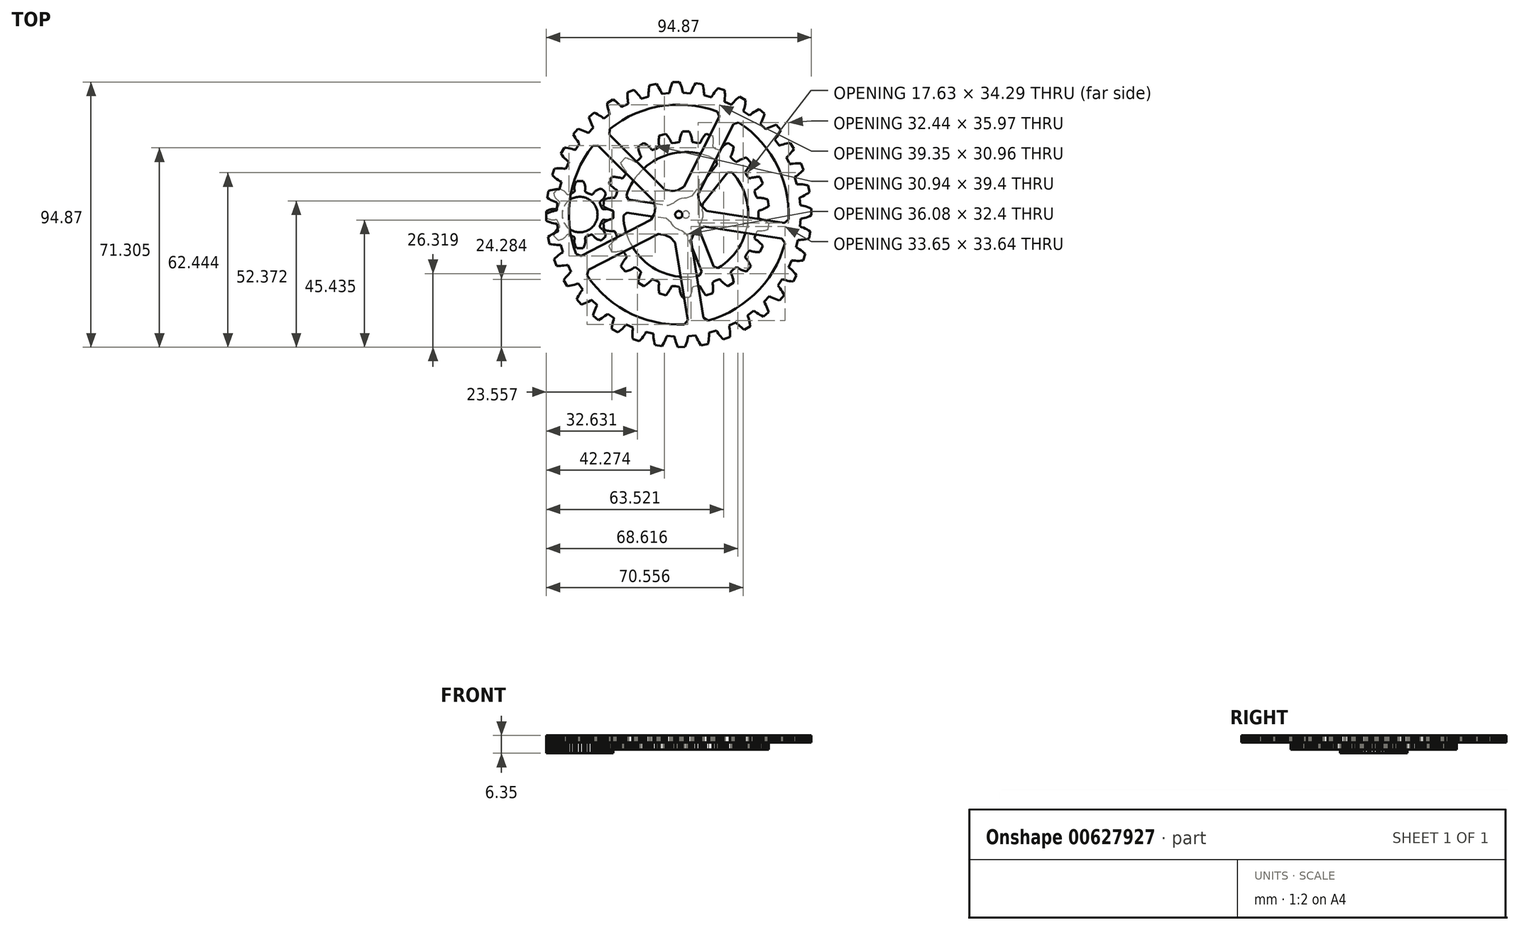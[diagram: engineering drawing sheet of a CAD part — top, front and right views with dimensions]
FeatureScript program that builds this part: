
annotation { "Feature Type Name" : "Feature", "Feature Type Description" : "" }
export const myFeature = defineFeature(function(context is Context, id is Id, definition is map)
    precondition{}
    {
        {
            var Q0;
            Q0=qCreatedBy(makeId("Top.planeOp"),FACE);
            var sketch = newSketch(context, id + "F0", { "sketchPlane" : qUnion([Q0])});
            skLineSegment(sketch, "E0", {"start": v(18.22, -1.29) * mm, "end": v(18.38, -1.34) * mm});
            skLineSegment(sketch, "E1", {"start": v(18.38, -1.34) * mm, "end": v(18.53, -1.39) * mm});
            skLineSegment(sketch, "E2", {"start": v(18.53, -1.39) * mm, "end": v(18.84, -1.5) * mm});
            skLineSegment(sketch, "E3", {"start": v(18.84, -1.5) * mm, "end": v(19.45, -1.75) * mm});
            skLineSegment(sketch, "E4", {"start": v(19.45, -1.75) * mm, "end": v(20.06, -2.03) * mm});
            skLineSegment(sketch, "E5", {"start": v(20.06, -2.03) * mm, "end": v(20.66, -2.35) * mm});
            skLineSegment(sketch, "E6", {"start": v(20.66, -2.35) * mm, "end": v(21.26, -2.69) * mm});
            skLineSegment(sketch, "E7", {"start": v(21.26, -2.69) * mm, "end": v(21.86, -3.06) * mm});
            skLineSegment(sketch, "E8", {"start": v(21.86, -3.06) * mm, "end": v(21.48, -5.52) * mm});
            skLineSegment(sketch, "E9", {"start": v(21.48, -5.52) * mm, "end": v(20.8, -5.7) * mm});
            skLineSegment(sketch, "E10", {"start": v(20.8, -5.7) * mm, "end": v(20.12, -5.84) * mm});
            skLineSegment(sketch, "E11", {"start": v(20.12, -5.84) * mm, "end": v(19.45, -5.96) * mm});
            skLineSegment(sketch, "E12", {"start": v(19.45, -5.96) * mm, "end": v(18.79, -6.04) * mm});
            skLineSegment(sketch, "E13", {"start": v(18.79, -6.04) * mm, "end": v(18.13, -6.1) * mm});
            skLineSegment(sketch, "E14", {"start": v(18.13, -6.1) * mm, "end": v(17.8, -6.1) * mm});
            skLineSegment(sketch, "E15", {"start": v(17.8, -6.1) * mm, "end": v(17.64, -6.11) * mm});
            skLineSegment(sketch, "E16", {"start": v(17.64, -6.11) * mm, "end": v(17.47, -6.11) * mm});
            skLineSegment(sketch, "E17", {"start": v(17.47, -6.11) * mm, "end": v(16.82, -8.76) * mm});
            skLineSegment(sketch, "E18", {"start": v(16.82, -8.76) * mm, "end": v(16.97, -8.84) * mm});
            skLineSegment(sketch, "E19", {"start": v(16.97, -8.84) * mm, "end": v(17.1, -8.91) * mm});
            skLineSegment(sketch, "E20", {"start": v(17.1, -8.91) * mm, "end": v(17.4, -9.08) * mm});
            skLineSegment(sketch, "E21", {"start": v(17.4, -9.08) * mm, "end": v(17.95, -9.43) * mm});
            skLineSegment(sketch, "E22", {"start": v(17.95, -9.43) * mm, "end": v(18.5, -9.82) * mm});
            skLineSegment(sketch, "E23", {"start": v(18.5, -9.82) * mm, "end": v(19.04, -10.23) * mm});
            skLineSegment(sketch, "E24", {"start": v(19.04, -10.23) * mm, "end": v(19.58, -10.67) * mm});
            skLineSegment(sketch, "E25", {"start": v(19.58, -10.67) * mm, "end": v(20.1, -11.14) * mm});
            skLineSegment(sketch, "E26", {"start": v(20.1, -11.14) * mm, "end": v(19.3, -13.5) * mm});
            skLineSegment(sketch, "E27", {"start": v(19.3, -13.5) * mm, "end": v(18.6, -13.55) * mm});
            skLineSegment(sketch, "E28", {"start": v(18.6, -13.55) * mm, "end": v(17.9, -13.58) * mm});
            skLineSegment(sketch, "E29", {"start": v(17.9, -13.58) * mm, "end": v(17.22, -13.58) * mm});
            skLineSegment(sketch, "E30", {"start": v(17.22, -13.58) * mm, "end": v(16.55, -13.54) * mm});
            skLineSegment(sketch, "E31", {"start": v(16.55, -13.54) * mm, "end": v(15.9, -13.48) * mm});
            skLineSegment(sketch, "E32", {"start": v(15.9, -13.48) * mm, "end": v(15.57, -13.44) * mm});
            skLineSegment(sketch, "E33", {"start": v(15.57, -13.44) * mm, "end": v(15.4, -13.41) * mm});
            skLineSegment(sketch, "E34", {"start": v(15.4, -13.41) * mm, "end": v(15.25, -13.38) * mm});
            skLineSegment(sketch, "E35", {"start": v(15.25, -13.38) * mm, "end": v(14.15, -15.88) * mm});
            skLineSegment(sketch, "E36", {"start": v(14.15, -15.88) * mm, "end": v(14.28, -15.98) * mm});
            skLineSegment(sketch, "E37", {"start": v(14.28, -15.98) * mm, "end": v(14.4, -16.08) * mm});
            skLineSegment(sketch, "E38", {"start": v(14.4, -16.08) * mm, "end": v(14.66, -16.3) * mm});
            skLineSegment(sketch, "E39", {"start": v(14.66, -16.3) * mm, "end": v(15.15, -16.73) * mm});
            skLineSegment(sketch, "E40", {"start": v(15.15, -16.73) * mm, "end": v(15.62, -17.2) * mm});
            skLineSegment(sketch, "E41", {"start": v(15.62, -17.2) * mm, "end": v(16.08, -17.71) * mm});
            skLineSegment(sketch, "E42", {"start": v(16.08, -17.71) * mm, "end": v(16.53, -18.24) * mm});
            skLineSegment(sketch, "E43", {"start": v(16.53, -18.24) * mm, "end": v(16.96, -18.79) * mm});
            skLineSegment(sketch, "E44", {"start": v(16.96, -18.79) * mm, "end": v(15.76, -20.97) * mm});
            skLineSegment(sketch, "E45", {"start": v(15.76, -20.97) * mm, "end": v(15.06, -20.9) * mm});
            skLineSegment(sketch, "E46", {"start": v(15.06, -20.9) * mm, "end": v(14.38, -20.8) * mm});
            skLineSegment(sketch, "E47", {"start": v(14.38, -20.8) * mm, "end": v(13.7, -20.7) * mm});
            skLineSegment(sketch, "E48", {"start": v(13.7, -20.7) * mm, "end": v(13.05, -20.54) * mm});
            skLineSegment(sketch, "E49", {"start": v(13.05, -20.54) * mm, "end": v(12.41, -20.37) * mm});
            skLineSegment(sketch, "E50", {"start": v(12.41, -20.37) * mm, "end": v(12.1, -20.27) * mm});
            skLineSegment(sketch, "E51", {"start": v(12.1, -20.27) * mm, "end": v(11.95, -20.21) * mm});
            skLineSegment(sketch, "E52", {"start": v(11.95, -20.21) * mm, "end": v(11.8, -20.16) * mm});
            skLineSegment(sketch, "E53", {"start": v(11.8, -20.16) * mm, "end": v(10.28, -22.43) * mm});
            skLineSegment(sketch, "E54", {"start": v(10.28, -22.43) * mm, "end": v(10.39, -22.55) * mm});
            skLineSegment(sketch, "E55", {"start": v(10.39, -22.55) * mm, "end": v(10.5, -22.67) * mm});
            skLineSegment(sketch, "E56", {"start": v(10.5, -22.67) * mm, "end": v(10.7, -22.92) * mm});
            skLineSegment(sketch, "E57", {"start": v(10.7, -22.92) * mm, "end": v(11.11, -23.44) * mm});
            skLineSegment(sketch, "E58", {"start": v(11.11, -23.44) * mm, "end": v(11.5, -24) * mm});
            skLineSegment(sketch, "E59", {"start": v(11.5, -24) * mm, "end": v(11.86, -24.57) * mm});
            skLineSegment(sketch, "E60", {"start": v(11.86, -24.57) * mm, "end": v(12.21, -25.16) * mm});
            skLineSegment(sketch, "E61", {"start": v(12.21, -25.16) * mm, "end": v(12.54, -25.78) * mm});
            skLineSegment(sketch, "E62", {"start": v(12.54, -25.78) * mm, "end": v(10.98, -27.72) * mm});
            skLineSegment(sketch, "E63", {"start": v(10.98, -27.72) * mm, "end": v(10.3, -27.53) * mm});
            skLineSegment(sketch, "E64", {"start": v(10.3, -27.53) * mm, "end": v(9.65, -27.32) * mm});
            skLineSegment(sketch, "E65", {"start": v(9.65, -27.32) * mm, "end": v(9, -27.09) * mm});
            skLineSegment(sketch, "E66", {"start": v(9, -27.09) * mm, "end": v(8.39, -26.83) * mm});
            skLineSegment(sketch, "E67", {"start": v(8.39, -26.83) * mm, "end": v(7.8, -26.54) * mm});
            skLineSegment(sketch, "E68", {"start": v(7.8, -26.54) * mm, "end": v(7.5, -26.4) * mm});
            skLineSegment(sketch, "E69", {"start": v(7.5, -26.4) * mm, "end": v(7.36, -26.31) * mm});
            skLineSegment(sketch, "E70", {"start": v(7.36, -26.31) * mm, "end": v(7.22, -26.23) * mm});
            skLineSegment(sketch, "E71", {"start": v(7.22, -26.23) * mm, "end": v(5.33, -28.2) * mm});
            skLineSegment(sketch, "E72", {"start": v(5.33, -28.2) * mm, "end": v(5.42, -28.34) * mm});
            skLineSegment(sketch, "E73", {"start": v(5.42, -28.34) * mm, "end": v(5.5, -28.48) * mm});
            skLineSegment(sketch, "E74", {"start": v(5.5, -28.48) * mm, "end": v(5.67, -28.76) * mm});
            skLineSegment(sketch, "E75", {"start": v(5.67, -28.76) * mm, "end": v(5.98, -29.34) * mm});
            skLineSegment(sketch, "E76", {"start": v(5.98, -29.34) * mm, "end": v(6.26, -29.95) * mm});
            skLineSegment(sketch, "E77", {"start": v(6.26, -29.95) * mm, "end": v(6.52, -30.58) * mm});
            skLineSegment(sketch, "E78", {"start": v(6.52, -30.58) * mm, "end": v(6.76, -31.23) * mm});
            skLineSegment(sketch, "E79", {"start": v(6.76, -31.23) * mm, "end": v(6.98, -31.9) * mm});
            skLineSegment(sketch, "E80", {"start": v(6.98, -31.9) * mm, "end": v(5.1, -33.54) * mm});
            skLineSegment(sketch, "E81", {"start": v(5.1, -33.54) * mm, "end": v(4.47, -33.23) * mm});
            skLineSegment(sketch, "E82", {"start": v(4.47, -33.23) * mm, "end": v(3.86, -32.91) * mm});
            skLineSegment(sketch, "E83", {"start": v(3.86, -32.91) * mm, "end": v(3.27, -32.57) * mm});
            skLineSegment(sketch, "E84", {"start": v(3.27, -32.57) * mm, "end": v(2.7, -32.2) * mm});
            skLineSegment(sketch, "E85", {"start": v(2.7, -32.2) * mm, "end": v(2.17, -31.82) * mm});
            skLineSegment(sketch, "E86", {"start": v(2.17, -31.82) * mm, "end": v(1.9, -31.62) * mm});
            skLineSegment(sketch, "E87", {"start": v(1.9, -31.62) * mm, "end": v(1.78, -31.52) * mm});
            skLineSegment(sketch, "E88", {"start": v(1.78, -31.52) * mm, "end": v(1.66, -31.42) * mm});
            skLineSegment(sketch, "E89", {"start": v(1.66, -31.42) * mm, "end": v(-0.55, -33.03) * mm});
            skLineSegment(sketch, "E90", {"start": v(-0.55, -33.03) * mm, "end": v(-0.48, -33.18) * mm});
            skLineSegment(sketch, "E91", {"start": v(-0.48, -33.18) * mm, "end": v(-0.42, -33.33) * mm});
            skLineSegment(sketch, "E92", {"start": v(-0.42, -33.33) * mm, "end": v(-0.3, -33.64) * mm});
            skLineSegment(sketch, "E93", {"start": v(-0.3, -33.64) * mm, "end": v(-0.1, -34.27) * mm});
            skLineSegment(sketch, "E94", {"start": v(-0.1, -34.27) * mm, "end": v(0.07, -34.92) * mm});
            skLineSegment(sketch, "E95", {"start": v(0.07, -34.92) * mm, "end": v(0.21, -35.58) * mm});
            skLineSegment(sketch, "E96", {"start": v(0.21, -35.58) * mm, "end": v(0.34, -36.26) * mm});
            skLineSegment(sketch, "E97", {"start": v(0.34, -36.26) * mm, "end": v(0.44, -36.95) * mm});
            skLineSegment(sketch, "E98", {"start": v(0.44, -36.95) * mm, "end": v(-1.7, -38.24) * mm});
            skLineSegment(sketch, "E99", {"start": v(-1.7, -38.24) * mm, "end": v(-2.26, -37.83) * mm});
            skLineSegment(sketch, "E100", {"start": v(-2.26, -37.83) * mm, "end": v(-2.81, -37.41) * mm});
            skLineSegment(sketch, "E101", {"start": v(-2.81, -37.41) * mm, "end": v(-3.33, -36.97) * mm});
            skLineSegment(sketch, "E102", {"start": v(-3.33, -36.97) * mm, "end": v(-3.83, -36.52) * mm});
            skLineSegment(sketch, "E103", {"start": v(-3.83, -36.52) * mm, "end": v(-4.3, -36.05) * mm});
            skLineSegment(sketch, "E104", {"start": v(-4.3, -36.05) * mm, "end": v(-4.5, -35.8) * mm});
            skLineSegment(sketch, "E105", {"start": v(-4.5, -35.8) * mm, "end": v(-4.62, -35.68) * mm});
            skLineSegment(sketch, "E106", {"start": v(-4.62, -35.68) * mm, "end": v(-4.72, -35.56) * mm});
            skLineSegment(sketch, "E107", {"start": v(-4.72, -35.56) * mm, "end": v(-7.17, -36.76) * mm});
            skLineSegment(sketch, "E108", {"start": v(-7.17, -36.76) * mm, "end": v(-7.13, -36.92) * mm});
            skLineSegment(sketch, "E109", {"start": v(-7.13, -36.92) * mm, "end": v(-7.1, -37.08) * mm});
            skLineSegment(sketch, "E110", {"start": v(-7.1, -37.08) * mm, "end": v(-7.04, -37.4) * mm});
            skLineSegment(sketch, "E111", {"start": v(-7.04, -37.4) * mm, "end": v(-6.95, -38.06) * mm});
            skLineSegment(sketch, "E112", {"start": v(-6.95, -38.06) * mm, "end": v(-6.9, -38.73) * mm});
            skLineSegment(sketch, "E113", {"start": v(-6.9, -38.73) * mm, "end": v(-6.87, -39.4) * mm});
            skLineSegment(sketch, "E114", {"start": v(-6.87, -39.4) * mm, "end": v(-6.86, -40.1) * mm});
            skLineSegment(sketch, "E115", {"start": v(-6.86, -40.1) * mm, "end": v(-6.89, -40.8) * mm});
            skLineSegment(sketch, "E116", {"start": v(-6.89, -40.8) * mm, "end": v(-9.2, -41.7) * mm});
            skLineSegment(sketch, "E117", {"start": v(-9.2, -41.7) * mm, "end": v(-9.7, -41.2) * mm});
            skLineSegment(sketch, "E118", {"start": v(-9.7, -41.2) * mm, "end": v(-10.16, -40.69) * mm});
            skLineSegment(sketch, "E119", {"start": v(-10.16, -40.69) * mm, "end": v(-10.6, -40.16) * mm});
            skLineSegment(sketch, "E120", {"start": v(-10.6, -40.16) * mm, "end": v(-11, -39.63) * mm});
            skLineSegment(sketch, "E121", {"start": v(-11, -39.63) * mm, "end": v(-11.38, -39.08) * mm});
            skLineSegment(sketch, "E122", {"start": v(-11.38, -39.08) * mm, "end": v(-11.56, -38.8) * mm});
            skLineSegment(sketch, "E123", {"start": v(-11.56, -38.8) * mm, "end": v(-11.64, -38.67) * mm});
            skLineSegment(sketch, "E124", {"start": v(-11.64, -38.67) * mm, "end": v(-11.72, -38.53) * mm});
            skLineSegment(sketch, "E125", {"start": v(-11.72, -38.53) * mm, "end": v(-14.34, -39.29) * mm});
            skLineSegment(sketch, "E126", {"start": v(-14.34, -39.29) * mm, "end": v(-14.33, -39.45) * mm});
            skLineSegment(sketch, "E127", {"start": v(-14.33, -39.45) * mm, "end": v(-14.33, -39.61) * mm});
            skLineSegment(sketch, "E128", {"start": v(-14.33, -39.61) * mm, "end": v(-14.33, -39.94) * mm});
            skLineSegment(sketch, "E129", {"start": v(-14.33, -39.94) * mm, "end": v(-14.35, -40.6) * mm});
            skLineSegment(sketch, "E130", {"start": v(-14.35, -40.6) * mm, "end": v(-14.41, -41.27) * mm});
            skLineSegment(sketch, "E131", {"start": v(-14.41, -41.27) * mm, "end": v(-14.5, -41.95) * mm});
            skLineSegment(sketch, "E132", {"start": v(-14.5, -41.95) * mm, "end": v(-14.62, -42.63) * mm});
            skLineSegment(sketch, "E133", {"start": v(-14.62, -42.63) * mm, "end": v(-14.76, -43.31) * mm});
            skLineSegment(sketch, "E134", {"start": v(-14.76, -43.31) * mm, "end": v(-17.2, -43.8) * mm});
            skLineSegment(sketch, "E135", {"start": v(-17.2, -43.8) * mm, "end": v(-17.6, -43.22) * mm});
            skLineSegment(sketch, "E136", {"start": v(-17.6, -43.22) * mm, "end": v(-17.97, -42.63) * mm});
            skLineSegment(sketch, "E137", {"start": v(-17.97, -42.63) * mm, "end": v(-18.3, -42.04) * mm});
            skLineSegment(sketch, "E138", {"start": v(-18.3, -42.04) * mm, "end": v(-18.62, -41.45) * mm});
            skLineSegment(sketch, "E139", {"start": v(-18.62, -41.45) * mm, "end": v(-18.9, -40.84) * mm});
            skLineSegment(sketch, "E140", {"start": v(-18.9, -40.84) * mm, "end": v(-19.02, -40.54) * mm});
            skLineSegment(sketch, "E141", {"start": v(-19.02, -40.54) * mm, "end": v(-19.07, -40.39) * mm});
            skLineSegment(sketch, "E142", {"start": v(-19.07, -40.39) * mm, "end": v(-19.13, -40.24) * mm});
            skLineSegment(sketch, "E143", {"start": v(-19.13, -40.24) * mm, "end": v(-21.84, -40.53) * mm});
            skLineSegment(sketch, "E144", {"start": v(-21.84, -40.53) * mm, "end": v(-21.86, -40.7) * mm});
            skLineSegment(sketch, "E145", {"start": v(-21.86, -40.7) * mm, "end": v(-21.89, -40.85) * mm});
            skLineSegment(sketch, "E146", {"start": v(-21.89, -40.85) * mm, "end": v(-21.94, -41.18) * mm});
            skLineSegment(sketch, "E147", {"start": v(-21.94, -41.18) * mm, "end": v(-22.08, -41.82) * mm});
            skLineSegment(sketch, "E148", {"start": v(-22.08, -41.82) * mm, "end": v(-22.26, -42.47) * mm});
            skLineSegment(sketch, "E149", {"start": v(-22.26, -42.47) * mm, "end": v(-22.46, -43.12) * mm});
            skLineSegment(sketch, "E150", {"start": v(-22.46, -43.12) * mm, "end": v(-22.7, -43.77) * mm});
            skLineSegment(sketch, "E151", {"start": v(-22.7, -43.77) * mm, "end": v(-22.96, -44.42) * mm});
            skLineSegment(sketch, "E152", {"start": v(-22.96, -44.42) * mm, "end": v(-25.45, -44.47) * mm});
            skLineSegment(sketch, "E153", {"start": v(-25.45, -44.47) * mm, "end": v(-25.74, -43.83) * mm});
            skLineSegment(sketch, "E154", {"start": v(-25.74, -43.83) * mm, "end": v(-26, -43.2) * mm});
            skLineSegment(sketch, "E155", {"start": v(-26, -43.2) * mm, "end": v(-26.23, -42.55) * mm});
            skLineSegment(sketch, "E156", {"start": v(-26.23, -42.55) * mm, "end": v(-26.43, -41.91) * mm});
            skLineSegment(sketch, "E157", {"start": v(-26.43, -41.91) * mm, "end": v(-26.6, -41.27) * mm});
            skLineSegment(sketch, "E158", {"start": v(-26.6, -41.27) * mm, "end": v(-26.67, -40.95) * mm});
            skLineSegment(sketch, "E159", {"start": v(-26.67, -40.95) * mm, "end": v(-26.7, -40.8) * mm});
            skLineSegment(sketch, "E160", {"start": v(-26.7, -40.8) * mm, "end": v(-26.72, -40.63) * mm});
            skLineSegment(sketch, "E161", {"start": v(-26.72, -40.63) * mm, "end": v(-29.45, -40.45) * mm});
            skLineSegment(sketch, "E162", {"start": v(-29.45, -40.45) * mm, "end": v(-29.5, -40.6) * mm});
            skLineSegment(sketch, "E163", {"start": v(-29.5, -40.6) * mm, "end": v(-29.55, -40.76) * mm});
            skLineSegment(sketch, "E164", {"start": v(-29.55, -40.76) * mm, "end": v(-29.66, -41.07) * mm});
            skLineSegment(sketch, "E165", {"start": v(-29.66, -41.07) * mm, "end": v(-29.9, -41.68) * mm});
            skLineSegment(sketch, "E166", {"start": v(-29.9, -41.68) * mm, "end": v(-30.2, -42.3) * mm});
            skLineSegment(sketch, "E167", {"start": v(-30.2, -42.3) * mm, "end": v(-30.5, -42.9) * mm});
            skLineSegment(sketch, "E168", {"start": v(-30.5, -42.9) * mm, "end": v(-30.85, -43.5) * mm});
            skLineSegment(sketch, "E169", {"start": v(-30.85, -43.5) * mm, "end": v(-31.22, -44.09) * mm});
            skLineSegment(sketch, "E170", {"start": v(-31.22, -44.09) * mm, "end": v(-33.68, -43.7) * mm});
            skLineSegment(sketch, "E171", {"start": v(-33.68, -43.7) * mm, "end": v(-33.85, -43.03) * mm});
            skLineSegment(sketch, "E172", {"start": v(-33.85, -43.03) * mm, "end": v(-34, -42.35) * mm});
            skLineSegment(sketch, "E173", {"start": v(-34, -42.35) * mm, "end": v(-34.12, -41.68) * mm});
            skLineSegment(sketch, "E174", {"start": v(-34.12, -41.68) * mm, "end": v(-34.2, -41.02) * mm});
            skLineSegment(sketch, "E175", {"start": v(-34.2, -41.02) * mm, "end": v(-34.26, -40.36) * mm});
            skLineSegment(sketch, "E176", {"start": v(-34.26, -40.36) * mm, "end": v(-34.27, -40.03) * mm});
            skLineSegment(sketch, "E177", {"start": v(-34.27, -40.03) * mm, "end": v(-34.27, -39.87) * mm});
            skLineSegment(sketch, "E178", {"start": v(-34.27, -39.87) * mm, "end": v(-34.27, -39.7) * mm});
            skLineSegment(sketch, "E179", {"start": v(-34.27, -39.7) * mm, "end": v(-36.92, -39.05) * mm});
            skLineSegment(sketch, "E180", {"start": v(-36.92, -39.05) * mm, "end": v(-37, -39.2) * mm});
            skLineSegment(sketch, "E181", {"start": v(-37, -39.2) * mm, "end": v(-37.07, -39.34) * mm});
            skLineSegment(sketch, "E182", {"start": v(-37.07, -39.34) * mm, "end": v(-37.24, -39.63) * mm});
            skLineSegment(sketch, "E183", {"start": v(-37.24, -39.63) * mm, "end": v(-37.59, -40.19) * mm});
            skLineSegment(sketch, "E184", {"start": v(-37.59, -40.19) * mm, "end": v(-37.97, -40.74) * mm});
            skLineSegment(sketch, "E185", {"start": v(-37.97, -40.74) * mm, "end": v(-38.39, -41.28) * mm});
            skLineSegment(sketch, "E186", {"start": v(-38.39, -41.28) * mm, "end": v(-38.83, -41.8) * mm});
            skLineSegment(sketch, "E187", {"start": v(-38.83, -41.8) * mm, "end": v(-39.3, -42.33) * mm});
            skLineSegment(sketch, "E188", {"start": v(-39.3, -42.33) * mm, "end": v(-41.66, -41.53) * mm});
            skLineSegment(sketch, "E189", {"start": v(-41.66, -41.53) * mm, "end": v(-41.7, -40.83) * mm});
            skLineSegment(sketch, "E190", {"start": v(-41.7, -40.83) * mm, "end": v(-41.74, -40.14) * mm});
            skLineSegment(sketch, "E191", {"start": v(-41.74, -40.14) * mm, "end": v(-41.73, -39.46) * mm});
            skLineSegment(sketch, "E192", {"start": v(-41.73, -39.46) * mm, "end": v(-41.7, -38.79) * mm});
            skLineSegment(sketch, "E193", {"start": v(-41.7, -38.79) * mm, "end": v(-41.64, -38.13) * mm});
            skLineSegment(sketch, "E194", {"start": v(-41.64, -38.13) * mm, "end": v(-41.6, -37.8) * mm});
            skLineSegment(sketch, "E195", {"start": v(-41.6, -37.8) * mm, "end": v(-41.57, -37.64) * mm});
            skLineSegment(sketch, "E196", {"start": v(-41.57, -37.64) * mm, "end": v(-41.54, -37.48) * mm});
            skLineSegment(sketch, "E197", {"start": v(-41.54, -37.48) * mm, "end": v(-44.04, -36.38) * mm});
            skLineSegment(sketch, "E198", {"start": v(-44.04, -36.38) * mm, "end": v(-44.14, -36.5) * mm});
            skLineSegment(sketch, "E199", {"start": v(-44.14, -36.5) * mm, "end": v(-44.24, -36.64) * mm});
            skLineSegment(sketch, "E200", {"start": v(-44.24, -36.64) * mm, "end": v(-44.45, -36.89) * mm});
            skLineSegment(sketch, "E201", {"start": v(-44.45, -36.89) * mm, "end": v(-44.9, -37.38) * mm});
            skLineSegment(sketch, "E202", {"start": v(-44.9, -37.38) * mm, "end": v(-45.37, -37.85) * mm});
            skLineSegment(sketch, "E203", {"start": v(-45.37, -37.85) * mm, "end": v(-45.87, -38.31) * mm});
            skLineSegment(sketch, "E204", {"start": v(-45.87, -38.31) * mm, "end": v(-46.4, -38.76) * mm});
            skLineSegment(sketch, "E205", {"start": v(-46.4, -38.76) * mm, "end": v(-46.95, -39.2) * mm});
            skLineSegment(sketch, "E206", {"start": v(-46.95, -39.2) * mm, "end": v(-49.13, -38) * mm});
            skLineSegment(sketch, "E207", {"start": v(-49.13, -38) * mm, "end": v(-49.06, -37.3) * mm});
            skLineSegment(sketch, "E208", {"start": v(-49.06, -37.3) * mm, "end": v(-48.97, -36.61) * mm});
            skLineSegment(sketch, "E209", {"start": v(-48.97, -36.61) * mm, "end": v(-48.85, -35.94) * mm});
            skLineSegment(sketch, "E210", {"start": v(-48.85, -35.94) * mm, "end": v(-48.7, -35.28) * mm});
            skLineSegment(sketch, "E211", {"start": v(-48.7, -35.28) * mm, "end": v(-48.53, -34.65) * mm});
            skLineSegment(sketch, "E212", {"start": v(-48.53, -34.65) * mm, "end": v(-48.43, -34.33) * mm});
            skLineSegment(sketch, "E213", {"start": v(-48.43, -34.33) * mm, "end": v(-48.37, -34.18) * mm});
            skLineSegment(sketch, "E214", {"start": v(-48.37, -34.18) * mm, "end": v(-48.32, -34.03) * mm});
            skLineSegment(sketch, "E215", {"start": v(-48.32, -34.03) * mm, "end": v(-50.59, -32.51) * mm});
            skLineSegment(sketch, "E216", {"start": v(-50.59, -32.51) * mm, "end": v(-50.7, -32.62) * mm});
            skLineSegment(sketch, "E217", {"start": v(-50.7, -32.62) * mm, "end": v(-50.83, -32.73) * mm});
            skLineSegment(sketch, "E218", {"start": v(-50.83, -32.73) * mm, "end": v(-51.08, -32.94) * mm});
            skLineSegment(sketch, "E219", {"start": v(-51.08, -32.94) * mm, "end": v(-51.6, -33.35) * mm});
            skLineSegment(sketch, "E220", {"start": v(-51.6, -33.35) * mm, "end": v(-52.15, -33.73) * mm});
            skLineSegment(sketch, "E221", {"start": v(-52.15, -33.73) * mm, "end": v(-52.72, -34.1) * mm});
            skLineSegment(sketch, "E222", {"start": v(-52.72, -34.1) * mm, "end": v(-53.32, -34.44) * mm});
            skLineSegment(sketch, "E223", {"start": v(-53.32, -34.44) * mm, "end": v(-53.94, -34.77) * mm});
            skLineSegment(sketch, "E224", {"start": v(-53.94, -34.77) * mm, "end": v(-55.88, -33.21) * mm});
            skLineSegment(sketch, "E225", {"start": v(-55.88, -33.21) * mm, "end": v(-55.7, -32.54) * mm});
            skLineSegment(sketch, "E226", {"start": v(-55.7, -32.54) * mm, "end": v(-55.48, -31.88) * mm});
            skLineSegment(sketch, "E227", {"start": v(-55.48, -31.88) * mm, "end": v(-55.25, -31.24) * mm});
            skLineSegment(sketch, "E228", {"start": v(-55.25, -31.24) * mm, "end": v(-54.99, -30.62) * mm});
            skLineSegment(sketch, "E229", {"start": v(-54.99, -30.62) * mm, "end": v(-54.7, -30.02) * mm});
            skLineSegment(sketch, "E230", {"start": v(-54.7, -30.02) * mm, "end": v(-54.55, -29.73) * mm});
            skLineSegment(sketch, "E231", {"start": v(-54.55, -29.73) * mm, "end": v(-54.47, -29.6) * mm});
            skLineSegment(sketch, "E232", {"start": v(-54.47, -29.6) * mm, "end": v(-54.39, -29.45) * mm});
            skLineSegment(sketch, "E233", {"start": v(-54.39, -29.45) * mm, "end": v(-56.36, -27.56) * mm});
            skLineSegment(sketch, "E234", {"start": v(-56.36, -27.56) * mm, "end": v(-56.5, -27.65) * mm});
            skLineSegment(sketch, "E235", {"start": v(-56.5, -27.65) * mm, "end": v(-56.64, -27.73) * mm});
            skLineSegment(sketch, "E236", {"start": v(-56.64, -27.73) * mm, "end": v(-56.92, -27.9) * mm});
            skLineSegment(sketch, "E237", {"start": v(-56.92, -27.9) * mm, "end": v(-57.5, -28.2) * mm});
            skLineSegment(sketch, "E238", {"start": v(-57.5, -28.2) * mm, "end": v(-58.11, -28.5) * mm});
            skLineSegment(sketch, "E239", {"start": v(-58.11, -28.5) * mm, "end": v(-58.74, -28.75) * mm});
            skLineSegment(sketch, "E240", {"start": v(-58.74, -28.75) * mm, "end": v(-59.39, -29) * mm});
            skLineSegment(sketch, "E241", {"start": v(-59.39, -29) * mm, "end": v(-60.05, -29.2) * mm});
            skLineSegment(sketch, "E242", {"start": v(-60.05, -29.2) * mm, "end": v(-61.7, -27.33) * mm});
            skLineSegment(sketch, "E243", {"start": v(-61.7, -27.33) * mm, "end": v(-61.4, -26.7) * mm});
            skLineSegment(sketch, "E244", {"start": v(-61.4, -26.7) * mm, "end": v(-61.07, -26.1) * mm});
            skLineSegment(sketch, "E245", {"start": v(-61.07, -26.1) * mm, "end": v(-60.73, -25.5) * mm});
            skLineSegment(sketch, "E246", {"start": v(-60.73, -25.5) * mm, "end": v(-60.37, -24.94) * mm});
            skLineSegment(sketch, "E247", {"start": v(-60.37, -24.94) * mm, "end": v(-59.98, -24.4) * mm});
            skLineSegment(sketch, "E248", {"start": v(-59.98, -24.4) * mm, "end": v(-59.78, -24.14) * mm});
            skLineSegment(sketch, "E249", {"start": v(-59.78, -24.14) * mm, "end": v(-59.68, -24.01) * mm});
            skLineSegment(sketch, "E250", {"start": v(-59.68, -24.01) * mm, "end": v(-59.57, -23.89) * mm});
            skLineSegment(sketch, "E251", {"start": v(-59.57, -23.89) * mm, "end": v(-61.19, -21.69) * mm});
            skLineSegment(sketch, "E252", {"start": v(-61.19, -21.69) * mm, "end": v(-61.34, -21.75) * mm});
            skLineSegment(sketch, "E253", {"start": v(-61.34, -21.75) * mm, "end": v(-61.49, -21.8) * mm});
            skLineSegment(sketch, "E254", {"start": v(-61.49, -21.8) * mm, "end": v(-61.8, -21.92) * mm});
            skLineSegment(sketch, "E255", {"start": v(-61.8, -21.92) * mm, "end": v(-62.43, -22.12) * mm});
            skLineSegment(sketch, "E256", {"start": v(-62.43, -22.12) * mm, "end": v(-63.07, -22.3) * mm});
            skLineSegment(sketch, "E257", {"start": v(-63.07, -22.3) * mm, "end": v(-63.74, -22.45) * mm});
            skLineSegment(sketch, "E258", {"start": v(-63.74, -22.45) * mm, "end": v(-64.42, -22.57) * mm});
            skLineSegment(sketch, "E259", {"start": v(-64.42, -22.57) * mm, "end": v(-65.11, -22.67) * mm});
            skLineSegment(sketch, "E260", {"start": v(-65.11, -22.67) * mm, "end": v(-66.4, -20.54) * mm});
            skLineSegment(sketch, "E261", {"start": v(-66.4, -20.54) * mm, "end": v(-66, -19.97) * mm});
            skLineSegment(sketch, "E262", {"start": v(-66, -19.97) * mm, "end": v(-65.57, -19.42) * mm});
            skLineSegment(sketch, "E263", {"start": v(-65.57, -19.42) * mm, "end": v(-65.13, -18.9) * mm});
            skLineSegment(sketch, "E264", {"start": v(-65.13, -18.9) * mm, "end": v(-64.68, -18.4) * mm});
            skLineSegment(sketch, "E265", {"start": v(-64.68, -18.4) * mm, "end": v(-64.2, -17.94) * mm});
            skLineSegment(sketch, "E266", {"start": v(-64.2, -17.94) * mm, "end": v(-63.96, -17.72) * mm});
            skLineSegment(sketch, "E267", {"start": v(-63.96, -17.72) * mm, "end": v(-63.84, -17.62) * mm});
            skLineSegment(sketch, "E268", {"start": v(-63.84, -17.62) * mm, "end": v(-63.72, -17.51) * mm});
            skLineSegment(sketch, "E269", {"start": v(-63.72, -17.51) * mm, "end": v(-64.92, -15.06) * mm});
            skLineSegment(sketch, "E270", {"start": v(-64.92, -15.06) * mm, "end": v(-65.08, -15.1) * mm});
            skLineSegment(sketch, "E271", {"start": v(-65.08, -15.1) * mm, "end": v(-65.24, -15.13) * mm});
            skLineSegment(sketch, "E272", {"start": v(-65.24, -15.13) * mm, "end": v(-65.56, -15.19) * mm});
            skLineSegment(sketch, "E273", {"start": v(-65.56, -15.19) * mm, "end": v(-66.22, -15.28) * mm});
            skLineSegment(sketch, "E274", {"start": v(-66.22, -15.28) * mm, "end": v(-66.89, -15.34) * mm});
            skLineSegment(sketch, "E275", {"start": v(-66.89, -15.34) * mm, "end": v(-67.57, -15.37) * mm});
            skLineSegment(sketch, "E276", {"start": v(-67.57, -15.37) * mm, "end": v(-68.26, -15.37) * mm});
            skLineSegment(sketch, "E277", {"start": v(-68.26, -15.37) * mm, "end": v(-68.96, -15.35) * mm});
            skLineSegment(sketch, "E278", {"start": v(-68.96, -15.35) * mm, "end": v(-69.86, -13.02) * mm});
            skLineSegment(sketch, "E279", {"start": v(-69.86, -13.02) * mm, "end": v(-69.36, -12.53) * mm});
            skLineSegment(sketch, "E280", {"start": v(-69.36, -12.53) * mm, "end": v(-68.84, -12.07) * mm});
            skLineSegment(sketch, "E281", {"start": v(-68.84, -12.07) * mm, "end": v(-68.32, -11.63) * mm});
            skLineSegment(sketch, "E282", {"start": v(-68.32, -11.63) * mm, "end": v(-67.79, -11.23) * mm});
            skLineSegment(sketch, "E283", {"start": v(-67.79, -11.23) * mm, "end": v(-67.24, -10.85) * mm});
            skLineSegment(sketch, "E284", {"start": v(-67.24, -10.85) * mm, "end": v(-66.97, -10.68) * mm});
            skLineSegment(sketch, "E285", {"start": v(-66.97, -10.68) * mm, "end": v(-66.83, -10.6) * mm});
            skLineSegment(sketch, "E286", {"start": v(-66.83, -10.6) * mm, "end": v(-66.69, -10.51) * mm});
            skLineSegment(sketch, "E287", {"start": v(-66.69, -10.51) * mm, "end": v(-67.45, -7.9) * mm});
            skLineSegment(sketch, "E288", {"start": v(-67.45, -7.9) * mm, "end": v(-67.6, -7.9) * mm});
            skLineSegment(sketch, "E289", {"start": v(-67.6, -7.9) * mm, "end": v(-67.77, -7.9) * mm});
            skLineSegment(sketch, "E290", {"start": v(-67.77, -7.9) * mm, "end": v(-68.1, -7.9) * mm});
            skLineSegment(sketch, "E291", {"start": v(-68.1, -7.9) * mm, "end": v(-68.76, -7.88) * mm});
            skLineSegment(sketch, "E292", {"start": v(-68.76, -7.88) * mm, "end": v(-69.43, -7.82) * mm});
            skLineSegment(sketch, "E293", {"start": v(-69.43, -7.82) * mm, "end": v(-70.1, -7.73) * mm});
            skLineSegment(sketch, "E294", {"start": v(-70.1, -7.73) * mm, "end": v(-70.79, -7.61) * mm});
            skLineSegment(sketch, "E295", {"start": v(-70.79, -7.61) * mm, "end": v(-71.47, -7.47) * mm});
            skLineSegment(sketch, "E296", {"start": v(-71.47, -7.47) * mm, "end": v(-71.95, -5.02) * mm});
            skLineSegment(sketch, "E297", {"start": v(-71.95, -5.02) * mm, "end": v(-71.38, -4.63) * mm});
            skLineSegment(sketch, "E298", {"start": v(-71.38, -4.63) * mm, "end": v(-70.8, -4.26) * mm});
            skLineSegment(sketch, "E299", {"start": v(-70.8, -4.26) * mm, "end": v(-70.2, -3.92) * mm});
            skLineSegment(sketch, "E300", {"start": v(-70.2, -3.92) * mm, "end": v(-69.6, -3.61) * mm});
            skLineSegment(sketch, "E301", {"start": v(-69.6, -3.61) * mm, "end": v(-69, -3.34) * mm});
            skLineSegment(sketch, "E302", {"start": v(-69, -3.34) * mm, "end": v(-68.7, -3.22) * mm});
            skLineSegment(sketch, "E303", {"start": v(-68.7, -3.22) * mm, "end": v(-68.55, -3.16) * mm});
            skLineSegment(sketch, "E304", {"start": v(-68.55, -3.16) * mm, "end": v(-68.4, -3.1) * mm});
            skLineSegment(sketch, "E305", {"start": v(-68.4, -3.1) * mm, "end": v(-68.7, -0.39) * mm});
            skLineSegment(sketch, "E306", {"start": v(-68.7, -0.39) * mm, "end": v(-68.85, -0.37) * mm});
            skLineSegment(sketch, "E307", {"start": v(-68.85, -0.37) * mm, "end": v(-69.01, -0.34) * mm});
            skLineSegment(sketch, "E308", {"start": v(-69.01, -0.34) * mm, "end": v(-69.34, -0.29) * mm});
            skLineSegment(sketch, "E309", {"start": v(-69.34, -0.29) * mm, "end": v(-69.98, -0.15) * mm});
            skLineSegment(sketch, "E310", {"start": v(-69.98, -0.15) * mm, "end": v(-70.63, 0.03) * mm});
            skLineSegment(sketch, "E311", {"start": v(-70.63, 0.03) * mm, "end": v(-71.28, 0.23) * mm});
            skLineSegment(sketch, "E312", {"start": v(-71.28, 0.23) * mm, "end": v(-71.93, 0.46) * mm});
            skLineSegment(sketch, "E313", {"start": v(-71.93, 0.46) * mm, "end": v(-72.58, 0.72) * mm});
            skLineSegment(sketch, "E314", {"start": v(-72.58, 0.72) * mm, "end": v(-72.63, 3.22) * mm});
            skLineSegment(sketch, "E315", {"start": v(-72.63, 3.22) * mm, "end": v(-72, 3.5) * mm});
            skLineSegment(sketch, "E316", {"start": v(-72, 3.5) * mm, "end": v(-71.35, 3.76) * mm});
            skLineSegment(sketch, "E317", {"start": v(-71.35, 3.76) * mm, "end": v(-70.71, 4) * mm});
            skLineSegment(sketch, "E318", {"start": v(-70.71, 4) * mm, "end": v(-70.07, 4.2) * mm});
            skLineSegment(sketch, "E319", {"start": v(-70.07, 4.2) * mm, "end": v(-69.43, 4.36) * mm});
            skLineSegment(sketch, "E320", {"start": v(-69.43, 4.36) * mm, "end": v(-69.11, 4.43) * mm});
            skLineSegment(sketch, "E321", {"start": v(-69.11, 4.43) * mm, "end": v(-68.95, 4.46) * mm});
            skLineSegment(sketch, "E322", {"start": v(-68.95, 4.46) * mm, "end": v(-68.8, 4.5) * mm});
            skLineSegment(sketch, "E323", {"start": v(-68.8, 4.5) * mm, "end": v(-68.61, 7.22) * mm});
            skLineSegment(sketch, "E324", {"start": v(-68.61, 7.22) * mm, "end": v(-68.77, 7.26) * mm});
            skLineSegment(sketch, "E325", {"start": v(-68.77, 7.26) * mm, "end": v(-68.92, 7.32) * mm});
            skLineSegment(sketch, "E326", {"start": v(-68.92, 7.32) * mm, "end": v(-69.23, 7.43) * mm});
            skLineSegment(sketch, "E327", {"start": v(-69.23, 7.43) * mm, "end": v(-69.84, 7.68) * mm});
            skLineSegment(sketch, "E328", {"start": v(-69.84, 7.68) * mm, "end": v(-70.45, 7.96) * mm});
            skLineSegment(sketch, "E329", {"start": v(-70.45, 7.96) * mm, "end": v(-71.05, 8.27) * mm});
            skLineSegment(sketch, "E330", {"start": v(-71.05, 8.27) * mm, "end": v(-71.65, 8.62) * mm});
            skLineSegment(sketch, "E331", {"start": v(-71.65, 8.62) * mm, "end": v(-72.25, 8.99) * mm});
            skLineSegment(sketch, "E332", {"start": v(-72.25, 8.99) * mm, "end": v(-71.87, 11.45) * mm});
            skLineSegment(sketch, "E333", {"start": v(-71.87, 11.45) * mm, "end": v(-71.19, 11.62) * mm});
            skLineSegment(sketch, "E334", {"start": v(-71.19, 11.62) * mm, "end": v(-70.51, 11.77) * mm});
            skLineSegment(sketch, "E335", {"start": v(-70.51, 11.77) * mm, "end": v(-69.84, 11.89) * mm});
            skLineSegment(sketch, "E336", {"start": v(-69.84, 11.89) * mm, "end": v(-69.18, 11.97) * mm});
            skLineSegment(sketch, "E337", {"start": v(-69.18, 11.97) * mm, "end": v(-68.52, 12.02) * mm});
            skLineSegment(sketch, "E338", {"start": v(-68.52, 12.02) * mm, "end": v(-68.2, 12.04) * mm});
            skLineSegment(sketch, "E339", {"start": v(-68.2, 12.04) * mm, "end": v(-68.03, 12.04) * mm});
            skLineSegment(sketch, "E340", {"start": v(-68.03, 12.04) * mm, "end": v(-67.87, 12.04) * mm});
            skLineSegment(sketch, "E341", {"start": v(-67.87, 12.04) * mm, "end": v(-67.21, 14.7) * mm});
            skLineSegment(sketch, "E342", {"start": v(-67.21, 14.7) * mm, "end": v(-67.36, 14.76) * mm});
            skLineSegment(sketch, "E343", {"start": v(-67.36, 14.76) * mm, "end": v(-67.5, 14.84) * mm});
            skLineSegment(sketch, "E344", {"start": v(-67.5, 14.84) * mm, "end": v(-67.79, 15) * mm});
            skLineSegment(sketch, "E345", {"start": v(-67.79, 15) * mm, "end": v(-68.35, 15.36) * mm});
            skLineSegment(sketch, "E346", {"start": v(-68.35, 15.36) * mm, "end": v(-68.9, 15.74) * mm});
            skLineSegment(sketch, "E347", {"start": v(-68.9, 15.74) * mm, "end": v(-69.44, 16.16) * mm});
            skLineSegment(sketch, "E348", {"start": v(-69.44, 16.16) * mm, "end": v(-69.97, 16.6) * mm});
            skLineSegment(sketch, "E349", {"start": v(-69.97, 16.6) * mm, "end": v(-70.49, 17.07) * mm});
            skLineSegment(sketch, "E350", {"start": v(-70.49, 17.07) * mm, "end": v(-69.68, 19.43) * mm});
            skLineSegment(sketch, "E351", {"start": v(-69.68, 19.43) * mm, "end": v(-68.99, 19.48) * mm});
            skLineSegment(sketch, "E352", {"start": v(-68.99, 19.48) * mm, "end": v(-68.3, 19.5) * mm});
            skLineSegment(sketch, "E353", {"start": v(-68.3, 19.5) * mm, "end": v(-67.62, 19.5) * mm});
            skLineSegment(sketch, "E354", {"start": v(-67.62, 19.5) * mm, "end": v(-66.94, 19.47) * mm});
            skLineSegment(sketch, "E355", {"start": v(-66.94, 19.47) * mm, "end": v(-66.29, 19.4) * mm});
            skLineSegment(sketch, "E356", {"start": v(-66.29, 19.4) * mm, "end": v(-65.96, 19.37) * mm});
            skLineSegment(sketch, "E357", {"start": v(-65.96, 19.37) * mm, "end": v(-65.8, 19.34) * mm});
            skLineSegment(sketch, "E358", {"start": v(-65.8, 19.34) * mm, "end": v(-65.64, 19.31) * mm});
            skLineSegment(sketch, "E359", {"start": v(-65.64, 19.31) * mm, "end": v(-64.54, 21.8) * mm});
            skLineSegment(sketch, "E360", {"start": v(-64.54, 21.8) * mm, "end": v(-64.67, 21.9) * mm});
            skLineSegment(sketch, "E361", {"start": v(-64.67, 21.9) * mm, "end": v(-64.8, 22) * mm});
            skLineSegment(sketch, "E362", {"start": v(-64.8, 22) * mm, "end": v(-65.05, 22.22) * mm});
            skLineSegment(sketch, "E363", {"start": v(-65.05, 22.22) * mm, "end": v(-65.54, 22.66) * mm});
            skLineSegment(sketch, "E364", {"start": v(-65.54, 22.66) * mm, "end": v(-66.01, 23.14) * mm});
            skLineSegment(sketch, "E365", {"start": v(-66.01, 23.14) * mm, "end": v(-66.47, 23.64) * mm});
            skLineSegment(sketch, "E366", {"start": v(-66.47, 23.64) * mm, "end": v(-66.92, 24.17) * mm});
            skLineSegment(sketch, "E367", {"start": v(-66.92, 24.17) * mm, "end": v(-67.35, 24.72) * mm});
            skLineSegment(sketch, "E368", {"start": v(-67.35, 24.72) * mm, "end": v(-66.15, 26.9) * mm});
            skLineSegment(sketch, "E369", {"start": v(-66.15, 26.9) * mm, "end": v(-65.45, 26.83) * mm});
            skLineSegment(sketch, "E370", {"start": v(-65.45, 26.83) * mm, "end": v(-64.77, 26.74) * mm});
            skLineSegment(sketch, "E371", {"start": v(-64.77, 26.74) * mm, "end": v(-64.1, 26.62) * mm});
            skLineSegment(sketch, "E372", {"start": v(-64.1, 26.62) * mm, "end": v(-63.44, 26.47) * mm});
            skLineSegment(sketch, "E373", {"start": v(-63.44, 26.47) * mm, "end": v(-62.8, 26.3) * mm});
            skLineSegment(sketch, "E374", {"start": v(-62.8, 26.3) * mm, "end": v(-62.5, 26.2) * mm});
            skLineSegment(sketch, "E375", {"start": v(-62.5, 26.2) * mm, "end": v(-62.34, 26.14) * mm});
            skLineSegment(sketch, "E376", {"start": v(-62.34, 26.14) * mm, "end": v(-62.19, 26.09) * mm});
            skLineSegment(sketch, "E377", {"start": v(-62.19, 26.09) * mm, "end": v(-60.67, 28.35) * mm});
            skLineSegment(sketch, "E378", {"start": v(-60.67, 28.35) * mm, "end": v(-60.78, 28.47) * mm});
            skLineSegment(sketch, "E379", {"start": v(-60.78, 28.47) * mm, "end": v(-60.89, 28.6) * mm});
            skLineSegment(sketch, "E380", {"start": v(-60.89, 28.6) * mm, "end": v(-61.1, 28.84) * mm});
            skLineSegment(sketch, "E381", {"start": v(-61.1, 28.84) * mm, "end": v(-61.5, 29.37) * mm});
            skLineSegment(sketch, "E382", {"start": v(-61.5, 29.37) * mm, "end": v(-61.89, 29.92) * mm});
            skLineSegment(sketch, "E383", {"start": v(-61.89, 29.92) * mm, "end": v(-62.26, 30.5) * mm});
            skLineSegment(sketch, "E384", {"start": v(-62.26, 30.5) * mm, "end": v(-62.6, 31.09) * mm});
            skLineSegment(sketch, "E385", {"start": v(-62.6, 31.09) * mm, "end": v(-62.93, 31.7) * mm});
            skLineSegment(sketch, "E386", {"start": v(-62.93, 31.7) * mm, "end": v(-61.37, 33.65) * mm});
            skLineSegment(sketch, "E387", {"start": v(-61.37, 33.65) * mm, "end": v(-60.7, 33.46) * mm});
            skLineSegment(sketch, "E388", {"start": v(-60.7, 33.46) * mm, "end": v(-60.04, 33.25) * mm});
            skLineSegment(sketch, "E389", {"start": v(-60.04, 33.25) * mm, "end": v(-59.4, 33.01) * mm});
            skLineSegment(sketch, "E390", {"start": v(-59.4, 33.01) * mm, "end": v(-58.78, 32.76) * mm});
            skLineSegment(sketch, "E391", {"start": v(-58.78, 32.76) * mm, "end": v(-58.18, 32.47) * mm});
            skLineSegment(sketch, "E392", {"start": v(-58.18, 32.47) * mm, "end": v(-57.9, 32.32) * mm});
            skLineSegment(sketch, "E393", {"start": v(-57.9, 32.32) * mm, "end": v(-57.75, 32.24) * mm});
            skLineSegment(sketch, "E394", {"start": v(-57.75, 32.24) * mm, "end": v(-57.61, 32.16) * mm});
            skLineSegment(sketch, "E395", {"start": v(-57.61, 32.16) * mm, "end": v(-55.72, 34.13) * mm});
            skLineSegment(sketch, "E396", {"start": v(-55.72, 34.13) * mm, "end": v(-55.8, 34.26) * mm});
            skLineSegment(sketch, "E397", {"start": v(-55.8, 34.26) * mm, "end": v(-55.9, 34.4) * mm});
            skLineSegment(sketch, "E398", {"start": v(-55.9, 34.4) * mm, "end": v(-56.06, 34.69) * mm});
            skLineSegment(sketch, "E399", {"start": v(-56.06, 34.69) * mm, "end": v(-56.37, 35.27) * mm});
            skLineSegment(sketch, "E400", {"start": v(-56.37, 35.27) * mm, "end": v(-56.65, 35.88) * mm});
            skLineSegment(sketch, "E401", {"start": v(-56.65, 35.88) * mm, "end": v(-56.91, 36.5) * mm});
            skLineSegment(sketch, "E402", {"start": v(-56.91, 36.5) * mm, "end": v(-57.15, 37.16) * mm});
            skLineSegment(sketch, "E403", {"start": v(-57.15, 37.16) * mm, "end": v(-57.37, 37.82) * mm});
            skLineSegment(sketch, "E404", {"start": v(-57.37, 37.82) * mm, "end": v(-55.5, 39.46) * mm});
            skLineSegment(sketch, "E405", {"start": v(-55.5, 39.46) * mm, "end": v(-54.86, 39.16) * mm});
            skLineSegment(sketch, "E406", {"start": v(-54.86, 39.16) * mm, "end": v(-54.25, 38.84) * mm});
            skLineSegment(sketch, "E407", {"start": v(-54.25, 38.84) * mm, "end": v(-53.66, 38.5) * mm});
            skLineSegment(sketch, "E408", {"start": v(-53.66, 38.5) * mm, "end": v(-53.1, 38.14) * mm});
            skLineSegment(sketch, "E409", {"start": v(-53.1, 38.14) * mm, "end": v(-52.56, 37.75) * mm});
            skLineSegment(sketch, "E410", {"start": v(-52.56, 37.75) * mm, "end": v(-52.3, 37.55) * mm});
            skLineSegment(sketch, "E411", {"start": v(-52.3, 37.55) * mm, "end": v(-52.17, 37.45) * mm});
            skLineSegment(sketch, "E412", {"start": v(-52.17, 37.45) * mm, "end": v(-52.05, 37.34) * mm});
            skLineSegment(sketch, "E413", {"start": v(-52.05, 37.34) * mm, "end": v(-49.85, 38.96) * mm});
            skLineSegment(sketch, "E414", {"start": v(-49.85, 38.96) * mm, "end": v(-49.9, 39.1) * mm});
            skLineSegment(sketch, "E415", {"start": v(-49.9, 39.1) * mm, "end": v(-49.97, 39.26) * mm});
            skLineSegment(sketch, "E416", {"start": v(-49.97, 39.26) * mm, "end": v(-50.08, 39.56) * mm});
            skLineSegment(sketch, "E417", {"start": v(-50.08, 39.56) * mm, "end": v(-50.28, 40.2) * mm});
            skLineSegment(sketch, "E418", {"start": v(-50.28, 40.2) * mm, "end": v(-50.46, 40.84) * mm});
            skLineSegment(sketch, "E419", {"start": v(-50.46, 40.84) * mm, "end": v(-50.6, 41.5) * mm});
            skLineSegment(sketch, "E420", {"start": v(-50.6, 41.5) * mm, "end": v(-50.73, 42.19) * mm});
            skLineSegment(sketch, "E421", {"start": v(-50.73, 42.19) * mm, "end": v(-50.83, 42.88) * mm});
            skLineSegment(sketch, "E422", {"start": v(-50.83, 42.88) * mm, "end": v(-48.7, 44.17) * mm});
            skLineSegment(sketch, "E423", {"start": v(-48.7, 44.17) * mm, "end": v(-48.13, 43.76) * mm});
            skLineSegment(sketch, "E424", {"start": v(-48.13, 43.76) * mm, "end": v(-47.58, 43.34) * mm});
            skLineSegment(sketch, "E425", {"start": v(-47.58, 43.34) * mm, "end": v(-47.06, 42.9) * mm});
            skLineSegment(sketch, "E426", {"start": v(-47.06, 42.9) * mm, "end": v(-46.57, 42.45) * mm});
            skLineSegment(sketch, "E427", {"start": v(-46.57, 42.45) * mm, "end": v(-46.1, 41.97) * mm});
            skLineSegment(sketch, "E428", {"start": v(-46.1, 41.97) * mm, "end": v(-45.88, 41.73) * mm});
            skLineSegment(sketch, "E429", {"start": v(-45.88, 41.73) * mm, "end": v(-45.78, 41.6) * mm});
            skLineSegment(sketch, "E430", {"start": v(-45.78, 41.6) * mm, "end": v(-45.67, 41.48) * mm});
            skLineSegment(sketch, "E431", {"start": v(-45.67, 41.48) * mm, "end": v(-43.22, 42.69) * mm});
            skLineSegment(sketch, "E432", {"start": v(-43.22, 42.69) * mm, "end": v(-43.26, 42.85) * mm});
            skLineSegment(sketch, "E433", {"start": v(-43.26, 42.85) * mm, "end": v(-43.29, 43) * mm});
            skLineSegment(sketch, "E434", {"start": v(-43.29, 43) * mm, "end": v(-43.35, 43.33) * mm});
            skLineSegment(sketch, "E435", {"start": v(-43.35, 43.33) * mm, "end": v(-43.44, 43.99) * mm});
            skLineSegment(sketch, "E436", {"start": v(-43.44, 43.99) * mm, "end": v(-43.5, 44.65) * mm});
            skLineSegment(sketch, "E437", {"start": v(-43.5, 44.65) * mm, "end": v(-43.53, 45.33) * mm});
            skLineSegment(sketch, "E438", {"start": v(-43.53, 45.33) * mm, "end": v(-43.53, 46.02) * mm});
            skLineSegment(sketch, "E439", {"start": v(-43.53, 46.02) * mm, "end": v(-43.5, 46.72) * mm});
            skLineSegment(sketch, "E440", {"start": v(-43.5, 46.72) * mm, "end": v(-41.18, 47.63) * mm});
            skLineSegment(sketch, "E441", {"start": v(-41.18, 47.63) * mm, "end": v(-40.7, 47.12) * mm});
            skLineSegment(sketch, "E442", {"start": v(-40.7, 47.12) * mm, "end": v(-40.23, 46.61) * mm});
            skLineSegment(sketch, "E443", {"start": v(-40.23, 46.61) * mm, "end": v(-39.8, 46.1) * mm});
            skLineSegment(sketch, "E444", {"start": v(-39.8, 46.1) * mm, "end": v(-39.39, 45.56) * mm});
            skLineSegment(sketch, "E445", {"start": v(-39.39, 45.56) * mm, "end": v(-39, 45.01) * mm});
            skLineSegment(sketch, "E446", {"start": v(-39, 45.01) * mm, "end": v(-38.84, 44.73) * mm});
            skLineSegment(sketch, "E447", {"start": v(-38.84, 44.73) * mm, "end": v(-38.75, 44.6) * mm});
            skLineSegment(sketch, "E448", {"start": v(-38.75, 44.6) * mm, "end": v(-38.67, 44.45) * mm});
            skLineSegment(sketch, "E449", {"start": v(-38.67, 44.45) * mm, "end": v(-36.05, 45.22) * mm});
            skLineSegment(sketch, "E450", {"start": v(-36.05, 45.22) * mm, "end": v(-36.06, 45.38) * mm});
            skLineSegment(sketch, "E451", {"start": v(-36.06, 45.38) * mm, "end": v(-36.06, 45.54) * mm});
            skLineSegment(sketch, "E452", {"start": v(-36.06, 45.54) * mm, "end": v(-36.06, 45.87) * mm});
            skLineSegment(sketch, "E453", {"start": v(-36.06, 45.87) * mm, "end": v(-36.04, 46.53) * mm});
            skLineSegment(sketch, "E454", {"start": v(-36.04, 46.53) * mm, "end": v(-35.98, 47.2) * mm});
            skLineSegment(sketch, "E455", {"start": v(-35.98, 47.2) * mm, "end": v(-35.89, 47.87) * mm});
            skLineSegment(sketch, "E456", {"start": v(-35.89, 47.87) * mm, "end": v(-35.77, 48.55) * mm});
            skLineSegment(sketch, "E457", {"start": v(-35.77, 48.55) * mm, "end": v(-35.63, 49.24) * mm});
            skLineSegment(sketch, "E458", {"start": v(-35.63, 49.24) * mm, "end": v(-33.18, 49.72) * mm});
            skLineSegment(sketch, "E459", {"start": v(-33.18, 49.72) * mm, "end": v(-32.79, 49.14) * mm});
            skLineSegment(sketch, "E460", {"start": v(-32.79, 49.14) * mm, "end": v(-32.42, 48.56) * mm});
            skLineSegment(sketch, "E461", {"start": v(-32.42, 48.56) * mm, "end": v(-32.08, 47.97) * mm});
            skLineSegment(sketch, "E462", {"start": v(-32.08, 47.97) * mm, "end": v(-31.77, 47.37) * mm});
            skLineSegment(sketch, "E463", {"start": v(-31.77, 47.37) * mm, "end": v(-31.5, 46.77) * mm});
            skLineSegment(sketch, "E464", {"start": v(-31.5, 46.77) * mm, "end": v(-31.37, 46.47) * mm});
            skLineSegment(sketch, "E465", {"start": v(-31.37, 46.47) * mm, "end": v(-31.32, 46.32) * mm});
            skLineSegment(sketch, "E466", {"start": v(-31.32, 46.32) * mm, "end": v(-31.26, 46.16) * mm});
            skLineSegment(sketch, "E467", {"start": v(-31.26, 46.16) * mm, "end": v(-28.55, 46.46) * mm});
            skLineSegment(sketch, "E468", {"start": v(-28.55, 46.46) * mm, "end": v(-28.53, 46.62) * mm});
            skLineSegment(sketch, "E469", {"start": v(-28.53, 46.62) * mm, "end": v(-28.5, 46.78) * mm});
            skLineSegment(sketch, "E470", {"start": v(-28.5, 46.78) * mm, "end": v(-28.45, 47.1) * mm});
            skLineSegment(sketch, "E471", {"start": v(-28.45, 47.1) * mm, "end": v(-28.3, 47.75) * mm});
            skLineSegment(sketch, "E472", {"start": v(-28.3, 47.75) * mm, "end": v(-28.13, 48.4) * mm});
            skLineSegment(sketch, "E473", {"start": v(-28.13, 48.4) * mm, "end": v(-27.93, 49.05) * mm});
            skLineSegment(sketch, "E474", {"start": v(-27.93, 49.05) * mm, "end": v(-27.7, 49.7) * mm});
            skLineSegment(sketch, "E475", {"start": v(-27.7, 49.7) * mm, "end": v(-27.43, 50.35) * mm});
            skLineSegment(sketch, "E476", {"start": v(-27.43, 50.35) * mm, "end": v(-24.94, 50.4) * mm});
            skLineSegment(sketch, "E477", {"start": v(-24.94, 50.4) * mm, "end": v(-24.66, 49.76) * mm});
            skLineSegment(sketch, "E478", {"start": v(-24.66, 49.76) * mm, "end": v(-24.4, 49.12) * mm});
            skLineSegment(sketch, "E479", {"start": v(-24.4, 49.12) * mm, "end": v(-24.16, 48.48) * mm});
            skLineSegment(sketch, "E480", {"start": v(-24.16, 48.48) * mm, "end": v(-23.96, 47.84) * mm});
            skLineSegment(sketch, "E481", {"start": v(-23.96, 47.84) * mm, "end": v(-23.8, 47.2) * mm});
            skLineSegment(sketch, "E482", {"start": v(-23.8, 47.2) * mm, "end": v(-23.73, 46.88) * mm});
            skLineSegment(sketch, "E483", {"start": v(-23.73, 46.88) * mm, "end": v(-23.7, 46.72) * mm});
            skLineSegment(sketch, "E484", {"start": v(-23.7, 46.72) * mm, "end": v(-23.67, 46.56) * mm});
            skLineSegment(sketch, "E485", {"start": v(-23.67, 46.56) * mm, "end": v(-20.94, 46.38) * mm});
            skLineSegment(sketch, "E486", {"start": v(-20.94, 46.38) * mm, "end": v(-20.9, 46.53) * mm});
            skLineSegment(sketch, "E487", {"start": v(-20.9, 46.53) * mm, "end": v(-20.84, 46.69) * mm});
            skLineSegment(sketch, "E488", {"start": v(-20.84, 46.69) * mm, "end": v(-20.73, 47) * mm});
            skLineSegment(sketch, "E489", {"start": v(-20.73, 47) * mm, "end": v(-20.48, 47.61) * mm});
            skLineSegment(sketch, "E490", {"start": v(-20.48, 47.61) * mm, "end": v(-20.2, 48.22) * mm});
            skLineSegment(sketch, "E491", {"start": v(-20.2, 48.22) * mm, "end": v(-19.88, 48.82) * mm});
            skLineSegment(sketch, "E492", {"start": v(-19.88, 48.82) * mm, "end": v(-19.54, 49.42) * mm});
            skLineSegment(sketch, "E493", {"start": v(-19.54, 49.42) * mm, "end": v(-19.17, 50.02) * mm});
            skLineSegment(sketch, "E494", {"start": v(-19.17, 50.02) * mm, "end": v(-16.7, 49.64) * mm});
            skLineSegment(sketch, "E495", {"start": v(-16.7, 49.64) * mm, "end": v(-16.54, 48.96) * mm});
            skLineSegment(sketch, "E496", {"start": v(-16.54, 48.96) * mm, "end": v(-16.4, 48.28) * mm});
            skLineSegment(sketch, "E497", {"start": v(-16.4, 48.28) * mm, "end": v(-16.27, 47.61) * mm});
            skLineSegment(sketch, "E498", {"start": v(-16.27, 47.61) * mm, "end": v(-16.19, 46.95) * mm});
            skLineSegment(sketch, "E499", {"start": v(-16.19, 46.95) * mm, "end": v(-16.13, 46.29) * mm});
            skLineSegment(sketch, "E500", {"start": v(-16.13, 46.29) * mm, "end": v(-16.12, 45.96) * mm});
            skLineSegment(sketch, "E501", {"start": v(-16.12, 45.96) * mm, "end": v(-16.12, 45.8) * mm});
            skLineSegment(sketch, "E502", {"start": v(-16.12, 45.8) * mm, "end": v(-16.12, 45.63) * mm});
            skLineSegment(sketch, "E503", {"start": v(-16.12, 45.63) * mm, "end": v(-13.47, 44.98) * mm});
            skLineSegment(sketch, "E504", {"start": v(-13.47, 44.98) * mm, "end": v(-13.4, 45.13) * mm});
            skLineSegment(sketch, "E505", {"start": v(-13.4, 45.13) * mm, "end": v(-13.32, 45.27) * mm});
            skLineSegment(sketch, "E506", {"start": v(-13.32, 45.27) * mm, "end": v(-13.15, 45.55) * mm});
            skLineSegment(sketch, "E507", {"start": v(-13.15, 45.55) * mm, "end": v(-12.8, 46.11) * mm});
            skLineSegment(sketch, "E508", {"start": v(-12.8, 46.11) * mm, "end": v(-12.42, 46.66) * mm});
            skLineSegment(sketch, "E509", {"start": v(-12.42, 46.66) * mm, "end": v(-12, 47.2) * mm});
            skLineSegment(sketch, "E510", {"start": v(-12, 47.2) * mm, "end": v(-11.56, 47.73) * mm});
            skLineSegment(sketch, "E511", {"start": v(-11.56, 47.73) * mm, "end": v(-11.1, 48.26) * mm});
            skLineSegment(sketch, "E512", {"start": v(-11.1, 48.26) * mm, "end": v(-8.73, 47.45) * mm});
            skLineSegment(sketch, "E513", {"start": v(-8.73, 47.45) * mm, "end": v(-8.68, 46.75) * mm});
            skLineSegment(sketch, "E514", {"start": v(-8.68, 46.75) * mm, "end": v(-8.66, 46.06) * mm});
            skLineSegment(sketch, "E515", {"start": v(-8.66, 46.06) * mm, "end": v(-8.66, 45.38) * mm});
            skLineSegment(sketch, "E516", {"start": v(-8.66, 45.38) * mm, "end": v(-8.69, 44.71) * mm});
            skLineSegment(sketch, "E517", {"start": v(-8.69, 44.71) * mm, "end": v(-8.75, 44.05) * mm});
            skLineSegment(sketch, "E518", {"start": v(-8.75, 44.05) * mm, "end": v(-8.8, 43.73) * mm});
            skLineSegment(sketch, "E519", {"start": v(-8.8, 43.73) * mm, "end": v(-8.82, 43.57) * mm});
            skLineSegment(sketch, "E520", {"start": v(-8.82, 43.57) * mm, "end": v(-8.85, 43.4) * mm});
            skLineSegment(sketch, "E521", {"start": v(-8.85, 43.4) * mm, "end": v(-6.35, 42.3) * mm});
            skLineSegment(sketch, "E522", {"start": v(-6.35, 42.3) * mm, "end": v(-6.25, 42.44) * mm});
            skLineSegment(sketch, "E523", {"start": v(-6.25, 42.44) * mm, "end": v(-6.15, 42.56) * mm});
            skLineSegment(sketch, "E524", {"start": v(-6.15, 42.56) * mm, "end": v(-5.94, 42.82) * mm});
            skLineSegment(sketch, "E525", {"start": v(-5.94, 42.82) * mm, "end": v(-5.5, 43.3) * mm});
            skLineSegment(sketch, "E526", {"start": v(-5.5, 43.3) * mm, "end": v(-5.02, 43.78) * mm});
            skLineSegment(sketch, "E527", {"start": v(-5.02, 43.78) * mm, "end": v(-4.52, 44.24) * mm});
            skLineSegment(sketch, "E528", {"start": v(-4.52, 44.24) * mm, "end": v(-4, 44.69) * mm});
            skLineSegment(sketch, "E529", {"start": v(-4, 44.69) * mm, "end": v(-3.44, 45.12) * mm});
            skLineSegment(sketch, "E530", {"start": v(-3.44, 45.12) * mm, "end": v(-1.26, 43.92) * mm});
            skLineSegment(sketch, "E531", {"start": v(-1.26, 43.92) * mm, "end": v(-1.33, 43.22) * mm});
            skLineSegment(sketch, "E532", {"start": v(-1.33, 43.22) * mm, "end": v(-1.42, 42.54) * mm});
            skLineSegment(sketch, "E533", {"start": v(-1.42, 42.54) * mm, "end": v(-1.54, 41.87) * mm});
            skLineSegment(sketch, "E534", {"start": v(-1.54, 41.87) * mm, "end": v(-1.69, 41.21) * mm});
            skLineSegment(sketch, "E535", {"start": v(-1.69, 41.21) * mm, "end": v(-1.86, 40.57) * mm});
            skLineSegment(sketch, "E536", {"start": v(-1.86, 40.57) * mm, "end": v(-1.96, 40.26) * mm});
            skLineSegment(sketch, "E537", {"start": v(-1.96, 40.26) * mm, "end": v(-2.02, 40.1) * mm});
            skLineSegment(sketch, "E538", {"start": v(-2.02, 40.1) * mm, "end": v(-2.07, 39.96) * mm});
            skLineSegment(sketch, "E539", {"start": v(-2.07, 39.96) * mm, "end": v(0.2, 38.44) * mm});
            skLineSegment(sketch, "E540", {"start": v(0.2, 38.44) * mm, "end": v(0.31, 38.55) * mm});
            skLineSegment(sketch, "E541", {"start": v(0.31, 38.55) * mm, "end": v(0.44, 38.66) * mm});
            skLineSegment(sketch, "E542", {"start": v(0.44, 38.66) * mm, "end": v(0.69, 38.87) * mm});
            skLineSegment(sketch, "E543", {"start": v(0.69, 38.87) * mm, "end": v(1.2, 39.27) * mm});
            skLineSegment(sketch, "E544", {"start": v(1.2, 39.27) * mm, "end": v(1.76, 39.66) * mm});
            skLineSegment(sketch, "E545", {"start": v(1.76, 39.66) * mm, "end": v(2.33, 40.02) * mm});
            skLineSegment(sketch, "E546", {"start": v(2.33, 40.02) * mm, "end": v(2.93, 40.37) * mm});
            skLineSegment(sketch, "E547", {"start": v(2.93, 40.37) * mm, "end": v(3.55, 40.7) * mm});
            skLineSegment(sketch, "E548", {"start": v(3.55, 40.7) * mm, "end": v(5.49, 39.14) * mm});
            skLineSegment(sketch, "E549", {"start": v(5.49, 39.14) * mm, "end": v(5.3, 38.47) * mm});
            skLineSegment(sketch, "E550", {"start": v(5.3, 38.47) * mm, "end": v(5.09, 37.8) * mm});
            skLineSegment(sketch, "E551", {"start": v(5.09, 37.8) * mm, "end": v(4.85, 37.17) * mm});
            skLineSegment(sketch, "E552", {"start": v(4.85, 37.17) * mm, "end": v(4.6, 36.55) * mm});
            skLineSegment(sketch, "E553", {"start": v(4.6, 36.55) * mm, "end": v(4.31, 35.95) * mm});
            skLineSegment(sketch, "E554", {"start": v(4.31, 35.95) * mm, "end": v(4.16, 35.66) * mm});
            skLineSegment(sketch, "E555", {"start": v(4.16, 35.66) * mm, "end": v(4.08, 35.52) * mm});
            skLineSegment(sketch, "E556", {"start": v(4.08, 35.52) * mm, "end": v(4, 35.38) * mm});
            skLineSegment(sketch, "E557", {"start": v(4, 35.38) * mm, "end": v(5.97, 33.49) * mm});
            skLineSegment(sketch, "E558", {"start": v(5.97, 33.49) * mm, "end": v(6.1, 33.58) * mm});
            skLineSegment(sketch, "E559", {"start": v(6.1, 33.58) * mm, "end": v(6.24, 33.66) * mm});
            skLineSegment(sketch, "E560", {"start": v(6.24, 33.66) * mm, "end": v(6.53, 33.83) * mm});
            skLineSegment(sketch, "E561", {"start": v(6.53, 33.83) * mm, "end": v(7.11, 34.14) * mm});
            skLineSegment(sketch, "E562", {"start": v(7.11, 34.14) * mm, "end": v(7.72, 34.42) * mm});
            skLineSegment(sketch, "E563", {"start": v(7.72, 34.42) * mm, "end": v(8.35, 34.68) * mm});
            skLineSegment(sketch, "E564", {"start": v(8.35, 34.68) * mm, "end": v(9, 34.92) * mm});
            skLineSegment(sketch, "E565", {"start": v(9, 34.92) * mm, "end": v(9.66, 35.14) * mm});
            skLineSegment(sketch, "E566", {"start": v(9.66, 35.14) * mm, "end": v(11.3, 33.26) * mm});
            skLineSegment(sketch, "E567", {"start": v(11.3, 33.26) * mm, "end": v(11, 32.63) * mm});
            skLineSegment(sketch, "E568", {"start": v(11, 32.63) * mm, "end": v(10.68, 32.02) * mm});
            skLineSegment(sketch, "E569", {"start": v(10.68, 32.02) * mm, "end": v(10.34, 31.43) * mm});
            skLineSegment(sketch, "E570", {"start": v(10.34, 31.43) * mm, "end": v(9.98, 30.87) * mm});
            skLineSegment(sketch, "E571", {"start": v(9.98, 30.87) * mm, "end": v(9.6, 30.33) * mm});
            skLineSegment(sketch, "E572", {"start": v(9.6, 30.33) * mm, "end": v(9.4, 30.07) * mm});
            skLineSegment(sketch, "E573", {"start": v(9.4, 30.07) * mm, "end": v(9.29, 29.94) * mm});
            skLineSegment(sketch, "E574", {"start": v(9.29, 29.94) * mm, "end": v(9.18, 29.82) * mm});
            skLineSegment(sketch, "E575", {"start": v(9.18, 29.82) * mm, "end": v(10.8, 27.61) * mm});
            skLineSegment(sketch, "E576", {"start": v(10.8, 27.61) * mm, "end": v(10.95, 27.68) * mm});
            skLineSegment(sketch, "E577", {"start": v(10.95, 27.68) * mm, "end": v(11.1, 27.74) * mm});
            skLineSegment(sketch, "E578", {"start": v(11.1, 27.74) * mm, "end": v(11.4, 27.85) * mm});
            skLineSegment(sketch, "E579", {"start": v(11.4, 27.85) * mm, "end": v(12.03, 28.05) * mm});
            skLineSegment(sketch, "E580", {"start": v(12.03, 28.05) * mm, "end": v(12.68, 28.23) * mm});
            skLineSegment(sketch, "E581", {"start": v(12.68, 28.23) * mm, "end": v(13.35, 28.37) * mm});
            skLineSegment(sketch, "E582", {"start": v(13.35, 28.37) * mm, "end": v(14.03, 28.5) * mm});
            skLineSegment(sketch, "E583", {"start": v(14.03, 28.5) * mm, "end": v(14.72, 28.6) * mm});
            skLineSegment(sketch, "E584", {"start": v(14.72, 28.6) * mm, "end": v(16.01, 26.46) * mm});
            skLineSegment(sketch, "E585", {"start": v(16.01, 26.46) * mm, "end": v(15.6, 25.9) * mm});
            skLineSegment(sketch, "E586", {"start": v(15.6, 25.9) * mm, "end": v(15.18, 25.35) * mm});
            skLineSegment(sketch, "E587", {"start": v(15.18, 25.35) * mm, "end": v(14.74, 24.83) * mm});
            skLineSegment(sketch, "E588", {"start": v(14.74, 24.83) * mm, "end": v(14.29, 24.33) * mm});
            skLineSegment(sketch, "E589", {"start": v(14.29, 24.33) * mm, "end": v(13.82, 23.87) * mm});
            skLineSegment(sketch, "E590", {"start": v(13.82, 23.87) * mm, "end": v(13.57, 23.65) * mm});
            skLineSegment(sketch, "E591", {"start": v(13.57, 23.65) * mm, "end": v(13.45, 23.54) * mm});
            skLineSegment(sketch, "E592", {"start": v(13.45, 23.54) * mm, "end": v(13.32, 23.44) * mm});
            skLineSegment(sketch, "E593", {"start": v(13.32, 23.44) * mm, "end": v(14.53, 20.99) * mm});
            skLineSegment(sketch, "E594", {"start": v(14.53, 20.99) * mm, "end": v(14.69, 21.03) * mm});
            skLineSegment(sketch, "E595", {"start": v(14.69, 21.03) * mm, "end": v(14.85, 21.06) * mm});
            skLineSegment(sketch, "E596", {"start": v(14.85, 21.06) * mm, "end": v(15.17, 21.12) * mm});
            skLineSegment(sketch, "E597", {"start": v(15.17, 21.12) * mm, "end": v(15.83, 21.2) * mm});
            skLineSegment(sketch, "E598", {"start": v(15.83, 21.2) * mm, "end": v(16.5, 21.26) * mm});
            skLineSegment(sketch, "E599", {"start": v(16.5, 21.26) * mm, "end": v(17.17, 21.3) * mm});
            skLineSegment(sketch, "E600", {"start": v(17.17, 21.3) * mm, "end": v(17.87, 21.3) * mm});
            skLineSegment(sketch, "E601", {"start": v(17.87, 21.3) * mm, "end": v(18.56, 21.27) * mm});
            skLineSegment(sketch, "E602", {"start": v(18.56, 21.27) * mm, "end": v(19.47, 18.95) * mm});
            skLineSegment(sketch, "E603", {"start": v(19.47, 18.95) * mm, "end": v(18.96, 18.46) * mm});
            skLineSegment(sketch, "E604", {"start": v(18.96, 18.46) * mm, "end": v(18.45, 18) * mm});
            skLineSegment(sketch, "E605", {"start": v(18.45, 18) * mm, "end": v(17.93, 17.56) * mm});
            skLineSegment(sketch, "E606", {"start": v(17.93, 17.56) * mm, "end": v(17.4, 17.15) * mm});
            skLineSegment(sketch, "E607", {"start": v(17.4, 17.15) * mm, "end": v(16.85, 16.78) * mm});
            skLineSegment(sketch, "E608", {"start": v(16.85, 16.78) * mm, "end": v(16.58, 16.6) * mm});
            skLineSegment(sketch, "E609", {"start": v(16.58, 16.6) * mm, "end": v(16.44, 16.52) * mm});
            skLineSegment(sketch, "E610", {"start": v(16.44, 16.52) * mm, "end": v(16.3, 16.44) * mm});
            skLineSegment(sketch, "E611", {"start": v(16.3, 16.44) * mm, "end": v(17.06, 13.82) * mm});
            skLineSegment(sketch, "E612", {"start": v(17.06, 13.82) * mm, "end": v(17.22, 13.82) * mm});
            skLineSegment(sketch, "E613", {"start": v(17.22, 13.82) * mm, "end": v(17.38, 13.83) * mm});
            skLineSegment(sketch, "E614", {"start": v(17.38, 13.83) * mm, "end": v(17.7, 13.83) * mm});
            skLineSegment(sketch, "E615", {"start": v(17.7, 13.83) * mm, "end": v(18.37, 13.8) * mm});
            skLineSegment(sketch, "E616", {"start": v(18.37, 13.8) * mm, "end": v(19.04, 13.75) * mm});
            skLineSegment(sketch, "E617", {"start": v(19.04, 13.75) * mm, "end": v(19.71, 13.66) * mm});
            skLineSegment(sketch, "E618", {"start": v(19.71, 13.66) * mm, "end": v(20.4, 13.54) * mm});
            skLineSegment(sketch, "E619", {"start": v(20.4, 13.54) * mm, "end": v(21.08, 13.4) * mm});
            skLineSegment(sketch, "E620", {"start": v(21.08, 13.4) * mm, "end": v(21.56, 10.95) * mm});
            skLineSegment(sketch, "E621", {"start": v(21.56, 10.95) * mm, "end": v(20.99, 10.56) * mm});
            skLineSegment(sketch, "E622", {"start": v(20.99, 10.56) * mm, "end": v(20.4, 10.2) * mm});
            skLineSegment(sketch, "E623", {"start": v(20.4, 10.2) * mm, "end": v(19.81, 9.85) * mm});
            skLineSegment(sketch, "E624", {"start": v(19.81, 9.85) * mm, "end": v(19.21, 9.54) * mm});
            skLineSegment(sketch, "E625", {"start": v(19.21, 9.54) * mm, "end": v(18.61, 9.27) * mm});
            skLineSegment(sketch, "E626", {"start": v(18.61, 9.27) * mm, "end": v(18.3, 9.14) * mm});
            skLineSegment(sketch, "E627", {"start": v(18.3, 9.14) * mm, "end": v(18.16, 9.08) * mm});
            skLineSegment(sketch, "E628", {"start": v(18.16, 9.08) * mm, "end": v(18, 9.03) * mm});
            skLineSegment(sketch, "E629", {"start": v(18, 9.03) * mm, "end": v(18.3, 6.32) * mm});
            skLineSegment(sketch, "E630", {"start": v(18.3, 6.32) * mm, "end": v(18.46, 6.3) * mm});
            skLineSegment(sketch, "E631", {"start": v(18.46, 6.3) * mm, "end": v(18.62, 6.27) * mm});
            skLineSegment(sketch, "E632", {"start": v(18.62, 6.27) * mm, "end": v(18.94, 6.22) * mm});
            skLineSegment(sketch, "E633", {"start": v(18.94, 6.22) * mm, "end": v(19.6, 6.08) * mm});
            skLineSegment(sketch, "E634", {"start": v(19.6, 6.08) * mm, "end": v(20.24, 5.9) * mm});
            skLineSegment(sketch, "E635", {"start": v(20.24, 5.9) * mm, "end": v(20.89, 5.7) * mm});
            skLineSegment(sketch, "E636", {"start": v(20.89, 5.7) * mm, "end": v(21.54, 5.46) * mm});
            skLineSegment(sketch, "E637", {"start": v(21.54, 5.46) * mm, "end": v(22.19, 5.2) * mm});
            skLineSegment(sketch, "E638", {"start": v(22.19, 5.2) * mm, "end": v(22.24, 2.71) * mm});
            skLineSegment(sketch, "E639", {"start": v(22.24, 2.71) * mm, "end": v(21.6, 2.42) * mm});
            skLineSegment(sketch, "E640", {"start": v(21.6, 2.42) * mm, "end": v(20.96, 2.16) * mm});
            skLineSegment(sketch, "E641", {"start": v(20.96, 2.16) * mm, "end": v(20.32, 1.93) * mm});
            skLineSegment(sketch, "E642", {"start": v(20.32, 1.93) * mm, "end": v(19.68, 1.73) * mm});
            skLineSegment(sketch, "E643", {"start": v(19.68, 1.73) * mm, "end": v(19.04, 1.56) * mm});
            skLineSegment(sketch, "E644", {"start": v(19.04, 1.56) * mm, "end": v(18.72, 1.5) * mm});
            skLineSegment(sketch, "E645", {"start": v(18.72, 1.5) * mm, "end": v(18.56, 1.46) * mm});
            skLineSegment(sketch, "E646", {"start": v(18.56, 1.46) * mm, "end": v(18.4, 1.44) * mm});
            skLineSegment(sketch, "E647", {"start": v(18.4, 1.44) * mm, "end": v(18.22, -1.29) * mm});
            skLineSegment(sketch, "E648", {"start": v(-15.2, 4.3) * mm, "end": v(12.62, -0.01) * mm});
            skLineSegment(sketch, "E649", {"start": v(12.62, -0.01) * mm, "end": v(14.12, 1.2) * mm});
            skLineSegment(sketch, "E650", {"start": v(14.12, 1.2) * mm, "end": v(14.15, 3.92) * mm});
            skLineSegment(sketch, "E651", {"start": v(14.15, 3.92) * mm, "end": v(13.99, 6.64) * mm});
            skLineSegment(sketch, "E652", {"start": v(13.99, 6.64) * mm, "end": v(13.64, 9.35) * mm});
            skLineSegment(sketch, "E653", {"start": v(13.64, 9.35) * mm, "end": v(13.1, 12.02) * mm});
            skLineSegment(sketch, "E654", {"start": v(13.1, 12.02) * mm, "end": v(12.38, 14.65) * mm});
            skLineSegment(sketch, "E655", {"start": v(12.38, 14.65) * mm, "end": v(11.48, 17.22) * mm});
            skLineSegment(sketch, "E656", {"start": v(11.48, 17.22) * mm, "end": v(10.4, 19.73) * mm});
            skLineSegment(sketch, "E657", {"start": v(10.4, 19.73) * mm, "end": v(9.16, 22.15) * mm});
            skLineSegment(sketch, "E658", {"start": v(9.16, 22.15) * mm, "end": v(7.75, 24.49) * mm});
            skLineSegment(sketch, "E659", {"start": v(7.75, 24.49) * mm, "end": v(6.18, 26.72) * mm});
            skLineSegment(sketch, "E660", {"start": v(6.18, 26.72) * mm, "end": v(4.46, 28.83) * mm});
            skLineSegment(sketch, "E661", {"start": v(4.46, 28.83) * mm, "end": v(2.6, 30.82) * mm});
            skLineSegment(sketch, "E662", {"start": v(2.6, 30.82) * mm, "end": v(0.6, 32.68) * mm});
            skLineSegment(sketch, "E663", {"start": v(0.6, 32.68) * mm, "end": v(-1.51, 34.4) * mm});
            skLineSegment(sketch, "E664", {"start": v(-1.51, 34.4) * mm, "end": v(-3.75, 35.96) * mm});
            skLineSegment(sketch, "E665", {"start": v(-3.75, 35.96) * mm, "end": v(-5.6, 35.45) * mm});
            skLineSegment(sketch, "E666", {"start": v(-5.6, 35.45) * mm, "end": v(-18.3, 10.31) * mm});
            skLineSegment(sketch, "E667", {"start": v(-18.3, 10.31) * mm, "end": v(-17.95, 7.83) * mm});
            skLineSegment(sketch, "E668", {"start": v(-17.95, 7.83) * mm, "end": v(-17.02, 6.02) * mm});
            skLineSegment(sketch, "E669", {"start": v(-17.02, 6.02) * mm, "end": v(-15.2, 4.3) * mm});
            skLineSegment(sketch, "E670", {"start": v(-23.38, 12.88) * mm, "end": v(-10.68, 38.01) * mm});
            skLineSegment(sketch, "E671", {"start": v(-10.68, 38.01) * mm, "end": v(-11.37, 39.8) * mm});
            skLineSegment(sketch, "E672", {"start": v(-11.37, 39.8) * mm, "end": v(-13.95, 40.68) * mm});
            skLineSegment(sketch, "E673", {"start": v(-13.95, 40.68) * mm, "end": v(-16.59, 41.37) * mm});
            skLineSegment(sketch, "E674", {"start": v(-16.59, 41.37) * mm, "end": v(-19.27, 41.87) * mm});
            skLineSegment(sketch, "E675", {"start": v(-19.27, 41.87) * mm, "end": v(-21.98, 42.19) * mm});
            skLineSegment(sketch, "E676", {"start": v(-21.98, 42.19) * mm, "end": v(-24.7, 42.32) * mm});
            skLineSegment(sketch, "E677", {"start": v(-24.7, 42.32) * mm, "end": v(-27.42, 42.26) * mm});
            skLineSegment(sketch, "E678", {"start": v(-27.42, 42.26) * mm, "end": v(-30.14, 42) * mm});
            skLineSegment(sketch, "E679", {"start": v(-30.14, 42) * mm, "end": v(-32.83, 41.57) * mm});
            skLineSegment(sketch, "E680", {"start": v(-32.83, 41.57) * mm, "end": v(-35.48, 40.95) * mm});
            skLineSegment(sketch, "E681", {"start": v(-35.48, 40.95) * mm, "end": v(-38.09, 40.15) * mm});
            skLineSegment(sketch, "E682", {"start": v(-38.09, 40.15) * mm, "end": v(-40.63, 39.16) * mm});
            skLineSegment(sketch, "E683", {"start": v(-40.63, 39.16) * mm, "end": v(-43.1, 38) * mm});
            skLineSegment(sketch, "E684", {"start": v(-43.1, 38) * mm, "end": v(-45.48, 36.69) * mm});
            skLineSegment(sketch, "E685", {"start": v(-45.48, 36.69) * mm, "end": v(-47.77, 35.2) * mm});
            skLineSegment(sketch, "E686", {"start": v(-47.77, 35.2) * mm, "end": v(-49.95, 33.56) * mm});
            skLineSegment(sketch, "E687", {"start": v(-49.95, 33.56) * mm, "end": v(-50.03, 31.64) * mm});
            skLineSegment(sketch, "E688", {"start": v(-50.03, 31.64) * mm, "end": v(-30.05, 11.8) * mm});
            skLineSegment(sketch, "E689", {"start": v(-30.05, 11.8) * mm, "end": v(-27.59, 11.35) * mm});
            skLineSegment(sketch, "E690", {"start": v(-27.59, 11.35) * mm, "end": v(-25.58, 11.68) * mm});
            skLineSegment(sketch, "E691", {"start": v(-25.58, 11.68) * mm, "end": v(-23.38, 12.88) * mm});
            skLineSegment(sketch, "E692", {"start": v(-34.06, 7.76) * mm, "end": v(-54.04, 27.6) * mm});
            skLineSegment(sketch, "E693", {"start": v(-54.04, 27.6) * mm, "end": v(-55.96, 27.5) * mm});
            skLineSegment(sketch, "E694", {"start": v(-55.96, 27.5) * mm, "end": v(-57.59, 25.31) * mm});
            skLineSegment(sketch, "E695", {"start": v(-57.59, 25.31) * mm, "end": v(-59.06, 23.02) * mm});
            skLineSegment(sketch, "E696", {"start": v(-59.06, 23.02) * mm, "end": v(-60.37, 20.62) * mm});
            skLineSegment(sketch, "E697", {"start": v(-60.37, 20.62) * mm, "end": v(-61.5, 18.15) * mm});
            skLineSegment(sketch, "E698", {"start": v(-61.5, 18.15) * mm, "end": v(-62.47, 15.6) * mm});
            skLineSegment(sketch, "E699", {"start": v(-62.47, 15.6) * mm, "end": v(-63.25, 12.99) * mm});
            skLineSegment(sketch, "E700", {"start": v(-63.25, 12.99) * mm, "end": v(-63.86, 10.33) * mm});
            skLineSegment(sketch, "E701", {"start": v(-63.86, 10.33) * mm, "end": v(-64.27, 7.63) * mm});
            skLineSegment(sketch, "E702", {"start": v(-64.27, 7.63) * mm, "end": v(-64.5, 4.92) * mm});
            skLineSegment(sketch, "E703", {"start": v(-64.5, 4.92) * mm, "end": v(-64.54, 2.2) * mm});
            skLineSegment(sketch, "E704", {"start": v(-64.54, 2.2) * mm, "end": v(-64.4, -0.53) * mm});
            skLineSegment(sketch, "E705", {"start": v(-64.4, -0.53) * mm, "end": v(-64.06, -3.24) * mm});
            skLineSegment(sketch, "E706", {"start": v(-64.06, -3.24) * mm, "end": v(-63.54, -5.91) * mm});
            skLineSegment(sketch, "E707", {"start": v(-63.54, -5.91) * mm, "end": v(-62.83, -8.54) * mm});
            skLineSegment(sketch, "E708", {"start": v(-62.83, -8.54) * mm, "end": v(-61.94, -11.12) * mm});
            skLineSegment(sketch, "E709", {"start": v(-61.94, -11.12) * mm, "end": v(-60.14, -11.8) * mm});
            skLineSegment(sketch, "E710", {"start": v(-60.14, -11.8) * mm, "end": v(-35.1, 1.07) * mm});
            skLineSegment(sketch, "E711", {"start": v(-35.1, 1.07) * mm, "end": v(-33.91, 3.28) * mm});
            skLineSegment(sketch, "E712", {"start": v(-33.91, 3.28) * mm, "end": v(-33.6, 5.3) * mm});
            skLineSegment(sketch, "E713", {"start": v(-33.6, 5.3) * mm, "end": v(-34.06, 7.76) * mm});
            skLineSegment(sketch, "E714", {"start": v(-32.5, -3.99) * mm, "end": v(-57.54, -16.86) * mm});
            skLineSegment(sketch, "E715", {"start": v(-57.54, -16.86) * mm, "end": v(-58.04, -18.72) * mm});
            skLineSegment(sketch, "E716", {"start": v(-58.04, -18.72) * mm, "end": v(-56.46, -20.94) * mm});
            skLineSegment(sketch, "E717", {"start": v(-56.46, -20.94) * mm, "end": v(-54.73, -23.04) * mm});
            skLineSegment(sketch, "E718", {"start": v(-54.73, -23.04) * mm, "end": v(-52.86, -25.03) * mm});
            skLineSegment(sketch, "E719", {"start": v(-52.86, -25.03) * mm, "end": v(-50.86, -26.88) * mm});
            skLineSegment(sketch, "E720", {"start": v(-50.86, -26.88) * mm, "end": v(-48.73, -28.58) * mm});
            skLineSegment(sketch, "E721", {"start": v(-48.73, -28.58) * mm, "end": v(-46.49, -30.13) * mm});
            skLineSegment(sketch, "E722", {"start": v(-46.49, -30.13) * mm, "end": v(-44.15, -31.53) * mm});
            skLineSegment(sketch, "E723", {"start": v(-44.15, -31.53) * mm, "end": v(-41.71, -32.76) * mm});
            skLineSegment(sketch, "E724", {"start": v(-41.71, -32.76) * mm, "end": v(-39.2, -33.81) * mm});
            skLineSegment(sketch, "E725", {"start": v(-39.2, -33.81) * mm, "end": v(-36.62, -34.7) * mm});
            skLineSegment(sketch, "E726", {"start": v(-36.62, -34.7) * mm, "end": v(-33.99, -35.4) * mm});
            skLineSegment(sketch, "E727", {"start": v(-33.99, -35.4) * mm, "end": v(-31.3, -35.91) * mm});
            skLineSegment(sketch, "E728", {"start": v(-31.3, -35.91) * mm, "end": v(-28.6, -36.24) * mm});
            skLineSegment(sketch, "E729", {"start": v(-28.6, -36.24) * mm, "end": v(-25.88, -36.38) * mm});
            skLineSegment(sketch, "E730", {"start": v(-25.88, -36.38) * mm, "end": v(-23.16, -36.34) * mm});
            skLineSegment(sketch, "E731", {"start": v(-23.16, -36.34) * mm, "end": v(-21.96, -34.83) * mm});
            skLineSegment(sketch, "E732", {"start": v(-21.96, -34.83) * mm, "end": v(-26.46, -7.04) * mm});
            skLineSegment(sketch, "E733", {"start": v(-26.46, -7.04) * mm, "end": v(-28.2, -5.23) * mm});
            skLineSegment(sketch, "E734", {"start": v(-28.2, -5.23) * mm, "end": v(-30.01, -4.31) * mm});
            skLineSegment(sketch, "E735", {"start": v(-30.01, -4.31) * mm, "end": v(-32.5, -3.99) * mm});
            skLineSegment(sketch, "E736", {"start": v(-20.84, -6.13) * mm, "end": v(-16.34, -33.92) * mm});
            skLineSegment(sketch, "E737", {"start": v(-16.34, -33.92) * mm, "end": v(-14.73, -34.97) * mm});
            skLineSegment(sketch, "E738", {"start": v(-14.73, -34.97) * mm, "end": v(-12.13, -34.16) * mm});
            skLineSegment(sketch, "E739", {"start": v(-12.13, -34.16) * mm, "end": v(-9.59, -33.16) * mm});
            skLineSegment(sketch, "E740", {"start": v(-9.59, -33.16) * mm, "end": v(-7.12, -32) * mm});
            skLineSegment(sketch, "E741", {"start": v(-7.12, -32) * mm, "end": v(-4.75, -30.66) * mm});
            skLineSegment(sketch, "E742", {"start": v(-4.75, -30.66) * mm, "end": v(-2.47, -29.16) * mm});
            skLineSegment(sketch, "E743", {"start": v(-2.47, -29.16) * mm, "end": v(-0.3, -27.51) * mm});
            skLineSegment(sketch, "E744", {"start": v(-0.3, -27.51) * mm, "end": v(1.75, -25.72) * mm});
            skLineSegment(sketch, "E745", {"start": v(1.75, -25.72) * mm, "end": v(3.67, -23.78) * mm});
            skLineSegment(sketch, "E746", {"start": v(3.67, -23.78) * mm, "end": v(5.46, -21.72) * mm});
            skLineSegment(sketch, "E747", {"start": v(5.46, -21.72) * mm, "end": v(7.1, -19.54) * mm});
            skLineSegment(sketch, "E748", {"start": v(7.1, -19.54) * mm, "end": v(8.57, -17.25) * mm});
            skLineSegment(sketch, "E749", {"start": v(8.57, -17.25) * mm, "end": v(9.89, -14.86) * mm});
            skLineSegment(sketch, "E750", {"start": v(9.89, -14.86) * mm, "end": v(11.04, -12.4) * mm});
            skLineSegment(sketch, "E751", {"start": v(11.04, -12.4) * mm, "end": v(12.02, -9.85) * mm});
            skLineSegment(sketch, "E752", {"start": v(12.02, -9.85) * mm, "end": v(12.81, -7.24) * mm});
            skLineSegment(sketch, "E753", {"start": v(12.81, -7.24) * mm, "end": v(11.75, -5.64) * mm});
            skLineSegment(sketch, "E754", {"start": v(11.75, -5.64) * mm, "end": v(-16.07, -1.33) * mm});
            skLineSegment(sketch, "E755", {"start": v(-16.07, -1.33) * mm, "end": v(-18.33, -2.42) * mm});
            skLineSegment(sketch, "E756", {"start": v(-18.33, -2.42) * mm, "end": v(-19.76, -3.86) * mm});
            skLineSegment(sketch, "E757", {"start": v(-19.76, -3.86) * mm, "end": v(-20.84, -6.13) * mm});
            skCircle(sketch, "E758", {"center": v(-25.2, 2.96) * mm, "radius": 1.27 * mm});
            skLineSegment(sketch, "E759", {"start": v(23.2, -1.98) * mm, "end": v(23.07, -1.84) * mm});
            skLineSegment(sketch, "E760", {"start": v(23.07, -1.84) * mm, "end": v(22.99, -1.8) * mm});
            skLineSegment(sketch, "E761", {"start": v(22.99, -1.8) * mm, "end": v(22.91, -1.77) * mm});
            skLineSegment(sketch, "E762", {"start": v(22.91, -1.77) * mm, "end": v(22.84, -1.76) * mm});
            skLineSegment(sketch, "E763", {"start": v(22.84, -1.76) * mm, "end": v(22.77, -1.75) * mm});
            skLineSegment(sketch, "E764", {"start": v(22.77, -1.75) * mm, "end": v(22.63, -1.75) * mm});
            skLineSegment(sketch, "E765", {"start": v(22.63, -1.75) * mm, "end": v(22.5, -1.76) * mm});
            skLineSegment(sketch, "E766", {"start": v(22.5, -1.76) * mm, "end": v(22.37, -1.78) * mm});
            skLineSegment(sketch, "E767", {"start": v(22.37, -1.78) * mm, "end": v(22.25, -1.8) * mm});
            skLineSegment(sketch, "E768", {"start": v(22.25, -1.8) * mm, "end": v(22, -1.88) * mm});
            skLineSegment(sketch, "E769", {"start": v(22, -1.88) * mm, "end": v(21.75, -1.92) * mm});
            skLineSegment(sketch, "E770", {"start": v(21.75, -1.92) * mm, "end": v(21.49, -1.95) * mm});
            skLineSegment(sketch, "E771", {"start": v(21.49, -1.95) * mm, "end": v(21.22, -1.95) * mm});
            skLineSegment(sketch, "E772", {"start": v(21.22, -1.95) * mm, "end": v(20.95, -1.94) * mm});
            skLineSegment(sketch, "E773", {"start": v(20.95, -1.94) * mm, "end": v(20.67, -1.92) * mm});
            skLineSegment(sketch, "E774", {"start": v(20.67, -1.92) * mm, "end": v(20.4, -1.89) * mm});
            skLineSegment(sketch, "E775", {"start": v(20.4, -1.89) * mm, "end": v(20.11, -1.84) * mm});
            skLineSegment(sketch, "E776", {"start": v(20.11, -1.84) * mm, "end": v(19.83, -1.78) * mm});
            skLineSegment(sketch, "E777", {"start": v(19.83, -1.78) * mm, "end": v(19.54, -1.71) * mm});
            skLineSegment(sketch, "E778", {"start": v(19.54, -1.71) * mm, "end": v(19.26, -1.63) * mm});
            skLineSegment(sketch, "E779", {"start": v(19.26, -1.63) * mm, "end": v(19.04, -1.57) * mm});
            skLineSegment(sketch, "E780", {"start": v(19.04, -1.57) * mm, "end": v(18.57, 0.76) * mm});
            skLineSegment(sketch, "E781", {"start": v(18.57, 0.76) * mm, "end": v(18.74, 0.9) * mm});
            skLineSegment(sketch, "E782", {"start": v(18.74, 0.9) * mm, "end": v(18.98, 1.09) * mm});
            skLineSegment(sketch, "E783", {"start": v(18.98, 1.09) * mm, "end": v(19.22, 1.26) * mm});
            skLineSegment(sketch, "E784", {"start": v(19.22, 1.26) * mm, "end": v(19.45, 1.43) * mm});
            skLineSegment(sketch, "E785", {"start": v(19.45, 1.43) * mm, "end": v(19.7, 1.58) * mm});
            skLineSegment(sketch, "E786", {"start": v(19.7, 1.58) * mm, "end": v(19.94, 1.72) * mm});
            skLineSegment(sketch, "E787", {"start": v(19.94, 1.72) * mm, "end": v(20.18, 1.85) * mm});
            skLineSegment(sketch, "E788", {"start": v(20.18, 1.85) * mm, "end": v(20.43, 1.96) * mm});
            skLineSegment(sketch, "E789", {"start": v(20.43, 1.96) * mm, "end": v(20.68, 2.06) * mm});
            skLineSegment(sketch, "E790", {"start": v(20.68, 2.06) * mm, "end": v(20.93, 2.14) * mm});
            skLineSegment(sketch, "E791", {"start": v(20.93, 2.14) * mm, "end": v(21.18, 2.2) * mm});
            skLineSegment(sketch, "E792", {"start": v(21.18, 2.2) * mm, "end": v(21.43, 2.22) * mm});
            skLineSegment(sketch, "E793", {"start": v(21.43, 2.22) * mm, "end": v(21.56, 2.24) * mm});
            skLineSegment(sketch, "E794", {"start": v(21.56, 2.24) * mm, "end": v(21.69, 2.27) * mm});
            skLineSegment(sketch, "E795", {"start": v(21.69, 2.27) * mm, "end": v(21.81, 2.31) * mm});
            skLineSegment(sketch, "E796", {"start": v(21.81, 2.31) * mm, "end": v(21.94, 2.37) * mm});
            skLineSegment(sketch, "E797", {"start": v(21.94, 2.37) * mm, "end": v(22, 2.4) * mm});
            skLineSegment(sketch, "E798", {"start": v(22, 2.4) * mm, "end": v(22.06, 2.44) * mm});
            skLineSegment(sketch, "E799", {"start": v(22.06, 2.44) * mm, "end": v(22.12, 2.5) * mm});
            skLineSegment(sketch, "E800", {"start": v(22.12, 2.5) * mm, "end": v(22.18, 2.57) * mm});
            skLineSegment(sketch, "E801", {"start": v(22.18, 2.57) * mm, "end": v(22.24, 2.75) * mm});
            skLineSegment(sketch, "E802", {"start": v(22.24, 2.75) * mm, "end": v(22.27, 3.8) * mm});
            skLineSegment(sketch, "E803", {"start": v(22.27, 3.8) * mm, "end": v(22.37, 4.84) * mm});
            skLineSegment(sketch, "E804", {"start": v(22.37, 4.84) * mm, "end": v(22.34, 5.03) * mm});
            skLineSegment(sketch, "E805", {"start": v(22.34, 5.03) * mm, "end": v(22.29, 5.1) * mm});
            skLineSegment(sketch, "E806", {"start": v(22.29, 5.1) * mm, "end": v(22.23, 5.16) * mm});
            skLineSegment(sketch, "E807", {"start": v(22.23, 5.16) * mm, "end": v(22.17, 5.21) * mm});
            skLineSegment(sketch, "E808", {"start": v(22.17, 5.21) * mm, "end": v(22.12, 5.26) * mm});
            skLineSegment(sketch, "E809", {"start": v(22.12, 5.26) * mm, "end": v(22, 5.32) * mm});
            skLineSegment(sketch, "E810", {"start": v(22, 5.32) * mm, "end": v(21.88, 5.38) * mm});
            skLineSegment(sketch, "E811", {"start": v(21.88, 5.38) * mm, "end": v(21.76, 5.43) * mm});
            skLineSegment(sketch, "E812", {"start": v(21.76, 5.43) * mm, "end": v(21.64, 5.46) * mm});
            skLineSegment(sketch, "E813", {"start": v(21.64, 5.46) * mm, "end": v(21.4, 5.52) * mm});
            skLineSegment(sketch, "E814", {"start": v(21.4, 5.52) * mm, "end": v(21.15, 5.61) * mm});
            skLineSegment(sketch, "E815", {"start": v(21.15, 5.61) * mm, "end": v(20.91, 5.72) * mm});
            skLineSegment(sketch, "E816", {"start": v(20.91, 5.72) * mm, "end": v(20.68, 5.85) * mm});
            skLineSegment(sketch, "E817", {"start": v(20.68, 5.85) * mm, "end": v(20.45, 6) * mm});
            skLineSegment(sketch, "E818", {"start": v(20.45, 6) * mm, "end": v(20.22, 6.15) * mm});
            skLineSegment(sketch, "E819", {"start": v(20.22, 6.15) * mm, "end": v(20, 6.32) * mm});
            skLineSegment(sketch, "E820", {"start": v(20, 6.32) * mm, "end": v(19.77, 6.5) * mm});
            skLineSegment(sketch, "E821", {"start": v(19.77, 6.5) * mm, "end": v(19.56, 6.7) * mm});
            skLineSegment(sketch, "E822", {"start": v(19.56, 6.7) * mm, "end": v(19.34, 6.9) * mm});
            skLineSegment(sketch, "E823", {"start": v(19.34, 6.9) * mm, "end": v(19.14, 7.11) * mm});
            skLineSegment(sketch, "E824", {"start": v(19.14, 7.11) * mm, "end": v(18.98, 7.28) * mm});
            skLineSegment(sketch, "E825", {"start": v(18.98, 7.28) * mm, "end": v(19.74, 9.52) * mm});
            skLineSegment(sketch, "E826", {"start": v(19.74, 9.52) * mm, "end": v(19.96, 9.56) * mm});
            skLineSegment(sketch, "E827", {"start": v(19.96, 9.56) * mm, "end": v(20.26, 9.6) * mm});
            skLineSegment(sketch, "E828", {"start": v(20.26, 9.6) * mm, "end": v(20.55, 9.64) * mm});
            skLineSegment(sketch, "E829", {"start": v(20.55, 9.64) * mm, "end": v(20.84, 9.66) * mm});
            skLineSegment(sketch, "E830", {"start": v(20.84, 9.66) * mm, "end": v(21.12, 9.67) * mm});
            skLineSegment(sketch, "E831", {"start": v(21.12, 9.67) * mm, "end": v(21.4, 9.67) * mm});
            skLineSegment(sketch, "E832", {"start": v(21.4, 9.67) * mm, "end": v(21.68, 9.66) * mm});
            skLineSegment(sketch, "E833", {"start": v(21.68, 9.66) * mm, "end": v(21.95, 9.63) * mm});
            skLineSegment(sketch, "E834", {"start": v(21.95, 9.63) * mm, "end": v(22.21, 9.6) * mm});
            skLineSegment(sketch, "E835", {"start": v(22.21, 9.6) * mm, "end": v(22.47, 9.54) * mm});
            skLineSegment(sketch, "E836", {"start": v(22.47, 9.54) * mm, "end": v(22.72, 9.46) * mm});
            skLineSegment(sketch, "E837", {"start": v(22.72, 9.46) * mm, "end": v(22.95, 9.36) * mm});
            skLineSegment(sketch, "E838", {"start": v(22.95, 9.36) * mm, "end": v(23.07, 9.32) * mm});
            skLineSegment(sketch, "E839", {"start": v(23.07, 9.32) * mm, "end": v(23.2, 9.28) * mm});
            skLineSegment(sketch, "E840", {"start": v(23.2, 9.28) * mm, "end": v(23.32, 9.25) * mm});
            skLineSegment(sketch, "E841", {"start": v(23.32, 9.25) * mm, "end": v(23.46, 9.24) * mm});
            skLineSegment(sketch, "E842", {"start": v(23.46, 9.24) * mm, "end": v(23.53, 9.23) * mm});
            skLineSegment(sketch, "E843", {"start": v(23.53, 9.23) * mm, "end": v(23.6, 9.24) * mm});
            skLineSegment(sketch, "E844", {"start": v(23.6, 9.24) * mm, "end": v(23.68, 9.25) * mm});
            skLineSegment(sketch, "E845", {"start": v(23.68, 9.25) * mm, "end": v(23.77, 9.29) * mm});
            skLineSegment(sketch, "E846", {"start": v(23.77, 9.29) * mm, "end": v(23.91, 9.41) * mm});
            skLineSegment(sketch, "E847", {"start": v(23.91, 9.41) * mm, "end": v(24.46, 10.3) * mm});
            skLineSegment(sketch, "E848", {"start": v(24.46, 10.3) * mm, "end": v(25.07, 11.15) * mm});
            skLineSegment(sketch, "E849", {"start": v(25.07, 11.15) * mm, "end": v(25.13, 11.34) * mm});
            skLineSegment(sketch, "E850", {"start": v(25.13, 11.34) * mm, "end": v(25.13, 11.43) * mm});
            skLineSegment(sketch, "E851", {"start": v(25.13, 11.43) * mm, "end": v(25.11, 11.5) * mm});
            skLineSegment(sketch, "E852", {"start": v(25.11, 11.5) * mm, "end": v(25.09, 11.58) * mm});
            skLineSegment(sketch, "E853", {"start": v(25.09, 11.58) * mm, "end": v(25.06, 11.64) * mm});
            skLineSegment(sketch, "E854", {"start": v(25.06, 11.64) * mm, "end": v(25, 11.76) * mm});
            skLineSegment(sketch, "E855", {"start": v(25, 11.76) * mm, "end": v(24.92, 11.87) * mm});
            skLineSegment(sketch, "E856", {"start": v(24.92, 11.87) * mm, "end": v(24.83, 11.97) * mm});
            skLineSegment(sketch, "E857", {"start": v(24.83, 11.97) * mm, "end": v(24.75, 12.06) * mm});
            skLineSegment(sketch, "E858", {"start": v(24.75, 12.06) * mm, "end": v(24.56, 12.24) * mm});
            skLineSegment(sketch, "E859", {"start": v(24.56, 12.24) * mm, "end": v(24.4, 12.44) * mm});
            skLineSegment(sketch, "E860", {"start": v(24.4, 12.44) * mm, "end": v(24.25, 12.65) * mm});
            skLineSegment(sketch, "E861", {"start": v(24.25, 12.65) * mm, "end": v(24.1, 12.88) * mm});
            skLineSegment(sketch, "E862", {"start": v(24.1, 12.88) * mm, "end": v(23.98, 13.12) * mm});
            skLineSegment(sketch, "E863", {"start": v(23.98, 13.12) * mm, "end": v(23.86, 13.37) * mm});
            skLineSegment(sketch, "E864", {"start": v(23.86, 13.37) * mm, "end": v(23.75, 13.63) * mm});
            skLineSegment(sketch, "E865", {"start": v(23.75, 13.63) * mm, "end": v(23.65, 13.9) * mm});
            skLineSegment(sketch, "E866", {"start": v(23.65, 13.9) * mm, "end": v(23.56, 14.17) * mm});
            skLineSegment(sketch, "E867", {"start": v(23.56, 14.17) * mm, "end": v(23.48, 14.45) * mm});
            skLineSegment(sketch, "E868", {"start": v(23.48, 14.45) * mm, "end": v(23.4, 14.74) * mm});
            skLineSegment(sketch, "E869", {"start": v(23.4, 14.74) * mm, "end": v(23.35, 14.96) * mm});
            skLineSegment(sketch, "E870", {"start": v(23.35, 14.96) * mm, "end": v(25.13, 16.53) * mm});
            skLineSegment(sketch, "E871", {"start": v(25.13, 16.53) * mm, "end": v(25.34, 16.45) * mm});
            skLineSegment(sketch, "E872", {"start": v(25.34, 16.45) * mm, "end": v(25.62, 16.34) * mm});
            skLineSegment(sketch, "E873", {"start": v(25.62, 16.34) * mm, "end": v(25.9, 16.23) * mm});
            skLineSegment(sketch, "E874", {"start": v(25.9, 16.23) * mm, "end": v(26.15, 16.1) * mm});
            skLineSegment(sketch, "E875", {"start": v(26.15, 16.1) * mm, "end": v(26.4, 15.97) * mm});
            skLineSegment(sketch, "E876", {"start": v(26.4, 15.97) * mm, "end": v(26.65, 15.83) * mm});
            skLineSegment(sketch, "E877", {"start": v(26.65, 15.83) * mm, "end": v(26.88, 15.68) * mm});
            skLineSegment(sketch, "E878", {"start": v(26.88, 15.68) * mm, "end": v(27.1, 15.52) * mm});
            skLineSegment(sketch, "E879", {"start": v(27.1, 15.52) * mm, "end": v(27.3, 15.35) * mm});
            skLineSegment(sketch, "E880", {"start": v(27.3, 15.35) * mm, "end": v(27.5, 15.18) * mm});
            skLineSegment(sketch, "E881", {"start": v(27.5, 15.18) * mm, "end": v(27.68, 14.99) * mm});
            skLineSegment(sketch, "E882", {"start": v(27.68, 14.99) * mm, "end": v(27.83, 14.78) * mm});
            skLineSegment(sketch, "E883", {"start": v(27.83, 14.78) * mm, "end": v(27.91, 14.69) * mm});
            skLineSegment(sketch, "E884", {"start": v(27.91, 14.69) * mm, "end": v(28, 14.6) * mm});
            skLineSegment(sketch, "E885", {"start": v(28, 14.6) * mm, "end": v(28.1, 14.5) * mm});
            skLineSegment(sketch, "E886", {"start": v(28.1, 14.5) * mm, "end": v(28.2, 14.42) * mm});
            skLineSegment(sketch, "E887", {"start": v(28.2, 14.42) * mm, "end": v(28.27, 14.39) * mm});
            skLineSegment(sketch, "E888", {"start": v(28.27, 14.39) * mm, "end": v(28.34, 14.35) * mm});
            skLineSegment(sketch, "E889", {"start": v(28.34, 14.35) * mm, "end": v(28.41, 14.33) * mm});
            skLineSegment(sketch, "E890", {"start": v(28.41, 14.33) * mm, "end": v(28.5, 14.3) * mm});
            skLineSegment(sketch, "E891", {"start": v(28.5, 14.3) * mm, "end": v(28.7, 14.35) * mm});
            skLineSegment(sketch, "E892", {"start": v(28.7, 14.35) * mm, "end": v(29.61, 14.85) * mm});
            skLineSegment(sketch, "E893", {"start": v(29.61, 14.85) * mm, "end": v(30.57, 15.28) * mm});
            skLineSegment(sketch, "E894", {"start": v(30.57, 15.28) * mm, "end": v(30.71, 15.4) * mm});
            skLineSegment(sketch, "E895", {"start": v(30.71, 15.4) * mm, "end": v(30.75, 15.49) * mm});
            skLineSegment(sketch, "E896", {"start": v(30.75, 15.49) * mm, "end": v(30.78, 15.56) * mm});
            skLineSegment(sketch, "E897", {"start": v(30.78, 15.56) * mm, "end": v(30.8, 15.64) * mm});
            skLineSegment(sketch, "E898", {"start": v(30.8, 15.64) * mm, "end": v(30.8, 15.7) * mm});
            skLineSegment(sketch, "E899", {"start": v(30.8, 15.7) * mm, "end": v(30.8, 15.84) * mm});
            skLineSegment(sketch, "E900", {"start": v(30.8, 15.84) * mm, "end": v(30.79, 15.98) * mm});
            skLineSegment(sketch, "E901", {"start": v(30.79, 15.98) * mm, "end": v(30.77, 16.1) * mm});
            skLineSegment(sketch, "E902", {"start": v(30.77, 16.1) * mm, "end": v(30.74, 16.23) * mm});
            skLineSegment(sketch, "E903", {"start": v(30.74, 16.23) * mm, "end": v(30.67, 16.47) * mm});
            skLineSegment(sketch, "E904", {"start": v(30.67, 16.47) * mm, "end": v(30.62, 16.73) * mm});
            skLineSegment(sketch, "E905", {"start": v(30.62, 16.73) * mm, "end": v(30.6, 16.99) * mm});
            skLineSegment(sketch, "E906", {"start": v(30.6, 16.99) * mm, "end": v(30.6, 17.25) * mm});
            skLineSegment(sketch, "E907", {"start": v(30.6, 17.25) * mm, "end": v(30.6, 17.53) * mm});
            skLineSegment(sketch, "E908", {"start": v(30.6, 17.53) * mm, "end": v(30.63, 17.8) * mm});
            skLineSegment(sketch, "E909", {"start": v(30.63, 17.8) * mm, "end": v(30.66, 18.08) * mm});
            skLineSegment(sketch, "E910", {"start": v(30.66, 18.08) * mm, "end": v(30.7, 18.36) * mm});
            skLineSegment(sketch, "E911", {"start": v(30.7, 18.36) * mm, "end": v(30.76, 18.65) * mm});
            skLineSegment(sketch, "E912", {"start": v(30.76, 18.65) * mm, "end": v(30.83, 18.93) * mm});
            skLineSegment(sketch, "E913", {"start": v(30.83, 18.93) * mm, "end": v(30.91, 19.22) * mm});
            skLineSegment(sketch, "E914", {"start": v(30.91, 19.22) * mm, "end": v(30.98, 19.44) * mm});
            skLineSegment(sketch, "E915", {"start": v(30.98, 19.44) * mm, "end": v(33.3, 19.9) * mm});
            skLineSegment(sketch, "E916", {"start": v(33.3, 19.9) * mm, "end": v(33.45, 19.73) * mm});
            skLineSegment(sketch, "E917", {"start": v(33.45, 19.73) * mm, "end": v(33.64, 19.5) * mm});
            skLineSegment(sketch, "E918", {"start": v(33.64, 19.5) * mm, "end": v(33.81, 19.26) * mm});
            skLineSegment(sketch, "E919", {"start": v(33.81, 19.26) * mm, "end": v(33.97, 19.02) * mm});
            skLineSegment(sketch, "E920", {"start": v(33.97, 19.02) * mm, "end": v(34.13, 18.78) * mm});
            skLineSegment(sketch, "E921", {"start": v(34.13, 18.78) * mm, "end": v(34.27, 18.54) * mm});
            skLineSegment(sketch, "E922", {"start": v(34.27, 18.54) * mm, "end": v(34.4, 18.3) * mm});
            skLineSegment(sketch, "E923", {"start": v(34.4, 18.3) * mm, "end": v(34.5, 18.04) * mm});
            skLineSegment(sketch, "E924", {"start": v(34.5, 18.04) * mm, "end": v(34.6, 17.8) * mm});
            skLineSegment(sketch, "E925", {"start": v(34.6, 17.8) * mm, "end": v(34.68, 17.54) * mm});
            skLineSegment(sketch, "E926", {"start": v(34.68, 17.54) * mm, "end": v(34.74, 17.3) * mm});
            skLineSegment(sketch, "E927", {"start": v(34.74, 17.3) * mm, "end": v(34.77, 17.04) * mm});
            skLineSegment(sketch, "E928", {"start": v(34.77, 17.04) * mm, "end": v(34.8, 16.91) * mm});
            skLineSegment(sketch, "E929", {"start": v(34.8, 16.91) * mm, "end": v(34.82, 16.79) * mm});
            skLineSegment(sketch, "E930", {"start": v(34.82, 16.79) * mm, "end": v(34.86, 16.66) * mm});
            skLineSegment(sketch, "E931", {"start": v(34.86, 16.66) * mm, "end": v(34.92, 16.54) * mm});
            skLineSegment(sketch, "E932", {"start": v(34.92, 16.54) * mm, "end": v(34.95, 16.48) * mm});
            skLineSegment(sketch, "E933", {"start": v(34.95, 16.48) * mm, "end": v(35, 16.41) * mm});
            skLineSegment(sketch, "E934", {"start": v(35, 16.41) * mm, "end": v(35.04, 16.35) * mm});
            skLineSegment(sketch, "E935", {"start": v(35.04, 16.35) * mm, "end": v(35.12, 16.3) * mm});
            skLineSegment(sketch, "E936", {"start": v(35.12, 16.3) * mm, "end": v(35.3, 16.23) * mm});
            skLineSegment(sketch, "E937", {"start": v(35.3, 16.23) * mm, "end": v(36.34, 16.2) * mm});
            skLineSegment(sketch, "E938", {"start": v(36.34, 16.2) * mm, "end": v(37.38, 16.1) * mm});
            skLineSegment(sketch, "E939", {"start": v(37.38, 16.1) * mm, "end": v(37.57, 16.14) * mm});
            skLineSegment(sketch, "E940", {"start": v(37.57, 16.14) * mm, "end": v(37.65, 16.19) * mm});
            skLineSegment(sketch, "E941", {"start": v(37.65, 16.19) * mm, "end": v(37.71, 16.24) * mm});
            skLineSegment(sketch, "E942", {"start": v(37.71, 16.24) * mm, "end": v(37.76, 16.3) * mm});
            skLineSegment(sketch, "E943", {"start": v(37.76, 16.3) * mm, "end": v(37.8, 16.36) * mm});
            skLineSegment(sketch, "E944", {"start": v(37.8, 16.36) * mm, "end": v(37.87, 16.47) * mm});
            skLineSegment(sketch, "E945", {"start": v(37.87, 16.47) * mm, "end": v(37.93, 16.6) * mm});
            skLineSegment(sketch, "E946", {"start": v(37.93, 16.6) * mm, "end": v(37.97, 16.71) * mm});
            skLineSegment(sketch, "E947", {"start": v(37.97, 16.71) * mm, "end": v(38.01, 16.84) * mm});
            skLineSegment(sketch, "E948", {"start": v(38.01, 16.84) * mm, "end": v(38.07, 17.08) * mm});
            skLineSegment(sketch, "E949", {"start": v(38.07, 17.08) * mm, "end": v(38.16, 17.33) * mm});
            skLineSegment(sketch, "E950", {"start": v(38.16, 17.33) * mm, "end": v(38.27, 17.56) * mm});
            skLineSegment(sketch, "E951", {"start": v(38.27, 17.56) * mm, "end": v(38.4, 17.8) * mm});
            skLineSegment(sketch, "E952", {"start": v(38.4, 17.8) * mm, "end": v(38.54, 18.03) * mm});
            skLineSegment(sketch, "E953", {"start": v(38.54, 18.03) * mm, "end": v(38.7, 18.26) * mm});
            skLineSegment(sketch, "E954", {"start": v(38.7, 18.26) * mm, "end": v(38.87, 18.48) * mm});
            skLineSegment(sketch, "E955", {"start": v(38.87, 18.48) * mm, "end": v(39.05, 18.7) * mm});
            skLineSegment(sketch, "E956", {"start": v(39.05, 18.7) * mm, "end": v(39.24, 18.92) * mm});
            skLineSegment(sketch, "E957", {"start": v(39.24, 18.92) * mm, "end": v(39.44, 19.13) * mm});
            skLineSegment(sketch, "E958", {"start": v(39.44, 19.13) * mm, "end": v(39.66, 19.34) * mm});
            skLineSegment(sketch, "E959", {"start": v(39.66, 19.34) * mm, "end": v(39.82, 19.5) * mm});
            skLineSegment(sketch, "E960", {"start": v(39.82, 19.5) * mm, "end": v(42.07, 18.74) * mm});
            skLineSegment(sketch, "E961", {"start": v(42.07, 18.74) * mm, "end": v(42.1, 18.51) * mm});
            skLineSegment(sketch, "E962", {"start": v(42.1, 18.51) * mm, "end": v(42.15, 18.22) * mm});
            skLineSegment(sketch, "E963", {"start": v(42.15, 18.22) * mm, "end": v(42.19, 17.93) * mm});
            skLineSegment(sketch, "E964", {"start": v(42.19, 17.93) * mm, "end": v(42.2, 17.64) * mm});
            skLineSegment(sketch, "E965", {"start": v(42.2, 17.64) * mm, "end": v(42.22, 17.35) * mm});
            skLineSegment(sketch, "E966", {"start": v(42.22, 17.35) * mm, "end": v(42.22, 17.07) * mm});
            skLineSegment(sketch, "E967", {"start": v(42.22, 17.07) * mm, "end": v(42.2, 16.8) * mm});
            skLineSegment(sketch, "E968", {"start": v(42.2, 16.8) * mm, "end": v(42.18, 16.53) * mm});
            skLineSegment(sketch, "E969", {"start": v(42.18, 16.53) * mm, "end": v(42.14, 16.26) * mm});
            skLineSegment(sketch, "E970", {"start": v(42.14, 16.26) * mm, "end": v(42.09, 16) * mm});
            skLineSegment(sketch, "E971", {"start": v(42.09, 16) * mm, "end": v(42.01, 15.76) * mm});
            skLineSegment(sketch, "E972", {"start": v(42.01, 15.76) * mm, "end": v(41.9, 15.52) * mm});
            skLineSegment(sketch, "E973", {"start": v(41.9, 15.52) * mm, "end": v(41.86, 15.4) * mm});
            skLineSegment(sketch, "E974", {"start": v(41.86, 15.4) * mm, "end": v(41.83, 15.28) * mm});
            skLineSegment(sketch, "E975", {"start": v(41.83, 15.28) * mm, "end": v(41.8, 15.15) * mm});
            skLineSegment(sketch, "E976", {"start": v(41.8, 15.15) * mm, "end": v(41.78, 15.02) * mm});
            skLineSegment(sketch, "E977", {"start": v(41.78, 15.02) * mm, "end": v(41.78, 14.95) * mm});
            skLineSegment(sketch, "E978", {"start": v(41.78, 14.95) * mm, "end": v(41.79, 14.87) * mm});
            skLineSegment(sketch, "E979", {"start": v(41.79, 14.87) * mm, "end": v(41.8, 14.8) * mm});
            skLineSegment(sketch, "E980", {"start": v(41.8, 14.8) * mm, "end": v(41.83, 14.7) * mm});
            skLineSegment(sketch, "E981", {"start": v(41.83, 14.7) * mm, "end": v(41.96, 14.56) * mm});
            skLineSegment(sketch, "E982", {"start": v(41.96, 14.56) * mm, "end": v(42.85, 14.02) * mm});
            skLineSegment(sketch, "E983", {"start": v(42.85, 14.02) * mm, "end": v(43.7, 13.4) * mm});
            skLineSegment(sketch, "E984", {"start": v(43.7, 13.4) * mm, "end": v(43.88, 13.34) * mm});
            skLineSegment(sketch, "E985", {"start": v(43.88, 13.34) * mm, "end": v(43.98, 13.35) * mm});
            skLineSegment(sketch, "E986", {"start": v(43.98, 13.35) * mm, "end": v(44.06, 13.36) * mm});
            skLineSegment(sketch, "E987", {"start": v(44.06, 13.36) * mm, "end": v(44.13, 13.39) * mm});
            skLineSegment(sketch, "E988", {"start": v(44.13, 13.39) * mm, "end": v(44.2, 13.42) * mm});
            skLineSegment(sketch, "E989", {"start": v(44.2, 13.42) * mm, "end": v(44.31, 13.48) * mm});
            skLineSegment(sketch, "E990", {"start": v(44.31, 13.48) * mm, "end": v(44.42, 13.56) * mm});
            skLineSegment(sketch, "E991", {"start": v(44.42, 13.56) * mm, "end": v(44.52, 13.64) * mm});
            skLineSegment(sketch, "E992", {"start": v(44.52, 13.64) * mm, "end": v(44.61, 13.73) * mm});
            skLineSegment(sketch, "E993", {"start": v(44.61, 13.73) * mm, "end": v(44.79, 13.91) * mm});
            skLineSegment(sketch, "E994", {"start": v(44.79, 13.91) * mm, "end": v(44.99, 14.08) * mm});
            skLineSegment(sketch, "E995", {"start": v(44.99, 14.08) * mm, "end": v(45.2, 14.23) * mm});
            skLineSegment(sketch, "E996", {"start": v(45.2, 14.23) * mm, "end": v(45.43, 14.37) * mm});
            skLineSegment(sketch, "E997", {"start": v(45.43, 14.37) * mm, "end": v(45.67, 14.5) * mm});
            skLineSegment(sketch, "E998", {"start": v(45.67, 14.5) * mm, "end": v(45.92, 14.61) * mm});
            skLineSegment(sketch, "E999", {"start": v(45.92, 14.61) * mm, "end": v(46.18, 14.72) * mm});
            skLineSegment(sketch, "E1000", {"start": v(46.18, 14.72) * mm, "end": v(46.44, 14.82) * mm});
            skLineSegment(sketch, "E1001", {"start": v(46.44, 14.82) * mm, "end": v(46.72, 14.92) * mm});
            skLineSegment(sketch, "E1002", {"start": v(46.72, 14.92) * mm, "end": v(47, 15) * mm});
            skLineSegment(sketch, "E1003", {"start": v(47, 15) * mm, "end": v(47.3, 15.07) * mm});
            skLineSegment(sketch, "E1004", {"start": v(47.3, 15.07) * mm, "end": v(47.51, 15.12) * mm});
            skLineSegment(sketch, "E1005", {"start": v(47.51, 15.12) * mm, "end": v(49.08, 13.35) * mm});
            skLineSegment(sketch, "E1006", {"start": v(49.08, 13.35) * mm, "end": v(49, 13.13) * mm});
            skLineSegment(sketch, "E1007", {"start": v(49, 13.13) * mm, "end": v(48.9, 12.85) * mm});
            skLineSegment(sketch, "E1008", {"start": v(48.9, 12.85) * mm, "end": v(48.77, 12.58) * mm});
            skLineSegment(sketch, "E1009", {"start": v(48.77, 12.58) * mm, "end": v(48.65, 12.32) * mm});
            skLineSegment(sketch, "E1010", {"start": v(48.65, 12.32) * mm, "end": v(48.52, 12.07) * mm});
            skLineSegment(sketch, "E1011", {"start": v(48.52, 12.07) * mm, "end": v(48.37, 11.83) * mm});
            skLineSegment(sketch, "E1012", {"start": v(48.37, 11.83) * mm, "end": v(48.23, 11.6) * mm});
            skLineSegment(sketch, "E1013", {"start": v(48.23, 11.6) * mm, "end": v(48.07, 11.37) * mm});
            skLineSegment(sketch, "E1014", {"start": v(48.07, 11.37) * mm, "end": v(47.9, 11.17) * mm});
            skLineSegment(sketch, "E1015", {"start": v(47.9, 11.17) * mm, "end": v(47.73, 10.97) * mm});
            skLineSegment(sketch, "E1016", {"start": v(47.73, 10.97) * mm, "end": v(47.54, 10.8) * mm});
            skLineSegment(sketch, "E1017", {"start": v(47.54, 10.8) * mm, "end": v(47.33, 10.64) * mm});
            skLineSegment(sketch, "E1018", {"start": v(47.33, 10.64) * mm, "end": v(47.23, 10.56) * mm});
            skLineSegment(sketch, "E1019", {"start": v(47.23, 10.56) * mm, "end": v(47.14, 10.47) * mm});
            skLineSegment(sketch, "E1020", {"start": v(47.14, 10.47) * mm, "end": v(47.05, 10.38) * mm});
            skLineSegment(sketch, "E1021", {"start": v(47.05, 10.38) * mm, "end": v(46.97, 10.27) * mm});
            skLineSegment(sketch, "E1022", {"start": v(46.97, 10.27) * mm, "end": v(46.93, 10.2) * mm});
            skLineSegment(sketch, "E1023", {"start": v(46.93, 10.2) * mm, "end": v(46.9, 10.14) * mm});
            skLineSegment(sketch, "E1024", {"start": v(46.9, 10.14) * mm, "end": v(46.87, 10.06) * mm});
            skLineSegment(sketch, "E1025", {"start": v(46.87, 10.06) * mm, "end": v(46.86, 9.97) * mm});
            skLineSegment(sketch, "E1026", {"start": v(46.86, 9.97) * mm, "end": v(46.9, 9.78) * mm});
            skLineSegment(sketch, "E1027", {"start": v(46.9, 9.78) * mm, "end": v(47.4, 8.86) * mm});
            skLineSegment(sketch, "E1028", {"start": v(47.4, 8.86) * mm, "end": v(47.83, 7.9) * mm});
            skLineSegment(sketch, "E1029", {"start": v(47.83, 7.9) * mm, "end": v(47.95, 7.76) * mm});
            skLineSegment(sketch, "E1030", {"start": v(47.95, 7.76) * mm, "end": v(48.04, 7.72) * mm});
            skLineSegment(sketch, "E1031", {"start": v(48.04, 7.72) * mm, "end": v(48.11, 7.7) * mm});
            skLineSegment(sketch, "E1032", {"start": v(48.11, 7.7) * mm, "end": v(48.19, 7.68) * mm});
            skLineSegment(sketch, "E1033", {"start": v(48.19, 7.68) * mm, "end": v(48.26, 7.68) * mm});
            skLineSegment(sketch, "E1034", {"start": v(48.26, 7.68) * mm, "end": v(48.4, 7.67) * mm});
            skLineSegment(sketch, "E1035", {"start": v(48.4, 7.67) * mm, "end": v(48.52, 7.69) * mm});
            skLineSegment(sketch, "E1036", {"start": v(48.52, 7.69) * mm, "end": v(48.65, 7.7) * mm});
            skLineSegment(sketch, "E1037", {"start": v(48.65, 7.7) * mm, "end": v(48.78, 7.74) * mm});
            skLineSegment(sketch, "E1038", {"start": v(48.78, 7.74) * mm, "end": v(49.02, 7.8) * mm});
            skLineSegment(sketch, "E1039", {"start": v(49.02, 7.8) * mm, "end": v(49.27, 7.85) * mm});
            skLineSegment(sketch, "E1040", {"start": v(49.27, 7.85) * mm, "end": v(49.54, 7.87) * mm});
            skLineSegment(sketch, "E1041", {"start": v(49.54, 7.87) * mm, "end": v(49.8, 7.88) * mm});
            skLineSegment(sketch, "E1042", {"start": v(49.8, 7.88) * mm, "end": v(50.07, 7.87) * mm});
            skLineSegment(sketch, "E1043", {"start": v(50.07, 7.87) * mm, "end": v(50.35, 7.85) * mm});
            skLineSegment(sketch, "E1044", {"start": v(50.35, 7.85) * mm, "end": v(50.63, 7.82) * mm});
            skLineSegment(sketch, "E1045", {"start": v(50.63, 7.82) * mm, "end": v(50.9, 7.77) * mm});
            skLineSegment(sketch, "E1046", {"start": v(50.9, 7.77) * mm, "end": v(51.2, 7.71) * mm});
            skLineSegment(sketch, "E1047", {"start": v(51.2, 7.71) * mm, "end": v(51.48, 7.64) * mm});
            skLineSegment(sketch, "E1048", {"start": v(51.48, 7.64) * mm, "end": v(51.77, 7.56) * mm});
            skLineSegment(sketch, "E1049", {"start": v(51.77, 7.56) * mm, "end": v(51.98, 7.5) * mm});
            skLineSegment(sketch, "E1050", {"start": v(51.98, 7.5) * mm, "end": v(52.45, 5.17) * mm});
            skLineSegment(sketch, "E1051", {"start": v(52.45, 5.17) * mm, "end": v(52.28, 5.03) * mm});
            skLineSegment(sketch, "E1052", {"start": v(52.28, 5.03) * mm, "end": v(52.04, 4.84) * mm});
            skLineSegment(sketch, "E1053", {"start": v(52.04, 4.84) * mm, "end": v(51.8, 4.66) * mm});
            skLineSegment(sketch, "E1054", {"start": v(51.8, 4.66) * mm, "end": v(51.57, 4.5) * mm});
            skLineSegment(sketch, "E1055", {"start": v(51.57, 4.5) * mm, "end": v(51.33, 4.35) * mm});
            skLineSegment(sketch, "E1056", {"start": v(51.33, 4.35) * mm, "end": v(51.08, 4.2) * mm});
            skLineSegment(sketch, "E1057", {"start": v(51.08, 4.2) * mm, "end": v(50.84, 4.08) * mm});
            skLineSegment(sketch, "E1058", {"start": v(50.84, 4.08) * mm, "end": v(50.6, 3.97) * mm});
            skLineSegment(sketch, "E1059", {"start": v(50.6, 3.97) * mm, "end": v(50.34, 3.87) * mm});
            skLineSegment(sketch, "E1060", {"start": v(50.34, 3.87) * mm, "end": v(50.1, 3.8) * mm});
            skLineSegment(sketch, "E1061", {"start": v(50.1, 3.8) * mm, "end": v(49.84, 3.73) * mm});
            skLineSegment(sketch, "E1062", {"start": v(49.84, 3.73) * mm, "end": v(49.59, 3.7) * mm});
            skLineSegment(sketch, "E1063", {"start": v(49.59, 3.7) * mm, "end": v(49.46, 3.68) * mm});
            skLineSegment(sketch, "E1064", {"start": v(49.46, 3.68) * mm, "end": v(49.34, 3.65) * mm});
            skLineSegment(sketch, "E1065", {"start": v(49.34, 3.65) * mm, "end": v(49.21, 3.61) * mm});
            skLineSegment(sketch, "E1066", {"start": v(49.21, 3.61) * mm, "end": v(49.09, 3.56) * mm});
            skLineSegment(sketch, "E1067", {"start": v(49.09, 3.56) * mm, "end": v(49.02, 3.52) * mm});
            skLineSegment(sketch, "E1068", {"start": v(49.02, 3.52) * mm, "end": v(48.96, 3.48) * mm});
            skLineSegment(sketch, "E1069", {"start": v(48.96, 3.48) * mm, "end": v(48.9, 3.43) * mm});
            skLineSegment(sketch, "E1070", {"start": v(48.9, 3.43) * mm, "end": v(48.84, 3.36) * mm});
            skLineSegment(sketch, "E1071", {"start": v(48.84, 3.36) * mm, "end": v(48.78, 3.18) * mm});
            skLineSegment(sketch, "E1072", {"start": v(48.78, 3.18) * mm, "end": v(48.76, 2.13) * mm});
            skLineSegment(sketch, "E1073", {"start": v(48.76, 2.13) * mm, "end": v(48.65, 1.1) * mm});
            skLineSegment(sketch, "E1074", {"start": v(48.65, 1.1) * mm, "end": v(48.68, 0.9) * mm});
            skLineSegment(sketch, "E1075", {"start": v(48.68, 0.9) * mm, "end": v(48.74, 0.82) * mm});
            skLineSegment(sketch, "E1076", {"start": v(48.74, 0.82) * mm, "end": v(48.8, 0.76) * mm});
            skLineSegment(sketch, "E1077", {"start": v(48.8, 0.76) * mm, "end": v(48.85, 0.71) * mm});
            skLineSegment(sketch, "E1078", {"start": v(48.85, 0.71) * mm, "end": v(48.9, 0.67) * mm});
            skLineSegment(sketch, "E1079", {"start": v(48.9, 0.67) * mm, "end": v(49.02, 0.6) * mm});
            skLineSegment(sketch, "E1080", {"start": v(49.02, 0.6) * mm, "end": v(49.14, 0.55) * mm});
            skLineSegment(sketch, "E1081", {"start": v(49.14, 0.55) * mm, "end": v(49.26, 0.5) * mm});
            skLineSegment(sketch, "E1082", {"start": v(49.26, 0.5) * mm, "end": v(49.38, 0.46) * mm});
            skLineSegment(sketch, "E1083", {"start": v(49.38, 0.46) * mm, "end": v(49.63, 0.4) * mm});
            skLineSegment(sketch, "E1084", {"start": v(49.63, 0.4) * mm, "end": v(49.87, 0.32) * mm});
            skLineSegment(sketch, "E1085", {"start": v(49.87, 0.32) * mm, "end": v(50.11, 0.2) * mm});
            skLineSegment(sketch, "E1086", {"start": v(50.11, 0.2) * mm, "end": v(50.35, 0.08) * mm});
            skLineSegment(sketch, "E1087", {"start": v(50.35, 0.08) * mm, "end": v(50.58, -0.07) * mm});
            skLineSegment(sketch, "E1088", {"start": v(50.58, -0.07) * mm, "end": v(50.8, -0.22) * mm});
            skLineSegment(sketch, "E1089", {"start": v(50.8, -0.22) * mm, "end": v(51.03, -0.4) * mm});
            skLineSegment(sketch, "E1090", {"start": v(51.03, -0.4) * mm, "end": v(51.25, -0.57) * mm});
            skLineSegment(sketch, "E1091", {"start": v(51.25, -0.57) * mm, "end": v(51.47, -0.77) * mm});
            skLineSegment(sketch, "E1092", {"start": v(51.47, -0.77) * mm, "end": v(51.68, -0.97) * mm});
            skLineSegment(sketch, "E1093", {"start": v(51.68, -0.97) * mm, "end": v(51.89, -1.18) * mm});
            skLineSegment(sketch, "E1094", {"start": v(51.89, -1.18) * mm, "end": v(52.04, -1.35) * mm});
            skLineSegment(sketch, "E1095", {"start": v(52.04, -1.35) * mm, "end": v(51.29, -3.6) * mm});
            skLineSegment(sketch, "E1096", {"start": v(51.29, -3.6) * mm, "end": v(51.06, -3.63) * mm});
            skLineSegment(sketch, "E1097", {"start": v(51.06, -3.63) * mm, "end": v(50.77, -3.68) * mm});
            skLineSegment(sketch, "E1098", {"start": v(50.77, -3.68) * mm, "end": v(50.47, -3.71) * mm});
            skLineSegment(sketch, "E1099", {"start": v(50.47, -3.71) * mm, "end": v(50.19, -3.73) * mm});
            skLineSegment(sketch, "E1100", {"start": v(50.19, -3.73) * mm, "end": v(49.9, -3.74) * mm});
            skLineSegment(sketch, "E1101", {"start": v(49.9, -3.74) * mm, "end": v(49.62, -3.74) * mm});
            skLineSegment(sketch, "E1102", {"start": v(49.62, -3.74) * mm, "end": v(49.34, -3.73) * mm});
            skLineSegment(sketch, "E1103", {"start": v(49.34, -3.73) * mm, "end": v(49.07, -3.7) * mm});
            skLineSegment(sketch, "E1104", {"start": v(49.07, -3.7) * mm, "end": v(48.8, -3.67) * mm});
            skLineSegment(sketch, "E1105", {"start": v(48.8, -3.67) * mm, "end": v(48.55, -3.61) * mm});
            skLineSegment(sketch, "E1106", {"start": v(48.55, -3.61) * mm, "end": v(48.3, -3.54) * mm});
            skLineSegment(sketch, "E1107", {"start": v(48.3, -3.54) * mm, "end": v(48.07, -3.43) * mm});
            skLineSegment(sketch, "E1108", {"start": v(48.07, -3.43) * mm, "end": v(47.95, -3.39) * mm});
            skLineSegment(sketch, "E1109", {"start": v(47.95, -3.39) * mm, "end": v(47.83, -3.35) * mm});
            skLineSegment(sketch, "E1110", {"start": v(47.83, -3.35) * mm, "end": v(47.7, -3.32) * mm});
            skLineSegment(sketch, "E1111", {"start": v(47.7, -3.32) * mm, "end": v(47.57, -3.3) * mm});
            skLineSegment(sketch, "E1112", {"start": v(47.57, -3.3) * mm, "end": v(47.5, -3.3) * mm});
            skLineSegment(sketch, "E1113", {"start": v(47.5, -3.3) * mm, "end": v(47.42, -3.31) * mm});
            skLineSegment(sketch, "E1114", {"start": v(47.42, -3.31) * mm, "end": v(47.34, -3.33) * mm});
            skLineSegment(sketch, "E1115", {"start": v(47.34, -3.33) * mm, "end": v(47.25, -3.36) * mm});
            skLineSegment(sketch, "E1116", {"start": v(47.25, -3.36) * mm, "end": v(47.1, -3.49) * mm});
            skLineSegment(sketch, "E1117", {"start": v(47.1, -3.49) * mm, "end": v(46.56, -4.38) * mm});
            skLineSegment(sketch, "E1118", {"start": v(46.56, -4.38) * mm, "end": v(45.95, -5.23) * mm});
            skLineSegment(sketch, "E1119", {"start": v(45.95, -5.23) * mm, "end": v(45.89, -5.4) * mm});
            skLineSegment(sketch, "E1120", {"start": v(45.89, -5.4) * mm, "end": v(45.9, -5.5) * mm});
            skLineSegment(sketch, "E1121", {"start": v(45.9, -5.5) * mm, "end": v(45.91, -5.58) * mm});
            skLineSegment(sketch, "E1122", {"start": v(45.91, -5.58) * mm, "end": v(45.94, -5.65) * mm});
            skLineSegment(sketch, "E1123", {"start": v(45.94, -5.65) * mm, "end": v(45.96, -5.72) * mm});
            skLineSegment(sketch, "E1124", {"start": v(45.96, -5.72) * mm, "end": v(46.03, -5.84) * mm});
            skLineSegment(sketch, "E1125", {"start": v(46.03, -5.84) * mm, "end": v(46.1, -5.94) * mm});
            skLineSegment(sketch, "E1126", {"start": v(46.1, -5.94) * mm, "end": v(46.19, -6.04) * mm});
            skLineSegment(sketch, "E1127", {"start": v(46.19, -6.04) * mm, "end": v(46.28, -6.14) * mm});
            skLineSegment(sketch, "E1128", {"start": v(46.28, -6.14) * mm, "end": v(46.46, -6.31) * mm});
            skLineSegment(sketch, "E1129", {"start": v(46.46, -6.31) * mm, "end": v(46.63, -6.51) * mm});
            skLineSegment(sketch, "E1130", {"start": v(46.63, -6.51) * mm, "end": v(46.78, -6.73) * mm});
            skLineSegment(sketch, "E1131", {"start": v(46.78, -6.73) * mm, "end": v(46.91, -6.95) * mm});
            skLineSegment(sketch, "E1132", {"start": v(46.91, -6.95) * mm, "end": v(47.04, -7.2) * mm});
            skLineSegment(sketch, "E1133", {"start": v(47.04, -7.2) * mm, "end": v(47.16, -7.44) * mm});
            skLineSegment(sketch, "E1134", {"start": v(47.16, -7.44) * mm, "end": v(47.27, -7.7) * mm});
            skLineSegment(sketch, "E1135", {"start": v(47.27, -7.7) * mm, "end": v(47.37, -7.97) * mm});
            skLineSegment(sketch, "E1136", {"start": v(47.37, -7.97) * mm, "end": v(47.46, -8.24) * mm});
            skLineSegment(sketch, "E1137", {"start": v(47.46, -8.24) * mm, "end": v(47.55, -8.53) * mm});
            skLineSegment(sketch, "E1138", {"start": v(47.55, -8.53) * mm, "end": v(47.62, -8.82) * mm});
            skLineSegment(sketch, "E1139", {"start": v(47.62, -8.82) * mm, "end": v(47.67, -9.04) * mm});
            skLineSegment(sketch, "E1140", {"start": v(47.67, -9.04) * mm, "end": v(45.9, -10.6) * mm});
            skLineSegment(sketch, "E1141", {"start": v(45.9, -10.6) * mm, "end": v(45.68, -10.53) * mm});
            skLineSegment(sketch, "E1142", {"start": v(45.68, -10.53) * mm, "end": v(45.4, -10.42) * mm});
            skLineSegment(sketch, "E1143", {"start": v(45.4, -10.42) * mm, "end": v(45.13, -10.3) * mm});
            skLineSegment(sketch, "E1144", {"start": v(45.13, -10.3) * mm, "end": v(44.87, -10.17) * mm});
            skLineSegment(sketch, "E1145", {"start": v(44.87, -10.17) * mm, "end": v(44.62, -10.04) * mm});
            skLineSegment(sketch, "E1146", {"start": v(44.62, -10.04) * mm, "end": v(44.38, -9.9) * mm});
            skLineSegment(sketch, "E1147", {"start": v(44.38, -9.9) * mm, "end": v(44.14, -9.75) * mm});
            skLineSegment(sketch, "E1148", {"start": v(44.14, -9.75) * mm, "end": v(43.92, -9.6) * mm});
            skLineSegment(sketch, "E1149", {"start": v(43.92, -9.6) * mm, "end": v(43.71, -9.43) * mm});
            skLineSegment(sketch, "E1150", {"start": v(43.71, -9.43) * mm, "end": v(43.52, -9.25) * mm});
            skLineSegment(sketch, "E1151", {"start": v(43.52, -9.25) * mm, "end": v(43.34, -9.06) * mm});
            skLineSegment(sketch, "E1152", {"start": v(43.34, -9.06) * mm, "end": v(43.2, -8.86) * mm});
            skLineSegment(sketch, "E1153", {"start": v(43.2, -8.86) * mm, "end": v(43.1, -8.76) * mm});
            skLineSegment(sketch, "E1154", {"start": v(43.1, -8.76) * mm, "end": v(43.02, -8.66) * mm});
            skLineSegment(sketch, "E1155", {"start": v(43.02, -8.66) * mm, "end": v(42.92, -8.58) * mm});
            skLineSegment(sketch, "E1156", {"start": v(42.92, -8.58) * mm, "end": v(42.81, -8.5) * mm});
            skLineSegment(sketch, "E1157", {"start": v(42.81, -8.5) * mm, "end": v(42.75, -8.46) * mm});
            skLineSegment(sketch, "E1158", {"start": v(42.75, -8.46) * mm, "end": v(42.69, -8.43) * mm});
            skLineSegment(sketch, "E1159", {"start": v(42.69, -8.43) * mm, "end": v(42.6, -8.4) * mm});
            skLineSegment(sketch, "E1160", {"start": v(42.6, -8.4) * mm, "end": v(42.52, -8.38) * mm});
            skLineSegment(sketch, "E1161", {"start": v(42.52, -8.38) * mm, "end": v(42.33, -8.42) * mm});
            skLineSegment(sketch, "E1162", {"start": v(42.33, -8.42) * mm, "end": v(41.41, -8.92) * mm});
            skLineSegment(sketch, "E1163", {"start": v(41.41, -8.92) * mm, "end": v(40.46, -9.35) * mm});
            skLineSegment(sketch, "E1164", {"start": v(40.46, -9.35) * mm, "end": v(40.31, -9.48) * mm});
            skLineSegment(sketch, "E1165", {"start": v(40.31, -9.48) * mm, "end": v(40.27, -9.56) * mm});
            skLineSegment(sketch, "E1166", {"start": v(40.27, -9.56) * mm, "end": v(40.25, -9.64) * mm});
            skLineSegment(sketch, "E1167", {"start": v(40.25, -9.64) * mm, "end": v(40.23, -9.71) * mm});
            skLineSegment(sketch, "E1168", {"start": v(40.23, -9.71) * mm, "end": v(40.22, -9.78) * mm});
            skLineSegment(sketch, "E1169", {"start": v(40.22, -9.78) * mm, "end": v(40.22, -9.92) * mm});
            skLineSegment(sketch, "E1170", {"start": v(40.22, -9.92) * mm, "end": v(40.23, -10.05) * mm});
            skLineSegment(sketch, "E1171", {"start": v(40.23, -10.05) * mm, "end": v(40.25, -10.18) * mm});
            skLineSegment(sketch, "E1172", {"start": v(40.25, -10.18) * mm, "end": v(40.28, -10.3) * mm});
            skLineSegment(sketch, "E1173", {"start": v(40.28, -10.3) * mm, "end": v(40.36, -10.54) * mm});
            skLineSegment(sketch, "E1174", {"start": v(40.36, -10.54) * mm, "end": v(40.4, -10.8) * mm});
            skLineSegment(sketch, "E1175", {"start": v(40.4, -10.8) * mm, "end": v(40.42, -11.06) * mm});
            skLineSegment(sketch, "E1176", {"start": v(40.42, -11.06) * mm, "end": v(40.43, -11.33) * mm});
            skLineSegment(sketch, "E1177", {"start": v(40.43, -11.33) * mm, "end": v(40.42, -11.6) * mm});
            skLineSegment(sketch, "E1178", {"start": v(40.42, -11.6) * mm, "end": v(40.4, -11.87) * mm});
            skLineSegment(sketch, "E1179", {"start": v(40.4, -11.87) * mm, "end": v(40.36, -12.15) * mm});
            skLineSegment(sketch, "E1180", {"start": v(40.36, -12.15) * mm, "end": v(40.32, -12.43) * mm});
            skLineSegment(sketch, "E1181", {"start": v(40.32, -12.43) * mm, "end": v(40.26, -12.72) * mm});
            skLineSegment(sketch, "E1182", {"start": v(40.26, -12.72) * mm, "end": v(40.19, -13) * mm});
            skLineSegment(sketch, "E1183", {"start": v(40.19, -13) * mm, "end": v(40.1, -13.3) * mm});
            skLineSegment(sketch, "E1184", {"start": v(40.1, -13.3) * mm, "end": v(40.04, -13.5) * mm});
            skLineSegment(sketch, "E1185", {"start": v(40.04, -13.5) * mm, "end": v(37.72, -13.98) * mm});
            skLineSegment(sketch, "E1186", {"start": v(37.72, -13.98) * mm, "end": v(37.57, -13.8) * mm});
            skLineSegment(sketch, "E1187", {"start": v(37.57, -13.8) * mm, "end": v(37.39, -13.57) * mm});
            skLineSegment(sketch, "E1188", {"start": v(37.39, -13.57) * mm, "end": v(37.21, -13.33) * mm});
            skLineSegment(sketch, "E1189", {"start": v(37.21, -13.33) * mm, "end": v(37.05, -13.1) * mm});
            skLineSegment(sketch, "E1190", {"start": v(37.05, -13.1) * mm, "end": v(36.9, -12.85) * mm});
            skLineSegment(sketch, "E1191", {"start": v(36.9, -12.85) * mm, "end": v(36.76, -12.6) * mm});
            skLineSegment(sketch, "E1192", {"start": v(36.76, -12.6) * mm, "end": v(36.63, -12.36) * mm});
            skLineSegment(sketch, "E1193", {"start": v(36.63, -12.36) * mm, "end": v(36.52, -12.12) * mm});
            skLineSegment(sketch, "E1194", {"start": v(36.52, -12.12) * mm, "end": v(36.42, -11.87) * mm});
            skLineSegment(sketch, "E1195", {"start": v(36.42, -11.87) * mm, "end": v(36.34, -11.62) * mm});
            skLineSegment(sketch, "E1196", {"start": v(36.34, -11.62) * mm, "end": v(36.28, -11.37) * mm});
            skLineSegment(sketch, "E1197", {"start": v(36.28, -11.37) * mm, "end": v(36.25, -11.11) * mm});
            skLineSegment(sketch, "E1198", {"start": v(36.25, -11.11) * mm, "end": v(36.23, -10.99) * mm});
            skLineSegment(sketch, "E1199", {"start": v(36.23, -10.99) * mm, "end": v(36.2, -10.86) * mm});
            skLineSegment(sketch, "E1200", {"start": v(36.2, -10.86) * mm, "end": v(36.16, -10.74) * mm});
            skLineSegment(sketch, "E1201", {"start": v(36.16, -10.74) * mm, "end": v(36.1, -10.61) * mm});
            skLineSegment(sketch, "E1202", {"start": v(36.1, -10.61) * mm, "end": v(36.07, -10.55) * mm});
            skLineSegment(sketch, "E1203", {"start": v(36.07, -10.55) * mm, "end": v(36.03, -10.49) * mm});
            skLineSegment(sketch, "E1204", {"start": v(36.03, -10.49) * mm, "end": v(35.98, -10.43) * mm});
            skLineSegment(sketch, "E1205", {"start": v(35.98, -10.43) * mm, "end": v(35.9, -10.36) * mm});
            skLineSegment(sketch, "E1206", {"start": v(35.9, -10.36) * mm, "end": v(35.72, -10.3) * mm});
            skLineSegment(sketch, "E1207", {"start": v(35.72, -10.3) * mm, "end": v(34.68, -10.28) * mm});
            skLineSegment(sketch, "E1208", {"start": v(34.68, -10.28) * mm, "end": v(33.64, -10.17) * mm});
            skLineSegment(sketch, "E1209", {"start": v(33.64, -10.17) * mm, "end": v(33.45, -10.2) * mm});
            skLineSegment(sketch, "E1210", {"start": v(33.45, -10.2) * mm, "end": v(33.37, -10.26) * mm});
            skLineSegment(sketch, "E1211", {"start": v(33.37, -10.26) * mm, "end": v(33.31, -10.32) * mm});
            skLineSegment(sketch, "E1212", {"start": v(33.31, -10.32) * mm, "end": v(33.26, -10.37) * mm});
            skLineSegment(sketch, "E1213", {"start": v(33.26, -10.37) * mm, "end": v(33.22, -10.43) * mm});
            skLineSegment(sketch, "E1214", {"start": v(33.22, -10.43) * mm, "end": v(33.15, -10.55) * mm});
            skLineSegment(sketch, "E1215", {"start": v(33.15, -10.55) * mm, "end": v(33.1, -10.67) * mm});
            skLineSegment(sketch, "E1216", {"start": v(33.1, -10.67) * mm, "end": v(33.05, -10.79) * mm});
            skLineSegment(sketch, "E1217", {"start": v(33.05, -10.79) * mm, "end": v(33.01, -10.9) * mm});
            skLineSegment(sketch, "E1218", {"start": v(33.01, -10.9) * mm, "end": v(32.95, -11.16) * mm});
            skLineSegment(sketch, "E1219", {"start": v(32.95, -11.16) * mm, "end": v(32.86, -11.4) * mm});
            skLineSegment(sketch, "E1220", {"start": v(32.86, -11.4) * mm, "end": v(32.75, -11.64) * mm});
            skLineSegment(sketch, "E1221", {"start": v(32.75, -11.64) * mm, "end": v(32.62, -11.87) * mm});
            skLineSegment(sketch, "E1222", {"start": v(32.62, -11.87) * mm, "end": v(32.48, -12.1) * mm});
            skLineSegment(sketch, "E1223", {"start": v(32.48, -12.1) * mm, "end": v(32.32, -12.33) * mm});
            skLineSegment(sketch, "E1224", {"start": v(32.32, -12.33) * mm, "end": v(32.15, -12.55) * mm});
            skLineSegment(sketch, "E1225", {"start": v(32.15, -12.55) * mm, "end": v(31.97, -12.77) * mm});
            skLineSegment(sketch, "E1226", {"start": v(31.97, -12.77) * mm, "end": v(31.78, -13) * mm});
            skLineSegment(sketch, "E1227", {"start": v(31.78, -13) * mm, "end": v(31.58, -13.2) * mm});
            skLineSegment(sketch, "E1228", {"start": v(31.58, -13.2) * mm, "end": v(31.36, -13.41) * mm});
            skLineSegment(sketch, "E1229", {"start": v(31.36, -13.41) * mm, "end": v(31.2, -13.57) * mm});
            skLineSegment(sketch, "E1230", {"start": v(31.2, -13.57) * mm, "end": v(28.95, -12.81) * mm});
            skLineSegment(sketch, "E1231", {"start": v(28.95, -12.81) * mm, "end": v(28.91, -12.59) * mm});
            skLineSegment(sketch, "E1232", {"start": v(28.91, -12.59) * mm, "end": v(28.87, -12.3) * mm});
            skLineSegment(sketch, "E1233", {"start": v(28.87, -12.3) * mm, "end": v(28.84, -12) * mm});
            skLineSegment(sketch, "E1234", {"start": v(28.84, -12) * mm, "end": v(28.81, -11.71) * mm});
            skLineSegment(sketch, "E1235", {"start": v(28.81, -11.71) * mm, "end": v(28.8, -11.43) * mm});
            skLineSegment(sketch, "E1236", {"start": v(28.8, -11.43) * mm, "end": v(28.8, -11.14) * mm});
            skLineSegment(sketch, "E1237", {"start": v(28.8, -11.14) * mm, "end": v(28.82, -10.87) * mm});
            skLineSegment(sketch, "E1238", {"start": v(28.82, -10.87) * mm, "end": v(28.84, -10.6) * mm});
            skLineSegment(sketch, "E1239", {"start": v(28.84, -10.6) * mm, "end": v(28.88, -10.33) * mm});
            skLineSegment(sketch, "E1240", {"start": v(28.88, -10.33) * mm, "end": v(28.94, -10.08) * mm});
            skLineSegment(sketch, "E1241", {"start": v(28.94, -10.08) * mm, "end": v(29.01, -9.83) * mm});
            skLineSegment(sketch, "E1242", {"start": v(29.01, -9.83) * mm, "end": v(29.11, -9.6) * mm});
            skLineSegment(sketch, "E1243", {"start": v(29.11, -9.6) * mm, "end": v(29.16, -9.48) * mm});
            skLineSegment(sketch, "E1244", {"start": v(29.16, -9.48) * mm, "end": v(29.2, -9.35) * mm});
            skLineSegment(sketch, "E1245", {"start": v(29.2, -9.35) * mm, "end": v(29.22, -9.23) * mm});
            skLineSegment(sketch, "E1246", {"start": v(29.22, -9.23) * mm, "end": v(29.24, -9.1) * mm});
            skLineSegment(sketch, "E1247", {"start": v(29.24, -9.1) * mm, "end": v(29.24, -9.02) * mm});
            skLineSegment(sketch, "E1248", {"start": v(29.24, -9.02) * mm, "end": v(29.23, -8.94) * mm});
            skLineSegment(sketch, "E1249", {"start": v(29.23, -8.94) * mm, "end": v(29.22, -8.86) * mm});
            skLineSegment(sketch, "E1250", {"start": v(29.22, -8.86) * mm, "end": v(29.19, -8.78) * mm});
            skLineSegment(sketch, "E1251", {"start": v(29.19, -8.78) * mm, "end": v(29.06, -8.63) * mm});
            skLineSegment(sketch, "E1252", {"start": v(29.06, -8.63) * mm, "end": v(28.17, -8.09) * mm});
            skLineSegment(sketch, "E1253", {"start": v(28.17, -8.09) * mm, "end": v(27.32, -7.48) * mm});
            skLineSegment(sketch, "E1254", {"start": v(27.32, -7.48) * mm, "end": v(27.14, -7.41) * mm});
            skLineSegment(sketch, "E1255", {"start": v(27.14, -7.41) * mm, "end": v(27.04, -7.42) * mm});
            skLineSegment(sketch, "E1256", {"start": v(27.04, -7.42) * mm, "end": v(26.97, -7.44) * mm});
            skLineSegment(sketch, "E1257", {"start": v(26.97, -7.44) * mm, "end": v(26.9, -7.46) * mm});
            skLineSegment(sketch, "E1258", {"start": v(26.9, -7.46) * mm, "end": v(26.83, -7.49) * mm});
            skLineSegment(sketch, "E1259", {"start": v(26.83, -7.49) * mm, "end": v(26.71, -7.56) * mm});
            skLineSegment(sketch, "E1260", {"start": v(26.71, -7.56) * mm, "end": v(26.6, -7.63) * mm});
            skLineSegment(sketch, "E1261", {"start": v(26.6, -7.63) * mm, "end": v(26.5, -7.71) * mm});
            skLineSegment(sketch, "E1262", {"start": v(26.5, -7.71) * mm, "end": v(26.41, -7.8) * mm});
            skLineSegment(sketch, "E1263", {"start": v(26.41, -7.8) * mm, "end": v(26.23, -7.99) * mm});
            skLineSegment(sketch, "E1264", {"start": v(26.23, -7.99) * mm, "end": v(26.04, -8.15) * mm});
            skLineSegment(sketch, "E1265", {"start": v(26.04, -8.15) * mm, "end": v(25.82, -8.3) * mm});
            skLineSegment(sketch, "E1266", {"start": v(25.82, -8.3) * mm, "end": v(25.6, -8.44) * mm});
            skLineSegment(sketch, "E1267", {"start": v(25.6, -8.44) * mm, "end": v(25.35, -8.57) * mm});
            skLineSegment(sketch, "E1268", {"start": v(25.35, -8.57) * mm, "end": v(25.1, -8.69) * mm});
            skLineSegment(sketch, "E1269", {"start": v(25.1, -8.69) * mm, "end": v(24.85, -8.8) * mm});
            skLineSegment(sketch, "E1270", {"start": v(24.85, -8.8) * mm, "end": v(24.58, -8.9) * mm});
            skLineSegment(sketch, "E1271", {"start": v(24.58, -8.9) * mm, "end": v(24.3, -8.99) * mm});
            skLineSegment(sketch, "E1272", {"start": v(24.3, -8.99) * mm, "end": v(24.02, -9.07) * mm});
            skLineSegment(sketch, "E1273", {"start": v(24.02, -9.07) * mm, "end": v(23.73, -9.14) * mm});
            skLineSegment(sketch, "E1274", {"start": v(23.73, -9.14) * mm, "end": v(23.51, -9.2) * mm});
            skLineSegment(sketch, "E1275", {"start": v(23.51, -9.2) * mm, "end": v(21.94, -7.42) * mm});
            skLineSegment(sketch, "E1276", {"start": v(21.94, -7.42) * mm, "end": v(22.02, -7.2) * mm});
            skLineSegment(sketch, "E1277", {"start": v(22.02, -7.2) * mm, "end": v(22.13, -6.93) * mm});
            skLineSegment(sketch, "E1278", {"start": v(22.13, -6.93) * mm, "end": v(22.25, -6.66) * mm});
            skLineSegment(sketch, "E1279", {"start": v(22.25, -6.66) * mm, "end": v(22.37, -6.4) * mm});
            skLineSegment(sketch, "E1280", {"start": v(22.37, -6.4) * mm, "end": v(22.5, -6.14) * mm});
            skLineSegment(sketch, "E1281", {"start": v(22.5, -6.14) * mm, "end": v(22.65, -5.9) * mm});
            skLineSegment(sketch, "E1282", {"start": v(22.65, -5.9) * mm, "end": v(22.8, -5.67) * mm});
            skLineSegment(sketch, "E1283", {"start": v(22.8, -5.67) * mm, "end": v(22.95, -5.45) * mm});
            skLineSegment(sketch, "E1284", {"start": v(22.95, -5.45) * mm, "end": v(23.12, -5.24) * mm});
            skLineSegment(sketch, "E1285", {"start": v(23.12, -5.24) * mm, "end": v(23.3, -5.04) * mm});
            skLineSegment(sketch, "E1286", {"start": v(23.3, -5.04) * mm, "end": v(23.49, -4.87) * mm});
            skLineSegment(sketch, "E1287", {"start": v(23.49, -4.87) * mm, "end": v(23.7, -4.72) * mm});
            skLineSegment(sketch, "E1288", {"start": v(23.7, -4.72) * mm, "end": v(23.79, -4.63) * mm});
            skLineSegment(sketch, "E1289", {"start": v(23.79, -4.63) * mm, "end": v(23.88, -4.55) * mm});
            skLineSegment(sketch, "E1290", {"start": v(23.88, -4.55) * mm, "end": v(23.97, -4.45) * mm});
            skLineSegment(sketch, "E1291", {"start": v(23.97, -4.45) * mm, "end": v(24.05, -4.34) * mm});
            skLineSegment(sketch, "E1292", {"start": v(24.05, -4.34) * mm, "end": v(24.09, -4.28) * mm});
            skLineSegment(sketch, "E1293", {"start": v(24.09, -4.28) * mm, "end": v(24.12, -4.21) * mm});
            skLineSegment(sketch, "E1294", {"start": v(24.12, -4.21) * mm, "end": v(24.15, -4.13) * mm});
            skLineSegment(sketch, "E1295", {"start": v(24.15, -4.13) * mm, "end": v(24.17, -4.04) * mm});
            skLineSegment(sketch, "E1296", {"start": v(24.17, -4.04) * mm, "end": v(24.13, -3.85) * mm});
            skLineSegment(sketch, "E1297", {"start": v(24.13, -3.85) * mm, "end": v(23.62, -2.94) * mm});
            skLineSegment(sketch, "E1298", {"start": v(23.62, -2.94) * mm, "end": v(23.2, -1.98) * mm});
            skCircle(sketch, "E1299", {"center": v(35.51, 2.96) * mm, "radius": 6.35 * mm});
            skSolve(sketch);
        }
        {
            var Q0;
            Q0=makeQuery(id+"F0.imprint","IMPRINT",FACE,{"disambiguationData":[TD([[makeQuery(id+"F0.imprint","IMPRINT",EDGE,{"derivedFrom":sQuery(id+"F0.wireOp",EDGE,"E0")}),-1.0]])]});
            extrude(context, id + "F1", {"entities" : qUnion([Q0]), "depth" : 2.54 * mm, "offsetDistance" : 25.4 * mm});
        }
        {
            var Q0;
            Q0=qCreatedBy(makeId("Top.planeOp"),FACE);
            var sketch = newSketch(context, id + "F2", { "sketchPlane" : qUnion([Q0])});
            skLineSegment(sketch, "E1300", {"start": v(-53.01, 6.12) * mm, "end": v(-52.59, 5.05) * mm});
            skLineSegment(sketch, "E1301", {"start": v(-52.59, 5.05) * mm, "end": v(-52.5, 4.99) * mm});
            skLineSegment(sketch, "E1302", {"start": v(-52.5, 4.99) * mm, "end": v(-52.43, 4.95) * mm});
            skLineSegment(sketch, "E1303", {"start": v(-52.43, 4.95) * mm, "end": v(-52.36, 4.92) * mm});
            skLineSegment(sketch, "E1304", {"start": v(-52.36, 4.92) * mm, "end": v(-52.29, 4.9) * mm});
            skLineSegment(sketch, "E1305", {"start": v(-52.29, 4.9) * mm, "end": v(-52.15, 4.87) * mm});
            skLineSegment(sketch, "E1306", {"start": v(-52.15, 4.87) * mm, "end": v(-52.02, 4.86) * mm});
            skLineSegment(sketch, "E1307", {"start": v(-52.02, 4.86) * mm, "end": v(-51.89, 4.86) * mm});
            skLineSegment(sketch, "E1308", {"start": v(-51.89, 4.86) * mm, "end": v(-51.76, 4.87) * mm});
            skLineSegment(sketch, "E1309", {"start": v(-51.76, 4.87) * mm, "end": v(-51.5, 4.91) * mm});
            skLineSegment(sketch, "E1310", {"start": v(-51.5, 4.91) * mm, "end": v(-51.26, 4.98) * mm});
            skLineSegment(sketch, "E1311", {"start": v(-51.26, 4.98) * mm, "end": v(-51, 4.98) * mm});
            skLineSegment(sketch, "E1312", {"start": v(-51, 4.98) * mm, "end": v(-50.74, 4.96) * mm});
            skLineSegment(sketch, "E1313", {"start": v(-50.74, 4.96) * mm, "end": v(-50.47, 4.91) * mm});
            skLineSegment(sketch, "E1314", {"start": v(-50.47, 4.91) * mm, "end": v(-50.2, 4.85) * mm});
            skLineSegment(sketch, "E1315", {"start": v(-50.2, 4.85) * mm, "end": v(-49.93, 4.76) * mm});
            skLineSegment(sketch, "E1316", {"start": v(-49.93, 4.76) * mm, "end": v(-49.65, 4.66) * mm});
            skLineSegment(sketch, "E1317", {"start": v(-49.65, 4.66) * mm, "end": v(-49.38, 4.54) * mm});
            skLineSegment(sketch, "E1318", {"start": v(-49.38, 4.54) * mm, "end": v(-49.1, 4.4) * mm});
            skLineSegment(sketch, "E1319", {"start": v(-49.1, 4.4) * mm, "end": v(-48.83, 4.25) * mm});
            skLineSegment(sketch, "E1320", {"start": v(-48.83, 4.25) * mm, "end": v(-48.63, 4.13) * mm});
            skLineSegment(sketch, "E1321", {"start": v(-48.63, 4.13) * mm, "end": v(-48.57, 2.98) * mm});
            skLineSegment(sketch, "E1322", {"start": v(-48.57, 2.98) * mm, "end": v(-48.63, 1.82) * mm});
            skLineSegment(sketch, "E1323", {"start": v(-48.63, 1.82) * mm, "end": v(-48.83, 1.7) * mm});
            skLineSegment(sketch, "E1324", {"start": v(-48.83, 1.7) * mm, "end": v(-49.1, 1.55) * mm});
            skLineSegment(sketch, "E1325", {"start": v(-49.1, 1.55) * mm, "end": v(-49.38, 1.41) * mm});
            skLineSegment(sketch, "E1326", {"start": v(-49.38, 1.41) * mm, "end": v(-49.65, 1.3) * mm});
            skLineSegment(sketch, "E1327", {"start": v(-49.65, 1.3) * mm, "end": v(-49.93, 1.19) * mm});
            skLineSegment(sketch, "E1328", {"start": v(-49.93, 1.19) * mm, "end": v(-50.2, 1.1) * mm});
            skLineSegment(sketch, "E1329", {"start": v(-50.2, 1.1) * mm, "end": v(-50.47, 1.04) * mm});
            skLineSegment(sketch, "E1330", {"start": v(-50.47, 1.04) * mm, "end": v(-50.74, 1) * mm});
            skLineSegment(sketch, "E1331", {"start": v(-50.74, 1) * mm, "end": v(-51, 0.97) * mm});
            skLineSegment(sketch, "E1332", {"start": v(-51, 0.97) * mm, "end": v(-51.26, 0.98) * mm});
            skLineSegment(sketch, "E1333", {"start": v(-51.26, 0.98) * mm, "end": v(-51.5, 1.04) * mm});
            skLineSegment(sketch, "E1334", {"start": v(-51.5, 1.04) * mm, "end": v(-51.76, 1.08) * mm});
            skLineSegment(sketch, "E1335", {"start": v(-51.76, 1.08) * mm, "end": v(-51.89, 1.1) * mm});
            skLineSegment(sketch, "E1336", {"start": v(-51.89, 1.1) * mm, "end": v(-52.02, 1.1) * mm});
            skLineSegment(sketch, "E1337", {"start": v(-52.02, 1.1) * mm, "end": v(-52.15, 1.08) * mm});
            skLineSegment(sketch, "E1338", {"start": v(-52.15, 1.08) * mm, "end": v(-52.29, 1.06) * mm});
            skLineSegment(sketch, "E1339", {"start": v(-52.29, 1.06) * mm, "end": v(-52.36, 1.03) * mm});
            skLineSegment(sketch, "E1340", {"start": v(-52.36, 1.03) * mm, "end": v(-52.43, 1) * mm});
            skLineSegment(sketch, "E1341", {"start": v(-52.43, 1) * mm, "end": v(-52.5, 0.96) * mm});
            skLineSegment(sketch, "E1342", {"start": v(-52.5, 0.96) * mm, "end": v(-52.59, 0.9) * mm});
            skLineSegment(sketch, "E1343", {"start": v(-52.59, 0.9) * mm, "end": v(-53.01, -0.17) * mm});
            skLineSegment(sketch, "E1344", {"start": v(-53.01, -0.17) * mm, "end": v(-53.47, -1.22) * mm});
            skLineSegment(sketch, "E1345", {"start": v(-53.47, -1.22) * mm, "end": v(-53.45, -1.33) * mm});
            skLineSegment(sketch, "E1346", {"start": v(-53.45, -1.33) * mm, "end": v(-53.43, -1.4) * mm});
            skLineSegment(sketch, "E1347", {"start": v(-53.43, -1.4) * mm, "end": v(-53.4, -1.48) * mm});
            skLineSegment(sketch, "E1348", {"start": v(-53.4, -1.48) * mm, "end": v(-53.37, -1.55) * mm});
            skLineSegment(sketch, "E1349", {"start": v(-53.37, -1.55) * mm, "end": v(-53.29, -1.66) * mm});
            skLineSegment(sketch, "E1350", {"start": v(-53.29, -1.66) * mm, "end": v(-53.2, -1.76) * mm});
            skLineSegment(sketch, "E1351", {"start": v(-53.2, -1.76) * mm, "end": v(-53.11, -1.86) * mm});
            skLineSegment(sketch, "E1352", {"start": v(-53.11, -1.86) * mm, "end": v(-53.01, -1.94) * mm});
            skLineSegment(sketch, "E1353", {"start": v(-53.01, -1.94) * mm, "end": v(-52.8, -2.09) * mm});
            skLineSegment(sketch, "E1354", {"start": v(-52.8, -2.09) * mm, "end": v(-52.58, -2.21) * mm});
            skLineSegment(sketch, "E1355", {"start": v(-52.58, -2.21) * mm, "end": v(-52.4, -2.4) * mm});
            skLineSegment(sketch, "E1356", {"start": v(-52.4, -2.4) * mm, "end": v(-52.23, -2.6) * mm});
            skLineSegment(sketch, "E1357", {"start": v(-52.23, -2.6) * mm, "end": v(-52.07, -2.82) * mm});
            skLineSegment(sketch, "E1358", {"start": v(-52.07, -2.82) * mm, "end": v(-51.92, -3.06) * mm});
            skLineSegment(sketch, "E1359", {"start": v(-51.92, -3.06) * mm, "end": v(-51.8, -3.3) * mm});
            skLineSegment(sketch, "E1360", {"start": v(-51.8, -3.3) * mm, "end": v(-51.67, -3.57) * mm});
            skLineSegment(sketch, "E1361", {"start": v(-51.67, -3.57) * mm, "end": v(-51.56, -3.85) * mm});
            skLineSegment(sketch, "E1362", {"start": v(-51.56, -3.85) * mm, "end": v(-51.46, -4.14) * mm});
            skLineSegment(sketch, "E1363", {"start": v(-51.46, -4.14) * mm, "end": v(-51.38, -4.44) * mm});
            skLineSegment(sketch, "E1364", {"start": v(-51.38, -4.44) * mm, "end": v(-51.32, -4.68) * mm});
            skLineSegment(sketch, "E1365", {"start": v(-51.32, -4.68) * mm, "end": v(-52.1, -5.53) * mm});
            skLineSegment(sketch, "E1366", {"start": v(-52.1, -5.53) * mm, "end": v(-52.95, -6.3) * mm});
            skLineSegment(sketch, "E1367", {"start": v(-52.95, -6.3) * mm, "end": v(-53.18, -6.25) * mm});
            skLineSegment(sketch, "E1368", {"start": v(-53.18, -6.25) * mm, "end": v(-53.48, -6.16) * mm});
            skLineSegment(sketch, "E1369", {"start": v(-53.48, -6.16) * mm, "end": v(-53.77, -6.06) * mm});
            skLineSegment(sketch, "E1370", {"start": v(-53.77, -6.06) * mm, "end": v(-54.05, -5.96) * mm});
            skLineSegment(sketch, "E1371", {"start": v(-54.05, -5.96) * mm, "end": v(-54.32, -5.83) * mm});
            skLineSegment(sketch, "E1372", {"start": v(-54.32, -5.83) * mm, "end": v(-54.57, -5.7) * mm});
            skLineSegment(sketch, "E1373", {"start": v(-54.57, -5.7) * mm, "end": v(-54.8, -5.56) * mm});
            skLineSegment(sketch, "E1374", {"start": v(-54.8, -5.56) * mm, "end": v(-55.03, -5.4) * mm});
            skLineSegment(sketch, "E1375", {"start": v(-55.03, -5.4) * mm, "end": v(-55.24, -5.23) * mm});
            skLineSegment(sketch, "E1376", {"start": v(-55.24, -5.23) * mm, "end": v(-55.41, -5.04) * mm});
            skLineSegment(sketch, "E1377", {"start": v(-55.41, -5.04) * mm, "end": v(-55.54, -4.82) * mm});
            skLineSegment(sketch, "E1378", {"start": v(-55.54, -4.82) * mm, "end": v(-55.69, -4.61) * mm});
            skLineSegment(sketch, "E1379", {"start": v(-55.69, -4.61) * mm, "end": v(-55.77, -4.52) * mm});
            skLineSegment(sketch, "E1380", {"start": v(-55.77, -4.52) * mm, "end": v(-55.86, -4.42) * mm});
            skLineSegment(sketch, "E1381", {"start": v(-55.86, -4.42) * mm, "end": v(-55.96, -4.34) * mm});
            skLineSegment(sketch, "E1382", {"start": v(-55.96, -4.34) * mm, "end": v(-56.08, -4.26) * mm});
            skLineSegment(sketch, "E1383", {"start": v(-56.08, -4.26) * mm, "end": v(-56.15, -4.23) * mm});
            skLineSegment(sketch, "E1384", {"start": v(-56.15, -4.23) * mm, "end": v(-56.22, -4.2) * mm});
            skLineSegment(sketch, "E1385", {"start": v(-56.22, -4.2) * mm, "end": v(-56.3, -4.17) * mm});
            skLineSegment(sketch, "E1386", {"start": v(-56.3, -4.17) * mm, "end": v(-56.4, -4.16) * mm});
            skLineSegment(sketch, "E1387", {"start": v(-56.4, -4.16) * mm, "end": v(-57.46, -4.61) * mm});
            skLineSegment(sketch, "E1388", {"start": v(-57.46, -4.61) * mm, "end": v(-58.52, -5.04) * mm});
            skLineSegment(sketch, "E1389", {"start": v(-58.52, -5.04) * mm, "end": v(-58.59, -5.12) * mm});
            skLineSegment(sketch, "E1390", {"start": v(-58.59, -5.12) * mm, "end": v(-58.63, -5.2) * mm});
            skLineSegment(sketch, "E1391", {"start": v(-58.63, -5.2) * mm, "end": v(-58.66, -5.27) * mm});
            skLineSegment(sketch, "E1392", {"start": v(-58.66, -5.27) * mm, "end": v(-58.68, -5.34) * mm});
            skLineSegment(sketch, "E1393", {"start": v(-58.68, -5.34) * mm, "end": v(-58.71, -5.48) * mm});
            skLineSegment(sketch, "E1394", {"start": v(-58.71, -5.48) * mm, "end": v(-58.72, -5.6) * mm});
            skLineSegment(sketch, "E1395", {"start": v(-58.72, -5.6) * mm, "end": v(-58.72, -5.74) * mm});
            skLineSegment(sketch, "E1396", {"start": v(-58.72, -5.74) * mm, "end": v(-58.71, -5.87) * mm});
            skLineSegment(sketch, "E1397", {"start": v(-58.71, -5.87) * mm, "end": v(-58.67, -6.12) * mm});
            skLineSegment(sketch, "E1398", {"start": v(-58.67, -6.12) * mm, "end": v(-58.6, -6.36) * mm});
            skLineSegment(sketch, "E1399", {"start": v(-58.6, -6.36) * mm, "end": v(-58.6, -6.62) * mm});
            skLineSegment(sketch, "E1400", {"start": v(-58.6, -6.62) * mm, "end": v(-58.62, -6.89) * mm});
            skLineSegment(sketch, "E1401", {"start": v(-58.62, -6.89) * mm, "end": v(-58.66, -7.15) * mm});
            skLineSegment(sketch, "E1402", {"start": v(-58.66, -7.15) * mm, "end": v(-58.73, -7.42) * mm});
            skLineSegment(sketch, "E1403", {"start": v(-58.73, -7.42) * mm, "end": v(-58.82, -7.7) * mm});
            skLineSegment(sketch, "E1404", {"start": v(-58.82, -7.7) * mm, "end": v(-58.92, -7.97) * mm});
            skLineSegment(sketch, "E1405", {"start": v(-58.92, -7.97) * mm, "end": v(-59.04, -8.25) * mm});
            skLineSegment(sketch, "E1406", {"start": v(-59.04, -8.25) * mm, "end": v(-59.17, -8.52) * mm});
            skLineSegment(sketch, "E1407", {"start": v(-59.17, -8.52) * mm, "end": v(-59.33, -8.8) * mm});
            skLineSegment(sketch, "E1408", {"start": v(-59.33, -8.8) * mm, "end": v(-59.45, -9) * mm});
            skLineSegment(sketch, "E1409", {"start": v(-59.45, -9) * mm, "end": v(-60.6, -9.05) * mm});
            skLineSegment(sketch, "E1410", {"start": v(-60.6, -9.05) * mm, "end": v(-61.75, -9) * mm});
            skLineSegment(sketch, "E1411", {"start": v(-61.75, -9) * mm, "end": v(-61.88, -8.8) * mm});
            skLineSegment(sketch, "E1412", {"start": v(-61.88, -8.8) * mm, "end": v(-62.03, -8.52) * mm});
            skLineSegment(sketch, "E1413", {"start": v(-62.03, -8.52) * mm, "end": v(-62.17, -8.25) * mm});
            skLineSegment(sketch, "E1414", {"start": v(-62.17, -8.25) * mm, "end": v(-62.29, -7.97) * mm});
            skLineSegment(sketch, "E1415", {"start": v(-62.29, -7.97) * mm, "end": v(-62.39, -7.7) * mm});
            skLineSegment(sketch, "E1416", {"start": v(-62.39, -7.7) * mm, "end": v(-62.47, -7.42) * mm});
            skLineSegment(sketch, "E1417", {"start": v(-62.47, -7.42) * mm, "end": v(-62.54, -7.15) * mm});
            skLineSegment(sketch, "E1418", {"start": v(-62.54, -7.15) * mm, "end": v(-62.59, -6.89) * mm});
            skLineSegment(sketch, "E1419", {"start": v(-62.59, -6.89) * mm, "end": v(-62.6, -6.62) * mm});
            skLineSegment(sketch, "E1420", {"start": v(-62.6, -6.62) * mm, "end": v(-62.6, -6.36) * mm});
            skLineSegment(sketch, "E1421", {"start": v(-62.6, -6.36) * mm, "end": v(-62.54, -6.12) * mm});
            skLineSegment(sketch, "E1422", {"start": v(-62.54, -6.12) * mm, "end": v(-62.5, -5.87) * mm});
            skLineSegment(sketch, "E1423", {"start": v(-62.5, -5.87) * mm, "end": v(-62.48, -5.74) * mm});
            skLineSegment(sketch, "E1424", {"start": v(-62.48, -5.74) * mm, "end": v(-62.48, -5.6) * mm});
            skLineSegment(sketch, "E1425", {"start": v(-62.48, -5.6) * mm, "end": v(-62.5, -5.48) * mm});
            skLineSegment(sketch, "E1426", {"start": v(-62.5, -5.48) * mm, "end": v(-62.52, -5.34) * mm});
            skLineSegment(sketch, "E1427", {"start": v(-62.52, -5.34) * mm, "end": v(-62.54, -5.27) * mm});
            skLineSegment(sketch, "E1428", {"start": v(-62.54, -5.27) * mm, "end": v(-62.57, -5.2) * mm});
            skLineSegment(sketch, "E1429", {"start": v(-62.57, -5.2) * mm, "end": v(-62.62, -5.12) * mm});
            skLineSegment(sketch, "E1430", {"start": v(-62.62, -5.12) * mm, "end": v(-62.68, -5.04) * mm});
            skLineSegment(sketch, "E1431", {"start": v(-62.68, -5.04) * mm, "end": v(-63.75, -4.61) * mm});
            skLineSegment(sketch, "E1432", {"start": v(-63.75, -4.61) * mm, "end": v(-64.8, -4.16) * mm});
            skLineSegment(sketch, "E1433", {"start": v(-64.8, -4.16) * mm, "end": v(-64.9, -4.17) * mm});
            skLineSegment(sketch, "E1434", {"start": v(-64.9, -4.17) * mm, "end": v(-64.99, -4.2) * mm});
            skLineSegment(sketch, "E1435", {"start": v(-64.99, -4.2) * mm, "end": v(-65.06, -4.23) * mm});
            skLineSegment(sketch, "E1436", {"start": v(-65.06, -4.23) * mm, "end": v(-65.12, -4.26) * mm});
            skLineSegment(sketch, "E1437", {"start": v(-65.12, -4.26) * mm, "end": v(-65.24, -4.34) * mm});
            skLineSegment(sketch, "E1438", {"start": v(-65.24, -4.34) * mm, "end": v(-65.34, -4.42) * mm});
            skLineSegment(sketch, "E1439", {"start": v(-65.34, -4.42) * mm, "end": v(-65.43, -4.52) * mm});
            skLineSegment(sketch, "E1440", {"start": v(-65.43, -4.52) * mm, "end": v(-65.52, -4.61) * mm});
            skLineSegment(sketch, "E1441", {"start": v(-65.52, -4.61) * mm, "end": v(-65.66, -4.82) * mm});
            skLineSegment(sketch, "E1442", {"start": v(-65.66, -4.82) * mm, "end": v(-65.8, -5.04) * mm});
            skLineSegment(sketch, "E1443", {"start": v(-65.8, -5.04) * mm, "end": v(-65.97, -5.23) * mm});
            skLineSegment(sketch, "E1444", {"start": v(-65.97, -5.23) * mm, "end": v(-66.17, -5.4) * mm});
            skLineSegment(sketch, "E1445", {"start": v(-66.17, -5.4) * mm, "end": v(-66.4, -5.56) * mm});
            skLineSegment(sketch, "E1446", {"start": v(-66.4, -5.56) * mm, "end": v(-66.63, -5.7) * mm});
            skLineSegment(sketch, "E1447", {"start": v(-66.63, -5.7) * mm, "end": v(-66.89, -5.83) * mm});
            skLineSegment(sketch, "E1448", {"start": v(-66.89, -5.83) * mm, "end": v(-67.15, -5.96) * mm});
            skLineSegment(sketch, "E1449", {"start": v(-67.15, -5.96) * mm, "end": v(-67.43, -6.06) * mm});
            skLineSegment(sketch, "E1450", {"start": v(-67.43, -6.06) * mm, "end": v(-67.72, -6.16) * mm});
            skLineSegment(sketch, "E1451", {"start": v(-67.72, -6.16) * mm, "end": v(-68.02, -6.25) * mm});
            skLineSegment(sketch, "E1452", {"start": v(-68.02, -6.25) * mm, "end": v(-68.26, -6.3) * mm});
            skLineSegment(sketch, "E1453", {"start": v(-68.26, -6.3) * mm, "end": v(-69.1, -5.53) * mm});
            skLineSegment(sketch, "E1454", {"start": v(-69.1, -5.53) * mm, "end": v(-69.88, -4.68) * mm});
            skLineSegment(sketch, "E1455", {"start": v(-69.88, -4.68) * mm, "end": v(-69.83, -4.44) * mm});
            skLineSegment(sketch, "E1456", {"start": v(-69.83, -4.44) * mm, "end": v(-69.74, -4.14) * mm});
            skLineSegment(sketch, "E1457", {"start": v(-69.74, -4.14) * mm, "end": v(-69.64, -3.85) * mm});
            skLineSegment(sketch, "E1458", {"start": v(-69.64, -3.85) * mm, "end": v(-69.53, -3.57) * mm});
            skLineSegment(sketch, "E1459", {"start": v(-69.53, -3.57) * mm, "end": v(-69.41, -3.3) * mm});
            skLineSegment(sketch, "E1460", {"start": v(-69.41, -3.3) * mm, "end": v(-69.28, -3.06) * mm});
            skLineSegment(sketch, "E1461", {"start": v(-69.28, -3.06) * mm, "end": v(-69.14, -2.82) * mm});
            skLineSegment(sketch, "E1462", {"start": v(-69.14, -2.82) * mm, "end": v(-68.98, -2.6) * mm});
            skLineSegment(sketch, "E1463", {"start": v(-68.98, -2.6) * mm, "end": v(-68.8, -2.4) * mm});
            skLineSegment(sketch, "E1464", {"start": v(-68.8, -2.4) * mm, "end": v(-68.62, -2.21) * mm});
            skLineSegment(sketch, "E1465", {"start": v(-68.62, -2.21) * mm, "end": v(-68.4, -2.09) * mm});
            skLineSegment(sketch, "E1466", {"start": v(-68.4, -2.09) * mm, "end": v(-68.2, -1.94) * mm});
            skLineSegment(sketch, "E1467", {"start": v(-68.2, -1.94) * mm, "end": v(-68.1, -1.86) * mm});
            skLineSegment(sketch, "E1468", {"start": v(-68.1, -1.86) * mm, "end": v(-68, -1.76) * mm});
            skLineSegment(sketch, "E1469", {"start": v(-68, -1.76) * mm, "end": v(-67.92, -1.66) * mm});
            skLineSegment(sketch, "E1470", {"start": v(-67.92, -1.66) * mm, "end": v(-67.84, -1.55) * mm});
            skLineSegment(sketch, "E1471", {"start": v(-67.84, -1.55) * mm, "end": v(-67.8, -1.48) * mm});
            skLineSegment(sketch, "E1472", {"start": v(-67.8, -1.48) * mm, "end": v(-67.77, -1.4) * mm});
            skLineSegment(sketch, "E1473", {"start": v(-67.77, -1.4) * mm, "end": v(-67.75, -1.33) * mm});
            skLineSegment(sketch, "E1474", {"start": v(-67.75, -1.33) * mm, "end": v(-67.74, -1.22) * mm});
            skLineSegment(sketch, "E1475", {"start": v(-67.74, -1.22) * mm, "end": v(-68.2, -0.17) * mm});
            skLineSegment(sketch, "E1476", {"start": v(-68.2, -0.17) * mm, "end": v(-68.62, 0.9) * mm});
            skLineSegment(sketch, "E1477", {"start": v(-68.62, 0.9) * mm, "end": v(-68.7, 0.96) * mm});
            skLineSegment(sketch, "E1478", {"start": v(-68.7, 0.96) * mm, "end": v(-68.77, 1) * mm});
            skLineSegment(sketch, "E1479", {"start": v(-68.77, 1) * mm, "end": v(-68.85, 1.03) * mm});
            skLineSegment(sketch, "E1480", {"start": v(-68.85, 1.03) * mm, "end": v(-68.92, 1.06) * mm});
            skLineSegment(sketch, "E1481", {"start": v(-68.92, 1.06) * mm, "end": v(-69.05, 1.08) * mm});
            skLineSegment(sketch, "E1482", {"start": v(-69.05, 1.08) * mm, "end": v(-69.19, 1.1) * mm});
            skLineSegment(sketch, "E1483", {"start": v(-69.19, 1.1) * mm, "end": v(-69.32, 1.1) * mm});
            skLineSegment(sketch, "E1484", {"start": v(-69.32, 1.1) * mm, "end": v(-69.44, 1.08) * mm});
            skLineSegment(sketch, "E1485", {"start": v(-69.44, 1.08) * mm, "end": v(-69.7, 1.04) * mm});
            skLineSegment(sketch, "E1486", {"start": v(-69.7, 1.04) * mm, "end": v(-69.94, 0.98) * mm});
            skLineSegment(sketch, "E1487", {"start": v(-69.94, 0.98) * mm, "end": v(-70.2, 0.97) * mm});
            skLineSegment(sketch, "E1488", {"start": v(-70.2, 0.97) * mm, "end": v(-70.46, 1) * mm});
            skLineSegment(sketch, "E1489", {"start": v(-70.46, 1) * mm, "end": v(-70.73, 1.04) * mm});
            skLineSegment(sketch, "E1490", {"start": v(-70.73, 1.04) * mm, "end": v(-71, 1.1) * mm});
            skLineSegment(sketch, "E1491", {"start": v(-71, 1.1) * mm, "end": v(-71.28, 1.19) * mm});
            skLineSegment(sketch, "E1492", {"start": v(-71.28, 1.19) * mm, "end": v(-71.55, 1.3) * mm});
            skLineSegment(sketch, "E1493", {"start": v(-71.55, 1.3) * mm, "end": v(-71.82, 1.41) * mm});
            skLineSegment(sketch, "E1494", {"start": v(-71.82, 1.41) * mm, "end": v(-72.1, 1.55) * mm});
            skLineSegment(sketch, "E1495", {"start": v(-72.1, 1.55) * mm, "end": v(-72.37, 1.7) * mm});
            skLineSegment(sketch, "E1496", {"start": v(-72.37, 1.7) * mm, "end": v(-72.58, 1.82) * mm});
            skLineSegment(sketch, "E1497", {"start": v(-72.58, 1.82) * mm, "end": v(-72.63, 2.98) * mm});
            skLineSegment(sketch, "E1498", {"start": v(-72.63, 2.98) * mm, "end": v(-72.58, 4.13) * mm});
            skLineSegment(sketch, "E1499", {"start": v(-72.58, 4.13) * mm, "end": v(-72.37, 4.25) * mm});
            skLineSegment(sketch, "E1500", {"start": v(-72.37, 4.25) * mm, "end": v(-72.1, 4.4) * mm});
            skLineSegment(sketch, "E1501", {"start": v(-72.1, 4.4) * mm, "end": v(-71.82, 4.54) * mm});
            skLineSegment(sketch, "E1502", {"start": v(-71.82, 4.54) * mm, "end": v(-71.55, 4.66) * mm});
            skLineSegment(sketch, "E1503", {"start": v(-71.55, 4.66) * mm, "end": v(-71.28, 4.76) * mm});
            skLineSegment(sketch, "E1504", {"start": v(-71.28, 4.76) * mm, "end": v(-71, 4.85) * mm});
            skLineSegment(sketch, "E1505", {"start": v(-71, 4.85) * mm, "end": v(-70.73, 4.91) * mm});
            skLineSegment(sketch, "E1506", {"start": v(-70.73, 4.91) * mm, "end": v(-70.46, 4.96) * mm});
            skLineSegment(sketch, "E1507", {"start": v(-70.46, 4.96) * mm, "end": v(-70.2, 4.98) * mm});
            skLineSegment(sketch, "E1508", {"start": v(-70.2, 4.98) * mm, "end": v(-69.94, 4.98) * mm});
            skLineSegment(sketch, "E1509", {"start": v(-69.94, 4.98) * mm, "end": v(-69.7, 4.91) * mm});
            skLineSegment(sketch, "E1510", {"start": v(-69.7, 4.91) * mm, "end": v(-69.44, 4.87) * mm});
            skLineSegment(sketch, "E1511", {"start": v(-69.44, 4.87) * mm, "end": v(-69.32, 4.86) * mm});
            skLineSegment(sketch, "E1512", {"start": v(-69.32, 4.86) * mm, "end": v(-69.19, 4.86) * mm});
            skLineSegment(sketch, "E1513", {"start": v(-69.19, 4.86) * mm, "end": v(-69.05, 4.87) * mm});
            skLineSegment(sketch, "E1514", {"start": v(-69.05, 4.87) * mm, "end": v(-68.92, 4.9) * mm});
            skLineSegment(sketch, "E1515", {"start": v(-68.92, 4.9) * mm, "end": v(-68.85, 4.92) * mm});
            skLineSegment(sketch, "E1516", {"start": v(-68.85, 4.92) * mm, "end": v(-68.77, 4.95) * mm});
            skLineSegment(sketch, "E1517", {"start": v(-68.77, 4.95) * mm, "end": v(-68.7, 4.99) * mm});
            skLineSegment(sketch, "E1518", {"start": v(-68.7, 4.99) * mm, "end": v(-68.62, 5.05) * mm});
            skLineSegment(sketch, "E1519", {"start": v(-68.62, 5.05) * mm, "end": v(-68.2, 6.12) * mm});
            skLineSegment(sketch, "E1520", {"start": v(-68.2, 6.12) * mm, "end": v(-67.74, 7.17) * mm});
            skLineSegment(sketch, "E1521", {"start": v(-67.74, 7.17) * mm, "end": v(-67.75, 7.28) * mm});
            skLineSegment(sketch, "E1522", {"start": v(-67.75, 7.28) * mm, "end": v(-67.77, 7.36) * mm});
            skLineSegment(sketch, "E1523", {"start": v(-67.77, 7.36) * mm, "end": v(-67.8, 7.43) * mm});
            skLineSegment(sketch, "E1524", {"start": v(-67.8, 7.43) * mm, "end": v(-67.84, 7.5) * mm});
            skLineSegment(sketch, "E1525", {"start": v(-67.84, 7.5) * mm, "end": v(-67.92, 7.61) * mm});
            skLineSegment(sketch, "E1526", {"start": v(-67.92, 7.61) * mm, "end": v(-68, 7.72) * mm});
            skLineSegment(sketch, "E1527", {"start": v(-68, 7.72) * mm, "end": v(-68.1, 7.8) * mm});
            skLineSegment(sketch, "E1528", {"start": v(-68.1, 7.8) * mm, "end": v(-68.2, 7.9) * mm});
            skLineSegment(sketch, "E1529", {"start": v(-68.2, 7.9) * mm, "end": v(-68.4, 8.04) * mm});
            skLineSegment(sketch, "E1530", {"start": v(-68.4, 8.04) * mm, "end": v(-68.62, 8.16) * mm});
            skLineSegment(sketch, "E1531", {"start": v(-68.62, 8.16) * mm, "end": v(-68.8, 8.34) * mm});
            skLineSegment(sketch, "E1532", {"start": v(-68.8, 8.34) * mm, "end": v(-68.98, 8.55) * mm});
            skLineSegment(sketch, "E1533", {"start": v(-68.98, 8.55) * mm, "end": v(-69.14, 8.77) * mm});
            skLineSegment(sketch, "E1534", {"start": v(-69.14, 8.77) * mm, "end": v(-69.28, 9) * mm});
            skLineSegment(sketch, "E1535", {"start": v(-69.28, 9) * mm, "end": v(-69.41, 9.26) * mm});
            skLineSegment(sketch, "E1536", {"start": v(-69.41, 9.26) * mm, "end": v(-69.53, 9.53) * mm});
            skLineSegment(sketch, "E1537", {"start": v(-69.53, 9.53) * mm, "end": v(-69.64, 9.8) * mm});
            skLineSegment(sketch, "E1538", {"start": v(-69.64, 9.8) * mm, "end": v(-69.74, 10.1) * mm});
            skLineSegment(sketch, "E1539", {"start": v(-69.74, 10.1) * mm, "end": v(-69.83, 10.4) * mm});
            skLineSegment(sketch, "E1540", {"start": v(-69.83, 10.4) * mm, "end": v(-69.88, 10.63) * mm});
            skLineSegment(sketch, "E1541", {"start": v(-69.88, 10.63) * mm, "end": v(-69.1, 11.48) * mm});
            skLineSegment(sketch, "E1542", {"start": v(-69.1, 11.48) * mm, "end": v(-68.26, 12.26) * mm});
            skLineSegment(sketch, "E1543", {"start": v(-68.26, 12.26) * mm, "end": v(-68.02, 12.2) * mm});
            skLineSegment(sketch, "E1544", {"start": v(-68.02, 12.2) * mm, "end": v(-67.72, 12.11) * mm});
            skLineSegment(sketch, "E1545", {"start": v(-67.72, 12.11) * mm, "end": v(-67.43, 12.02) * mm});
            skLineSegment(sketch, "E1546", {"start": v(-67.43, 12.02) * mm, "end": v(-67.15, 11.9) * mm});
            skLineSegment(sketch, "E1547", {"start": v(-67.15, 11.9) * mm, "end": v(-66.89, 11.79) * mm});
            skLineSegment(sketch, "E1548", {"start": v(-66.89, 11.79) * mm, "end": v(-66.63, 11.65) * mm});
            skLineSegment(sketch, "E1549", {"start": v(-66.63, 11.65) * mm, "end": v(-66.4, 11.5) * mm});
            skLineSegment(sketch, "E1550", {"start": v(-66.4, 11.5) * mm, "end": v(-66.17, 11.35) * mm});
            skLineSegment(sketch, "E1551", {"start": v(-66.17, 11.35) * mm, "end": v(-65.97, 11.18) * mm});
            skLineSegment(sketch, "E1552", {"start": v(-65.97, 11.18) * mm, "end": v(-65.8, 11) * mm});
            skLineSegment(sketch, "E1553", {"start": v(-65.8, 11) * mm, "end": v(-65.66, 10.77) * mm});
            skLineSegment(sketch, "E1554", {"start": v(-65.66, 10.77) * mm, "end": v(-65.52, 10.57) * mm});
            skLineSegment(sketch, "E1555", {"start": v(-65.52, 10.57) * mm, "end": v(-65.43, 10.47) * mm});
            skLineSegment(sketch, "E1556", {"start": v(-65.43, 10.47) * mm, "end": v(-65.34, 10.38) * mm});
            skLineSegment(sketch, "E1557", {"start": v(-65.34, 10.38) * mm, "end": v(-65.24, 10.29) * mm});
            skLineSegment(sketch, "E1558", {"start": v(-65.24, 10.29) * mm, "end": v(-65.12, 10.21) * mm});
            skLineSegment(sketch, "E1559", {"start": v(-65.12, 10.21) * mm, "end": v(-65.06, 10.18) * mm});
            skLineSegment(sketch, "E1560", {"start": v(-65.06, 10.18) * mm, "end": v(-64.99, 10.15) * mm});
            skLineSegment(sketch, "E1561", {"start": v(-64.99, 10.15) * mm, "end": v(-64.9, 10.12) * mm});
            skLineSegment(sketch, "E1562", {"start": v(-64.9, 10.12) * mm, "end": v(-64.8, 10.11) * mm});
            skLineSegment(sketch, "E1563", {"start": v(-64.8, 10.11) * mm, "end": v(-63.75, 10.57) * mm});
            skLineSegment(sketch, "E1564", {"start": v(-63.75, 10.57) * mm, "end": v(-62.68, 10.99) * mm});
            skLineSegment(sketch, "E1565", {"start": v(-62.68, 10.99) * mm, "end": v(-62.62, 11.07) * mm});
            skLineSegment(sketch, "E1566", {"start": v(-62.62, 11.07) * mm, "end": v(-62.57, 11.15) * mm});
            skLineSegment(sketch, "E1567", {"start": v(-62.57, 11.15) * mm, "end": v(-62.54, 11.22) * mm});
            skLineSegment(sketch, "E1568", {"start": v(-62.54, 11.22) * mm, "end": v(-62.52, 11.3) * mm});
            skLineSegment(sketch, "E1569", {"start": v(-62.52, 11.3) * mm, "end": v(-62.5, 11.43) * mm});
            skLineSegment(sketch, "E1570", {"start": v(-62.5, 11.43) * mm, "end": v(-62.48, 11.56) * mm});
            skLineSegment(sketch, "E1571", {"start": v(-62.48, 11.56) * mm, "end": v(-62.48, 11.69) * mm});
            skLineSegment(sketch, "E1572", {"start": v(-62.48, 11.69) * mm, "end": v(-62.5, 11.82) * mm});
            skLineSegment(sketch, "E1573", {"start": v(-62.5, 11.82) * mm, "end": v(-62.54, 12.07) * mm});
            skLineSegment(sketch, "E1574", {"start": v(-62.54, 12.07) * mm, "end": v(-62.6, 12.31) * mm});
            skLineSegment(sketch, "E1575", {"start": v(-62.6, 12.31) * mm, "end": v(-62.6, 12.57) * mm});
            skLineSegment(sketch, "E1576", {"start": v(-62.6, 12.57) * mm, "end": v(-62.59, 12.84) * mm});
            skLineSegment(sketch, "E1577", {"start": v(-62.59, 12.84) * mm, "end": v(-62.54, 13.1) * mm});
            skLineSegment(sketch, "E1578", {"start": v(-62.54, 13.1) * mm, "end": v(-62.47, 13.38) * mm});
            skLineSegment(sketch, "E1579", {"start": v(-62.47, 13.38) * mm, "end": v(-62.39, 13.65) * mm});
            skLineSegment(sketch, "E1580", {"start": v(-62.39, 13.65) * mm, "end": v(-62.29, 13.92) * mm});
            skLineSegment(sketch, "E1581", {"start": v(-62.29, 13.92) * mm, "end": v(-62.17, 14.2) * mm});
            skLineSegment(sketch, "E1582", {"start": v(-62.17, 14.2) * mm, "end": v(-62.03, 14.47) * mm});
            skLineSegment(sketch, "E1583", {"start": v(-62.03, 14.47) * mm, "end": v(-61.88, 14.75) * mm});
            skLineSegment(sketch, "E1584", {"start": v(-61.88, 14.75) * mm, "end": v(-61.75, 14.95) * mm});
            skLineSegment(sketch, "E1585", {"start": v(-61.75, 14.95) * mm, "end": v(-60.6, 15) * mm});
            skLineSegment(sketch, "E1586", {"start": v(-60.6, 15) * mm, "end": v(-59.45, 14.95) * mm});
            skLineSegment(sketch, "E1587", {"start": v(-59.45, 14.95) * mm, "end": v(-59.33, 14.75) * mm});
            skLineSegment(sketch, "E1588", {"start": v(-59.33, 14.75) * mm, "end": v(-59.17, 14.47) * mm});
            skLineSegment(sketch, "E1589", {"start": v(-59.17, 14.47) * mm, "end": v(-59.04, 14.2) * mm});
            skLineSegment(sketch, "E1590", {"start": v(-59.04, 14.2) * mm, "end": v(-58.92, 13.92) * mm});
            skLineSegment(sketch, "E1591", {"start": v(-58.92, 13.92) * mm, "end": v(-58.82, 13.65) * mm});
            skLineSegment(sketch, "E1592", {"start": v(-58.82, 13.65) * mm, "end": v(-58.73, 13.38) * mm});
            skLineSegment(sketch, "E1593", {"start": v(-58.73, 13.38) * mm, "end": v(-58.66, 13.1) * mm});
            skLineSegment(sketch, "E1594", {"start": v(-58.66, 13.1) * mm, "end": v(-58.62, 12.84) * mm});
            skLineSegment(sketch, "E1595", {"start": v(-58.62, 12.84) * mm, "end": v(-58.6, 12.57) * mm});
            skLineSegment(sketch, "E1596", {"start": v(-58.6, 12.57) * mm, "end": v(-58.6, 12.31) * mm});
            skLineSegment(sketch, "E1597", {"start": v(-58.6, 12.31) * mm, "end": v(-58.67, 12.07) * mm});
            skLineSegment(sketch, "E1598", {"start": v(-58.67, 12.07) * mm, "end": v(-58.71, 11.82) * mm});
            skLineSegment(sketch, "E1599", {"start": v(-58.71, 11.82) * mm, "end": v(-58.72, 11.69) * mm});
            skLineSegment(sketch, "E1600", {"start": v(-58.72, 11.69) * mm, "end": v(-58.72, 11.56) * mm});
            skLineSegment(sketch, "E1601", {"start": v(-58.72, 11.56) * mm, "end": v(-58.71, 11.43) * mm});
            skLineSegment(sketch, "E1602", {"start": v(-58.71, 11.43) * mm, "end": v(-58.68, 11.3) * mm});
            skLineSegment(sketch, "E1603", {"start": v(-58.68, 11.3) * mm, "end": v(-58.66, 11.22) * mm});
            skLineSegment(sketch, "E1604", {"start": v(-58.66, 11.22) * mm, "end": v(-58.63, 11.15) * mm});
            skLineSegment(sketch, "E1605", {"start": v(-58.63, 11.15) * mm, "end": v(-58.59, 11.07) * mm});
            skLineSegment(sketch, "E1606", {"start": v(-58.59, 11.07) * mm, "end": v(-58.52, 10.99) * mm});
            skLineSegment(sketch, "E1607", {"start": v(-58.52, 10.99) * mm, "end": v(-57.46, 10.57) * mm});
            skLineSegment(sketch, "E1608", {"start": v(-57.46, 10.57) * mm, "end": v(-56.4, 10.11) * mm});
            skLineSegment(sketch, "E1609", {"start": v(-56.4, 10.11) * mm, "end": v(-56.3, 10.12) * mm});
            skLineSegment(sketch, "E1610", {"start": v(-56.3, 10.12) * mm, "end": v(-56.22, 10.15) * mm});
            skLineSegment(sketch, "E1611", {"start": v(-56.22, 10.15) * mm, "end": v(-56.15, 10.18) * mm});
            skLineSegment(sketch, "E1612", {"start": v(-56.15, 10.18) * mm, "end": v(-56.08, 10.21) * mm});
            skLineSegment(sketch, "E1613", {"start": v(-56.08, 10.21) * mm, "end": v(-55.96, 10.29) * mm});
            skLineSegment(sketch, "E1614", {"start": v(-55.96, 10.29) * mm, "end": v(-55.86, 10.38) * mm});
            skLineSegment(sketch, "E1615", {"start": v(-55.86, 10.38) * mm, "end": v(-55.77, 10.47) * mm});
            skLineSegment(sketch, "E1616", {"start": v(-55.77, 10.47) * mm, "end": v(-55.69, 10.57) * mm});
            skLineSegment(sketch, "E1617", {"start": v(-55.69, 10.57) * mm, "end": v(-55.54, 10.77) * mm});
            skLineSegment(sketch, "E1618", {"start": v(-55.54, 10.77) * mm, "end": v(-55.41, 11) * mm});
            skLineSegment(sketch, "E1619", {"start": v(-55.41, 11) * mm, "end": v(-55.24, 11.18) * mm});
            skLineSegment(sketch, "E1620", {"start": v(-55.24, 11.18) * mm, "end": v(-55.03, 11.35) * mm});
            skLineSegment(sketch, "E1621", {"start": v(-55.03, 11.35) * mm, "end": v(-54.8, 11.5) * mm});
            skLineSegment(sketch, "E1622", {"start": v(-54.8, 11.5) * mm, "end": v(-54.57, 11.65) * mm});
            skLineSegment(sketch, "E1623", {"start": v(-54.57, 11.65) * mm, "end": v(-54.32, 11.79) * mm});
            skLineSegment(sketch, "E1624", {"start": v(-54.32, 11.79) * mm, "end": v(-54.05, 11.9) * mm});
            skLineSegment(sketch, "E1625", {"start": v(-54.05, 11.9) * mm, "end": v(-53.77, 12.02) * mm});
            skLineSegment(sketch, "E1626", {"start": v(-53.77, 12.02) * mm, "end": v(-53.48, 12.11) * mm});
            skLineSegment(sketch, "E1627", {"start": v(-53.48, 12.11) * mm, "end": v(-53.18, 12.2) * mm});
            skLineSegment(sketch, "E1628", {"start": v(-53.18, 12.2) * mm, "end": v(-52.95, 12.26) * mm});
            skLineSegment(sketch, "E1629", {"start": v(-52.95, 12.26) * mm, "end": v(-52.1, 11.48) * mm});
            skLineSegment(sketch, "E1630", {"start": v(-52.1, 11.48) * mm, "end": v(-51.32, 10.63) * mm});
            skLineSegment(sketch, "E1631", {"start": v(-51.32, 10.63) * mm, "end": v(-51.38, 10.4) * mm});
            skLineSegment(sketch, "E1632", {"start": v(-51.38, 10.4) * mm, "end": v(-51.46, 10.1) * mm});
            skLineSegment(sketch, "E1633", {"start": v(-51.46, 10.1) * mm, "end": v(-51.56, 9.8) * mm});
            skLineSegment(sketch, "E1634", {"start": v(-51.56, 9.8) * mm, "end": v(-51.67, 9.53) * mm});
            skLineSegment(sketch, "E1635", {"start": v(-51.67, 9.53) * mm, "end": v(-51.8, 9.26) * mm});
            skLineSegment(sketch, "E1636", {"start": v(-51.8, 9.26) * mm, "end": v(-51.92, 9) * mm});
            skLineSegment(sketch, "E1637", {"start": v(-51.92, 9) * mm, "end": v(-52.07, 8.77) * mm});
            skLineSegment(sketch, "E1638", {"start": v(-52.07, 8.77) * mm, "end": v(-52.23, 8.55) * mm});
            skLineSegment(sketch, "E1639", {"start": v(-52.23, 8.55) * mm, "end": v(-52.4, 8.34) * mm});
            skLineSegment(sketch, "E1640", {"start": v(-52.4, 8.34) * mm, "end": v(-52.58, 8.16) * mm});
            skLineSegment(sketch, "E1641", {"start": v(-52.58, 8.16) * mm, "end": v(-52.8, 8.04) * mm});
            skLineSegment(sketch, "E1642", {"start": v(-52.8, 8.04) * mm, "end": v(-53.01, 7.9) * mm});
            skLineSegment(sketch, "E1643", {"start": v(-53.01, 7.9) * mm, "end": v(-53.11, 7.8) * mm});
            skLineSegment(sketch, "E1644", {"start": v(-53.11, 7.8) * mm, "end": v(-53.2, 7.72) * mm});
            skLineSegment(sketch, "E1645", {"start": v(-53.2, 7.72) * mm, "end": v(-53.29, 7.61) * mm});
            skLineSegment(sketch, "E1646", {"start": v(-53.29, 7.61) * mm, "end": v(-53.37, 7.5) * mm});
            skLineSegment(sketch, "E1647", {"start": v(-53.37, 7.5) * mm, "end": v(-53.4, 7.43) * mm});
            skLineSegment(sketch, "E1648", {"start": v(-53.4, 7.43) * mm, "end": v(-53.43, 7.36) * mm});
            skLineSegment(sketch, "E1649", {"start": v(-53.43, 7.36) * mm, "end": v(-53.45, 7.28) * mm});
            skLineSegment(sketch, "E1650", {"start": v(-53.45, 7.28) * mm, "end": v(-53.47, 7.17) * mm});
            skLineSegment(sketch, "E1651", {"start": v(-53.47, 7.17) * mm, "end": v(-53.01, 6.12) * mm});
            skCircle(sketch, "E1652", {"center": v(-60.6, 2.98) * mm, "radius": 6.35 * mm});
            skLineSegment(sketch, "E1653", {"start": v(-48.57, 2.98) * mm, "end": v(-48.64, 4.15) * mm});
            skLineSegment(sketch, "E1654", {"start": v(-48.64, 4.15) * mm, "end": v(-48.73, 4.25) * mm});
            skLineSegment(sketch, "E1655", {"start": v(-48.73, 4.25) * mm, "end": v(-48.82, 4.46) * mm});
            skLineSegment(sketch, "E1656", {"start": v(-48.82, 4.46) * mm, "end": v(-49, 4.49) * mm});
            skLineSegment(sketch, "E1657", {"start": v(-49, 4.49) * mm, "end": v(-49.2, 4.53) * mm});
            skLineSegment(sketch, "E1658", {"start": v(-49.2, 4.53) * mm, "end": v(-49.38, 4.58) * mm});
            skLineSegment(sketch, "E1659", {"start": v(-49.38, 4.58) * mm, "end": v(-49.76, 4.7) * mm});
            skLineSegment(sketch, "E1660", {"start": v(-49.76, 4.7) * mm, "end": v(-50.13, 4.84) * mm});
            skLineSegment(sketch, "E1661", {"start": v(-50.13, 4.84) * mm, "end": v(-50.5, 5) * mm});
            skLineSegment(sketch, "E1662", {"start": v(-50.5, 5) * mm, "end": v(-50.87, 5.18) * mm});
            skLineSegment(sketch, "E1663", {"start": v(-50.87, 5.18) * mm, "end": v(-51.24, 5.38) * mm});
            skLineSegment(sketch, "E1664", {"start": v(-51.24, 5.38) * mm, "end": v(-51.6, 5.59) * mm});
            skLineSegment(sketch, "E1665", {"start": v(-51.6, 5.59) * mm, "end": v(-51.96, 5.82) * mm});
            skLineSegment(sketch, "E1666", {"start": v(-51.96, 5.82) * mm, "end": v(-52.23, 6) * mm});
            skLineSegment(sketch, "E1667", {"start": v(-52.23, 6) * mm, "end": v(-51.89, 8.42) * mm});
            skLineSegment(sketch, "E1668", {"start": v(-51.89, 8.42) * mm, "end": v(-51.58, 8.51) * mm});
            skLineSegment(sketch, "E1669", {"start": v(-51.58, 8.51) * mm, "end": v(-51.16, 8.63) * mm});
            skLineSegment(sketch, "E1670", {"start": v(-51.16, 8.63) * mm, "end": v(-50.76, 8.73) * mm});
            skLineSegment(sketch, "E1671", {"start": v(-50.76, 8.73) * mm, "end": v(-50.35, 8.81) * mm});
            skLineSegment(sketch, "E1672", {"start": v(-50.35, 8.81) * mm, "end": v(-49.94, 8.88) * mm});
            skLineSegment(sketch, "E1673", {"start": v(-49.94, 8.88) * mm, "end": v(-49.54, 8.93) * mm});
            skLineSegment(sketch, "E1674", {"start": v(-49.54, 8.93) * mm, "end": v(-49.15, 8.96) * mm});
            skLineSegment(sketch, "E1675", {"start": v(-49.15, 8.96) * mm, "end": v(-48.75, 8.97) * mm});
            skLineSegment(sketch, "E1676", {"start": v(-48.75, 8.97) * mm, "end": v(-48.56, 8.96) * mm});
            skLineSegment(sketch, "E1677", {"start": v(-48.56, 8.96) * mm, "end": v(-48.36, 8.95) * mm});
            skLineSegment(sketch, "E1678", {"start": v(-48.36, 8.95) * mm, "end": v(-48.17, 8.93) * mm});
            skLineSegment(sketch, "E1679", {"start": v(-48.17, 8.93) * mm, "end": v(-48.04, 9.1) * mm});
            skLineSegment(sketch, "E1680", {"start": v(-48.04, 9.1) * mm, "end": v(-47.92, 9.18) * mm});
            skLineSegment(sketch, "E1681", {"start": v(-47.92, 9.18) * mm, "end": v(-47.52, 10.28) * mm});
            skLineSegment(sketch, "E1682", {"start": v(-47.52, 10.28) * mm, "end": v(-47.26, 11.43) * mm});
            skLineSegment(sketch, "E1683", {"start": v(-47.26, 11.43) * mm, "end": v(-47.31, 11.55) * mm});
            skLineSegment(sketch, "E1684", {"start": v(-47.31, 11.55) * mm, "end": v(-47.34, 11.77) * mm});
            skLineSegment(sketch, "E1685", {"start": v(-47.34, 11.77) * mm, "end": v(-47.51, 11.86) * mm});
            skLineSegment(sketch, "E1686", {"start": v(-47.51, 11.86) * mm, "end": v(-47.68, 11.95) * mm});
            skLineSegment(sketch, "E1687", {"start": v(-47.68, 11.95) * mm, "end": v(-47.85, 12.05) * mm});
            skLineSegment(sketch, "E1688", {"start": v(-47.85, 12.05) * mm, "end": v(-48.17, 12.27) * mm});
            skLineSegment(sketch, "E1689", {"start": v(-48.17, 12.27) * mm, "end": v(-48.5, 12.51) * mm});
            skLineSegment(sketch, "E1690", {"start": v(-48.5, 12.51) * mm, "end": v(-48.8, 12.77) * mm});
            skLineSegment(sketch, "E1691", {"start": v(-48.8, 12.77) * mm, "end": v(-49.1, 13.05) * mm});
            skLineSegment(sketch, "E1692", {"start": v(-49.1, 13.05) * mm, "end": v(-49.4, 13.34) * mm});
            skLineSegment(sketch, "E1693", {"start": v(-49.4, 13.34) * mm, "end": v(-49.7, 13.64) * mm});
            skLineSegment(sketch, "E1694", {"start": v(-49.7, 13.64) * mm, "end": v(-49.98, 13.96) * mm});
            skLineSegment(sketch, "E1695", {"start": v(-49.98, 13.96) * mm, "end": v(-50.18, 14.2) * mm});
            skLineSegment(sketch, "E1696", {"start": v(-50.18, 14.2) * mm, "end": v(-49.17, 16.43) * mm});
            skLineSegment(sketch, "E1697", {"start": v(-49.17, 16.43) * mm, "end": v(-48.84, 16.44) * mm});
            skLineSegment(sketch, "E1698", {"start": v(-48.84, 16.44) * mm, "end": v(-48.42, 16.43) * mm});
            skLineSegment(sketch, "E1699", {"start": v(-48.42, 16.43) * mm, "end": v(-48, 16.41) * mm});
            skLineSegment(sketch, "E1700", {"start": v(-48, 16.41) * mm, "end": v(-47.58, 16.38) * mm});
            skLineSegment(sketch, "E1701", {"start": v(-47.58, 16.38) * mm, "end": v(-47.18, 16.33) * mm});
            skLineSegment(sketch, "E1702", {"start": v(-47.18, 16.33) * mm, "end": v(-46.78, 16.27) * mm});
            skLineSegment(sketch, "E1703", {"start": v(-46.78, 16.27) * mm, "end": v(-46.39, 16.18) * mm});
            skLineSegment(sketch, "E1704", {"start": v(-46.39, 16.18) * mm, "end": v(-46, 16.08) * mm});
            skLineSegment(sketch, "E1705", {"start": v(-46, 16.08) * mm, "end": v(-45.82, 16.02) * mm});
            skLineSegment(sketch, "E1706", {"start": v(-45.82, 16.02) * mm, "end": v(-45.64, 15.96) * mm});
            skLineSegment(sketch, "E1707", {"start": v(-45.64, 15.96) * mm, "end": v(-45.46, 15.88) * mm});
            skLineSegment(sketch, "E1708", {"start": v(-45.46, 15.88) * mm, "end": v(-45.28, 16) * mm});
            skLineSegment(sketch, "E1709", {"start": v(-45.28, 16) * mm, "end": v(-45.15, 16.05) * mm});
            skLineSegment(sketch, "E1710", {"start": v(-45.15, 16.05) * mm, "end": v(-44.46, 17) * mm});
            skLineSegment(sketch, "E1711", {"start": v(-44.46, 17) * mm, "end": v(-43.88, 18.02) * mm});
            skLineSegment(sketch, "E1712", {"start": v(-43.88, 18.02) * mm, "end": v(-43.9, 18.16) * mm});
            skLineSegment(sketch, "E1713", {"start": v(-43.9, 18.16) * mm, "end": v(-43.86, 18.37) * mm});
            skLineSegment(sketch, "E1714", {"start": v(-43.86, 18.37) * mm, "end": v(-44, 18.5) * mm});
            skLineSegment(sketch, "E1715", {"start": v(-44, 18.5) * mm, "end": v(-44.14, 18.64) * mm});
            skLineSegment(sketch, "E1716", {"start": v(-44.14, 18.64) * mm, "end": v(-44.27, 18.78) * mm});
            skLineSegment(sketch, "E1717", {"start": v(-44.27, 18.78) * mm, "end": v(-44.52, 19.09) * mm});
            skLineSegment(sketch, "E1718", {"start": v(-44.52, 19.09) * mm, "end": v(-44.76, 19.4) * mm});
            skLineSegment(sketch, "E1719", {"start": v(-44.76, 19.4) * mm, "end": v(-44.98, 19.74) * mm});
            skLineSegment(sketch, "E1720", {"start": v(-44.98, 19.74) * mm, "end": v(-45.2, 20.1) * mm});
            skLineSegment(sketch, "E1721", {"start": v(-45.2, 20.1) * mm, "end": v(-45.4, 20.46) * mm});
            skLineSegment(sketch, "E1722", {"start": v(-45.4, 20.46) * mm, "end": v(-45.6, 20.83) * mm});
            skLineSegment(sketch, "E1723", {"start": v(-45.6, 20.83) * mm, "end": v(-45.77, 21.22) * mm});
            skLineSegment(sketch, "E1724", {"start": v(-45.77, 21.22) * mm, "end": v(-45.9, 21.51) * mm});
            skLineSegment(sketch, "E1725", {"start": v(-45.9, 21.51) * mm, "end": v(-44.3, 23.36) * mm});
            skLineSegment(sketch, "E1726", {"start": v(-44.3, 23.36) * mm, "end": v(-43.99, 23.28) * mm});
            skLineSegment(sketch, "E1727", {"start": v(-43.99, 23.28) * mm, "end": v(-43.58, 23.15) * mm});
            skLineSegment(sketch, "E1728", {"start": v(-43.58, 23.15) * mm, "end": v(-43.18, 23.01) * mm});
            skLineSegment(sketch, "E1729", {"start": v(-43.18, 23.01) * mm, "end": v(-42.8, 22.86) * mm});
            skLineSegment(sketch, "E1730", {"start": v(-42.8, 22.86) * mm, "end": v(-42.42, 22.7) * mm});
            skLineSegment(sketch, "E1731", {"start": v(-42.42, 22.7) * mm, "end": v(-42.05, 22.53) * mm});
            skLineSegment(sketch, "E1732", {"start": v(-42.05, 22.53) * mm, "end": v(-41.7, 22.34) * mm});
            skLineSegment(sketch, "E1733", {"start": v(-41.7, 22.34) * mm, "end": v(-41.37, 22.13) * mm});
            skLineSegment(sketch, "E1734", {"start": v(-41.37, 22.13) * mm, "end": v(-41.2, 22.02) * mm});
            skLineSegment(sketch, "E1735", {"start": v(-41.2, 22.02) * mm, "end": v(-41.05, 21.9) * mm});
            skLineSegment(sketch, "E1736", {"start": v(-41.05, 21.9) * mm, "end": v(-40.9, 21.79) * mm});
            skLineSegment(sketch, "E1737", {"start": v(-40.9, 21.79) * mm, "end": v(-40.7, 21.86) * mm});
            skLineSegment(sketch, "E1738", {"start": v(-40.7, 21.86) * mm, "end": v(-40.55, 21.86) * mm});
            skLineSegment(sketch, "E1739", {"start": v(-40.55, 21.86) * mm, "end": v(-39.62, 22.57) * mm});
            skLineSegment(sketch, "E1740", {"start": v(-39.62, 22.57) * mm, "end": v(-38.78, 23.4) * mm});
            skLineSegment(sketch, "E1741", {"start": v(-38.78, 23.4) * mm, "end": v(-38.76, 23.53) * mm});
            skLineSegment(sketch, "E1742", {"start": v(-38.76, 23.53) * mm, "end": v(-38.66, 23.73) * mm});
            skLineSegment(sketch, "E1743", {"start": v(-38.66, 23.73) * mm, "end": v(-38.76, 23.9) * mm});
            skLineSegment(sketch, "E1744", {"start": v(-38.76, 23.9) * mm, "end": v(-38.85, 24.06) * mm});
            skLineSegment(sketch, "E1745", {"start": v(-38.85, 24.06) * mm, "end": v(-38.94, 24.24) * mm});
            skLineSegment(sketch, "E1746", {"start": v(-38.94, 24.24) * mm, "end": v(-39.1, 24.6) * mm});
            skLineSegment(sketch, "E1747", {"start": v(-39.1, 24.6) * mm, "end": v(-39.23, 24.97) * mm});
            skLineSegment(sketch, "E1748", {"start": v(-39.23, 24.97) * mm, "end": v(-39.35, 25.36) * mm});
            skLineSegment(sketch, "E1749", {"start": v(-39.35, 25.36) * mm, "end": v(-39.46, 25.75) * mm});
            skLineSegment(sketch, "E1750", {"start": v(-39.46, 25.75) * mm, "end": v(-39.55, 26.16) * mm});
            skLineSegment(sketch, "E1751", {"start": v(-39.55, 26.16) * mm, "end": v(-39.63, 26.57) * mm});
            skLineSegment(sketch, "E1752", {"start": v(-39.63, 26.57) * mm, "end": v(-39.7, 27) * mm});
            skLineSegment(sketch, "E1753", {"start": v(-39.7, 27) * mm, "end": v(-39.74, 27.32) * mm});
            skLineSegment(sketch, "E1754", {"start": v(-39.74, 27.32) * mm, "end": v(-37.68, 28.64) * mm});
            skLineSegment(sketch, "E1755", {"start": v(-37.68, 28.64) * mm, "end": v(-37.4, 28.47) * mm});
            skLineSegment(sketch, "E1756", {"start": v(-37.4, 28.47) * mm, "end": v(-37.05, 28.23) * mm});
            skLineSegment(sketch, "E1757", {"start": v(-37.05, 28.23) * mm, "end": v(-36.7, 27.99) * mm});
            skLineSegment(sketch, "E1758", {"start": v(-36.7, 27.99) * mm, "end": v(-36.38, 27.74) * mm});
            skLineSegment(sketch, "E1759", {"start": v(-36.38, 27.74) * mm, "end": v(-36.06, 27.47) * mm});
            skLineSegment(sketch, "E1760", {"start": v(-36.06, 27.47) * mm, "end": v(-35.76, 27.2) * mm});
            skLineSegment(sketch, "E1761", {"start": v(-35.76, 27.2) * mm, "end": v(-35.48, 26.92) * mm});
            skLineSegment(sketch, "E1762", {"start": v(-35.48, 26.92) * mm, "end": v(-35.21, 26.63) * mm});
            skLineSegment(sketch, "E1763", {"start": v(-35.21, 26.63) * mm, "end": v(-35.09, 26.48) * mm});
            skLineSegment(sketch, "E1764", {"start": v(-35.09, 26.48) * mm, "end": v(-34.97, 26.33) * mm});
            skLineSegment(sketch, "E1765", {"start": v(-34.97, 26.33) * mm, "end": v(-34.86, 26.17) * mm});
            skLineSegment(sketch, "E1766", {"start": v(-34.86, 26.17) * mm, "end": v(-34.64, 26.18) * mm});
            skLineSegment(sketch, "E1767", {"start": v(-34.64, 26.18) * mm, "end": v(-34.5, 26.14) * mm});
            skLineSegment(sketch, "E1768", {"start": v(-34.5, 26.14) * mm, "end": v(-33.41, 26.56) * mm});
            skLineSegment(sketch, "E1769", {"start": v(-33.41, 26.56) * mm, "end": v(-32.38, 27.11) * mm});
            skLineSegment(sketch, "E1770", {"start": v(-32.38, 27.11) * mm, "end": v(-32.32, 27.24) * mm});
            skLineSegment(sketch, "E1771", {"start": v(-32.32, 27.24) * mm, "end": v(-32.17, 27.4) * mm});
            skLineSegment(sketch, "E1772", {"start": v(-32.17, 27.4) * mm, "end": v(-32.22, 27.59) * mm});
            skLineSegment(sketch, "E1773", {"start": v(-32.22, 27.59) * mm, "end": v(-32.26, 27.77) * mm});
            skLineSegment(sketch, "E1774", {"start": v(-32.26, 27.77) * mm, "end": v(-32.3, 27.97) * mm});
            skLineSegment(sketch, "E1775", {"start": v(-32.3, 27.97) * mm, "end": v(-32.34, 28.36) * mm});
            skLineSegment(sketch, "E1776", {"start": v(-32.34, 28.36) * mm, "end": v(-32.36, 28.75) * mm});
            skLineSegment(sketch, "E1777", {"start": v(-32.36, 28.75) * mm, "end": v(-32.37, 29.16) * mm});
            skLineSegment(sketch, "E1778", {"start": v(-32.37, 29.16) * mm, "end": v(-32.36, 29.57) * mm});
            skLineSegment(sketch, "E1779", {"start": v(-32.36, 29.57) * mm, "end": v(-32.34, 29.98) * mm});
            skLineSegment(sketch, "E1780", {"start": v(-32.34, 29.98) * mm, "end": v(-32.3, 30.4) * mm});
            skLineSegment(sketch, "E1781", {"start": v(-32.3, 30.4) * mm, "end": v(-32.24, 30.83) * mm});
            skLineSegment(sketch, "E1782", {"start": v(-32.24, 30.83) * mm, "end": v(-32.19, 31.15) * mm});
            skLineSegment(sketch, "E1783", {"start": v(-32.19, 31.15) * mm, "end": v(-29.84, 31.84) * mm});
            skLineSegment(sketch, "E1784", {"start": v(-29.84, 31.84) * mm, "end": v(-29.63, 31.6) * mm});
            skLineSegment(sketch, "E1785", {"start": v(-29.63, 31.6) * mm, "end": v(-29.35, 31.27) * mm});
            skLineSegment(sketch, "E1786", {"start": v(-29.35, 31.27) * mm, "end": v(-29.09, 30.94) * mm});
            skLineSegment(sketch, "E1787", {"start": v(-29.09, 30.94) * mm, "end": v(-28.84, 30.6) * mm});
            skLineSegment(sketch, "E1788", {"start": v(-28.84, 30.6) * mm, "end": v(-28.61, 30.26) * mm});
            skLineSegment(sketch, "E1789", {"start": v(-28.61, 30.26) * mm, "end": v(-28.4, 29.92) * mm});
            skLineSegment(sketch, "E1790", {"start": v(-28.4, 29.92) * mm, "end": v(-28.2, 29.57) * mm});
            skLineSegment(sketch, "E1791", {"start": v(-28.2, 29.57) * mm, "end": v(-28.04, 29.21) * mm});
            skLineSegment(sketch, "E1792", {"start": v(-28.04, 29.21) * mm, "end": v(-27.96, 29.04) * mm});
            skLineSegment(sketch, "E1793", {"start": v(-27.96, 29.04) * mm, "end": v(-27.9, 28.86) * mm});
            skLineSegment(sketch, "E1794", {"start": v(-27.9, 28.86) * mm, "end": v(-27.84, 28.67) * mm});
            skLineSegment(sketch, "E1795", {"start": v(-27.84, 28.67) * mm, "end": v(-27.62, 28.62) * mm});
            skLineSegment(sketch, "E1796", {"start": v(-27.62, 28.62) * mm, "end": v(-27.5, 28.54) * mm});
            skLineSegment(sketch, "E1797", {"start": v(-27.5, 28.54) * mm, "end": v(-26.33, 28.64) * mm});
            skLineSegment(sketch, "E1798", {"start": v(-26.33, 28.64) * mm, "end": v(-25.18, 28.88) * mm});
            skLineSegment(sketch, "E1799", {"start": v(-25.18, 28.88) * mm, "end": v(-25.1, 28.98) * mm});
            skLineSegment(sketch, "E1800", {"start": v(-25.1, 28.98) * mm, "end": v(-24.9, 29.1) * mm});
            skLineSegment(sketch, "E1801", {"start": v(-24.9, 29.1) * mm, "end": v(-24.9, 29.29) * mm});
            skLineSegment(sketch, "E1802", {"start": v(-24.9, 29.29) * mm, "end": v(-24.88, 29.48) * mm});
            skLineSegment(sketch, "E1803", {"start": v(-24.88, 29.48) * mm, "end": v(-24.86, 29.67) * mm});
            skLineSegment(sketch, "E1804", {"start": v(-24.86, 29.67) * mm, "end": v(-24.8, 30.06) * mm});
            skLineSegment(sketch, "E1805", {"start": v(-24.8, 30.06) * mm, "end": v(-24.7, 30.45) * mm});
            skLineSegment(sketch, "E1806", {"start": v(-24.7, 30.45) * mm, "end": v(-24.6, 30.84) * mm});
            skLineSegment(sketch, "E1807", {"start": v(-24.6, 30.84) * mm, "end": v(-24.48, 31.23) * mm});
            skLineSegment(sketch, "E1808", {"start": v(-24.48, 31.23) * mm, "end": v(-24.33, 31.62) * mm});
            skLineSegment(sketch, "E1809", {"start": v(-24.33, 31.62) * mm, "end": v(-24.18, 32.01) * mm});
            skLineSegment(sketch, "E1810", {"start": v(-24.18, 32.01) * mm, "end": v(-24, 32.4) * mm});
            skLineSegment(sketch, "E1811", {"start": v(-24, 32.4) * mm, "end": v(-23.87, 32.7) * mm});
            skLineSegment(sketch, "E1812", {"start": v(-23.87, 32.7) * mm, "end": v(-21.42, 32.7) * mm});
            skLineSegment(sketch, "E1813", {"start": v(-21.42, 32.7) * mm, "end": v(-21.28, 32.4) * mm});
            skLineSegment(sketch, "E1814", {"start": v(-21.28, 32.4) * mm, "end": v(-21.1, 32.01) * mm});
            skLineSegment(sketch, "E1815", {"start": v(-21.1, 32.01) * mm, "end": v(-20.95, 31.62) * mm});
            skLineSegment(sketch, "E1816", {"start": v(-20.95, 31.62) * mm, "end": v(-20.8, 31.23) * mm});
            skLineSegment(sketch, "E1817", {"start": v(-20.8, 31.23) * mm, "end": v(-20.69, 30.84) * mm});
            skLineSegment(sketch, "E1818", {"start": v(-20.69, 30.84) * mm, "end": v(-20.58, 30.45) * mm});
            skLineSegment(sketch, "E1819", {"start": v(-20.58, 30.45) * mm, "end": v(-20.5, 30.06) * mm});
            skLineSegment(sketch, "E1820", {"start": v(-20.5, 30.06) * mm, "end": v(-20.43, 29.67) * mm});
            skLineSegment(sketch, "E1821", {"start": v(-20.43, 29.67) * mm, "end": v(-20.4, 29.48) * mm});
            skLineSegment(sketch, "E1822", {"start": v(-20.4, 29.48) * mm, "end": v(-20.39, 29.29) * mm});
            skLineSegment(sketch, "E1823", {"start": v(-20.39, 29.29) * mm, "end": v(-20.39, 29.1) * mm});
            skLineSegment(sketch, "E1824", {"start": v(-20.39, 29.1) * mm, "end": v(-20.2, 28.98) * mm});
            skLineSegment(sketch, "E1825", {"start": v(-20.2, 28.98) * mm, "end": v(-20.1, 28.88) * mm});
            skLineSegment(sketch, "E1826", {"start": v(-20.1, 28.88) * mm, "end": v(-18.95, 28.64) * mm});
            skLineSegment(sketch, "E1827", {"start": v(-18.95, 28.64) * mm, "end": v(-17.78, 28.54) * mm});
            skLineSegment(sketch, "E1828", {"start": v(-17.78, 28.54) * mm, "end": v(-17.66, 28.62) * mm});
            skLineSegment(sketch, "E1829", {"start": v(-17.66, 28.62) * mm, "end": v(-17.45, 28.67) * mm});
            skLineSegment(sketch, "E1830", {"start": v(-17.45, 28.67) * mm, "end": v(-17.4, 28.86) * mm});
            skLineSegment(sketch, "E1831", {"start": v(-17.4, 28.86) * mm, "end": v(-17.32, 29.04) * mm});
            skLineSegment(sketch, "E1832", {"start": v(-17.32, 29.04) * mm, "end": v(-17.25, 29.21) * mm});
            skLineSegment(sketch, "E1833", {"start": v(-17.25, 29.21) * mm, "end": v(-17.08, 29.57) * mm});
            skLineSegment(sketch, "E1834", {"start": v(-17.08, 29.57) * mm, "end": v(-16.88, 29.92) * mm});
            skLineSegment(sketch, "E1835", {"start": v(-16.88, 29.92) * mm, "end": v(-16.67, 30.26) * mm});
            skLineSegment(sketch, "E1836", {"start": v(-16.67, 30.26) * mm, "end": v(-16.44, 30.6) * mm});
            skLineSegment(sketch, "E1837", {"start": v(-16.44, 30.6) * mm, "end": v(-16.2, 30.94) * mm});
            skLineSegment(sketch, "E1838", {"start": v(-16.2, 30.94) * mm, "end": v(-15.94, 31.27) * mm});
            skLineSegment(sketch, "E1839", {"start": v(-15.94, 31.27) * mm, "end": v(-15.66, 31.6) * mm});
            skLineSegment(sketch, "E1840", {"start": v(-15.66, 31.6) * mm, "end": v(-15.44, 31.84) * mm});
            skLineSegment(sketch, "E1841", {"start": v(-15.44, 31.84) * mm, "end": v(-13.1, 31.15) * mm});
            skLineSegment(sketch, "E1842", {"start": v(-13.1, 31.15) * mm, "end": v(-13.05, 30.83) * mm});
            skLineSegment(sketch, "E1843", {"start": v(-13.05, 30.83) * mm, "end": v(-12.99, 30.4) * mm});
            skLineSegment(sketch, "E1844", {"start": v(-12.99, 30.4) * mm, "end": v(-12.95, 29.98) * mm});
            skLineSegment(sketch, "E1845", {"start": v(-12.95, 29.98) * mm, "end": v(-12.92, 29.57) * mm});
            skLineSegment(sketch, "E1846", {"start": v(-12.92, 29.57) * mm, "end": v(-12.91, 29.16) * mm});
            skLineSegment(sketch, "E1847", {"start": v(-12.91, 29.16) * mm, "end": v(-12.92, 28.75) * mm});
            skLineSegment(sketch, "E1848", {"start": v(-12.92, 28.75) * mm, "end": v(-12.95, 28.36) * mm});
            skLineSegment(sketch, "E1849", {"start": v(-12.95, 28.36) * mm, "end": v(-13, 27.97) * mm});
            skLineSegment(sketch, "E1850", {"start": v(-13, 27.97) * mm, "end": v(-13.03, 27.77) * mm});
            skLineSegment(sketch, "E1851", {"start": v(-13.03, 27.77) * mm, "end": v(-13.07, 27.59) * mm});
            skLineSegment(sketch, "E1852", {"start": v(-13.07, 27.59) * mm, "end": v(-13.12, 27.4) * mm});
            skLineSegment(sketch, "E1853", {"start": v(-13.12, 27.4) * mm, "end": v(-12.97, 27.24) * mm});
            skLineSegment(sketch, "E1854", {"start": v(-12.97, 27.24) * mm, "end": v(-12.9, 27.11) * mm});
            skLineSegment(sketch, "E1855", {"start": v(-12.9, 27.11) * mm, "end": v(-11.87, 26.56) * mm});
            skLineSegment(sketch, "E1856", {"start": v(-11.87, 26.56) * mm, "end": v(-10.78, 26.14) * mm});
            skLineSegment(sketch, "E1857", {"start": v(-10.78, 26.14) * mm, "end": v(-10.64, 26.18) * mm});
            skLineSegment(sketch, "E1858", {"start": v(-10.64, 26.18) * mm, "end": v(-10.42, 26.17) * mm});
            skLineSegment(sketch, "E1859", {"start": v(-10.42, 26.17) * mm, "end": v(-10.31, 26.33) * mm});
            skLineSegment(sketch, "E1860", {"start": v(-10.31, 26.33) * mm, "end": v(-10.2, 26.48) * mm});
            skLineSegment(sketch, "E1861", {"start": v(-10.2, 26.48) * mm, "end": v(-10.07, 26.63) * mm});
            skLineSegment(sketch, "E1862", {"start": v(-10.07, 26.63) * mm, "end": v(-9.8, 26.92) * mm});
            skLineSegment(sketch, "E1863", {"start": v(-9.8, 26.92) * mm, "end": v(-9.53, 27.2) * mm});
            skLineSegment(sketch, "E1864", {"start": v(-9.53, 27.2) * mm, "end": v(-9.23, 27.47) * mm});
            skLineSegment(sketch, "E1865", {"start": v(-9.23, 27.47) * mm, "end": v(-8.9, 27.74) * mm});
            skLineSegment(sketch, "E1866", {"start": v(-8.9, 27.74) * mm, "end": v(-8.58, 27.99) * mm});
            skLineSegment(sketch, "E1867", {"start": v(-8.58, 27.99) * mm, "end": v(-8.24, 28.23) * mm});
            skLineSegment(sketch, "E1868", {"start": v(-8.24, 28.23) * mm, "end": v(-7.88, 28.47) * mm});
            skLineSegment(sketch, "E1869", {"start": v(-7.88, 28.47) * mm, "end": v(-7.6, 28.64) * mm});
            skLineSegment(sketch, "E1870", {"start": v(-7.6, 28.64) * mm, "end": v(-5.55, 27.32) * mm});
            skLineSegment(sketch, "E1871", {"start": v(-5.55, 27.32) * mm, "end": v(-5.59, 27) * mm});
            skLineSegment(sketch, "E1872", {"start": v(-5.59, 27) * mm, "end": v(-5.65, 26.57) * mm});
            skLineSegment(sketch, "E1873", {"start": v(-5.65, 26.57) * mm, "end": v(-5.73, 26.16) * mm});
            skLineSegment(sketch, "E1874", {"start": v(-5.73, 26.16) * mm, "end": v(-5.83, 25.75) * mm});
            skLineSegment(sketch, "E1875", {"start": v(-5.83, 25.75) * mm, "end": v(-5.93, 25.36) * mm});
            skLineSegment(sketch, "E1876", {"start": v(-5.93, 25.36) * mm, "end": v(-6.05, 24.97) * mm});
            skLineSegment(sketch, "E1877", {"start": v(-6.05, 24.97) * mm, "end": v(-6.2, 24.6) * mm});
            skLineSegment(sketch, "E1878", {"start": v(-6.2, 24.6) * mm, "end": v(-6.35, 24.24) * mm});
            skLineSegment(sketch, "E1879", {"start": v(-6.35, 24.24) * mm, "end": v(-6.43, 24.06) * mm});
            skLineSegment(sketch, "E1880", {"start": v(-6.43, 24.06) * mm, "end": v(-6.52, 23.9) * mm});
            skLineSegment(sketch, "E1881", {"start": v(-6.52, 23.9) * mm, "end": v(-6.62, 23.73) * mm});
            skLineSegment(sketch, "E1882", {"start": v(-6.62, 23.73) * mm, "end": v(-6.52, 23.53) * mm});
            skLineSegment(sketch, "E1883", {"start": v(-6.52, 23.53) * mm, "end": v(-6.5, 23.4) * mm});
            skLineSegment(sketch, "E1884", {"start": v(-6.5, 23.4) * mm, "end": v(-5.66, 22.57) * mm});
            skLineSegment(sketch, "E1885", {"start": v(-5.66, 22.57) * mm, "end": v(-4.73, 21.86) * mm});
            skLineSegment(sketch, "E1886", {"start": v(-4.73, 21.86) * mm, "end": v(-4.6, 21.86) * mm});
            skLineSegment(sketch, "E1887", {"start": v(-4.6, 21.86) * mm, "end": v(-4.38, 21.79) * mm});
            skLineSegment(sketch, "E1888", {"start": v(-4.38, 21.79) * mm, "end": v(-4.23, 21.9) * mm});
            skLineSegment(sketch, "E1889", {"start": v(-4.23, 21.9) * mm, "end": v(-4.08, 22.02) * mm});
            skLineSegment(sketch, "E1890", {"start": v(-4.08, 22.02) * mm, "end": v(-3.92, 22.13) * mm});
            skLineSegment(sketch, "E1891", {"start": v(-3.92, 22.13) * mm, "end": v(-3.58, 22.34) * mm});
            skLineSegment(sketch, "E1892", {"start": v(-3.58, 22.34) * mm, "end": v(-3.23, 22.53) * mm});
            skLineSegment(sketch, "E1893", {"start": v(-3.23, 22.53) * mm, "end": v(-2.87, 22.7) * mm});
            skLineSegment(sketch, "E1894", {"start": v(-2.87, 22.7) * mm, "end": v(-2.49, 22.86) * mm});
            skLineSegment(sketch, "E1895", {"start": v(-2.49, 22.86) * mm, "end": v(-2.1, 23.01) * mm});
            skLineSegment(sketch, "E1896", {"start": v(-2.1, 23.01) * mm, "end": v(-1.7, 23.15) * mm});
            skLineSegment(sketch, "E1897", {"start": v(-1.7, 23.15) * mm, "end": v(-1.3, 23.28) * mm});
            skLineSegment(sketch, "E1898", {"start": v(-1.3, 23.28) * mm, "end": v(-0.98, 23.36) * mm});
            skLineSegment(sketch, "E1899", {"start": v(-0.98, 23.36) * mm, "end": v(0.62, 21.51) * mm});
            skLineSegment(sketch, "E1900", {"start": v(0.62, 21.51) * mm, "end": v(0.49, 21.22) * mm});
            skLineSegment(sketch, "E1901", {"start": v(0.49, 21.22) * mm, "end": v(0.3, 20.83) * mm});
            skLineSegment(sketch, "E1902", {"start": v(0.3, 20.83) * mm, "end": v(0.11, 20.46) * mm});
            skLineSegment(sketch, "E1903", {"start": v(0.11, 20.46) * mm, "end": v(-0.09, 20.1) * mm});
            skLineSegment(sketch, "E1904", {"start": v(-0.09, 20.1) * mm, "end": v(-0.3, 19.74) * mm});
            skLineSegment(sketch, "E1905", {"start": v(-0.3, 19.74) * mm, "end": v(-0.53, 19.4) * mm});
            skLineSegment(sketch, "E1906", {"start": v(-0.53, 19.4) * mm, "end": v(-0.77, 19.09) * mm});
            skLineSegment(sketch, "E1907", {"start": v(-0.77, 19.09) * mm, "end": v(-1.02, 18.78) * mm});
            skLineSegment(sketch, "E1908", {"start": v(-1.02, 18.78) * mm, "end": v(-1.15, 18.64) * mm});
            skLineSegment(sketch, "E1909", {"start": v(-1.15, 18.64) * mm, "end": v(-1.28, 18.5) * mm});
            skLineSegment(sketch, "E1910", {"start": v(-1.28, 18.5) * mm, "end": v(-1.43, 18.37) * mm});
            skLineSegment(sketch, "E1911", {"start": v(-1.43, 18.37) * mm, "end": v(-1.39, 18.16) * mm});
            skLineSegment(sketch, "E1912", {"start": v(-1.39, 18.16) * mm, "end": v(-1.4, 18.02) * mm});
            skLineSegment(sketch, "E1913", {"start": v(-1.4, 18.02) * mm, "end": v(-0.83, 17) * mm});
            skLineSegment(sketch, "E1914", {"start": v(-0.83, 17) * mm, "end": v(-0.14, 16.05) * mm});
            skLineSegment(sketch, "E1915", {"start": v(-0.14, 16.05) * mm, "end": v(0, 16) * mm});
            skLineSegment(sketch, "E1916", {"start": v(0, 16) * mm, "end": v(0.18, 15.88) * mm});
            skLineSegment(sketch, "E1917", {"start": v(0.18, 15.88) * mm, "end": v(0.35, 15.96) * mm});
            skLineSegment(sketch, "E1918", {"start": v(0.35, 15.96) * mm, "end": v(0.54, 16.02) * mm});
            skLineSegment(sketch, "E1919", {"start": v(0.54, 16.02) * mm, "end": v(0.72, 16.08) * mm});
            skLineSegment(sketch, "E1920", {"start": v(0.72, 16.08) * mm, "end": v(1.1, 16.18) * mm});
            skLineSegment(sketch, "E1921", {"start": v(1.1, 16.18) * mm, "end": v(1.5, 16.27) * mm});
            skLineSegment(sketch, "E1922", {"start": v(1.5, 16.27) * mm, "end": v(1.89, 16.33) * mm});
            skLineSegment(sketch, "E1923", {"start": v(1.89, 16.33) * mm, "end": v(2.3, 16.38) * mm});
            skLineSegment(sketch, "E1924", {"start": v(2.3, 16.38) * mm, "end": v(2.71, 16.41) * mm});
            skLineSegment(sketch, "E1925", {"start": v(2.71, 16.41) * mm, "end": v(3.13, 16.43) * mm});
            skLineSegment(sketch, "E1926", {"start": v(3.13, 16.43) * mm, "end": v(3.56, 16.44) * mm});
            skLineSegment(sketch, "E1927", {"start": v(3.56, 16.44) * mm, "end": v(3.88, 16.43) * mm});
            skLineSegment(sketch, "E1928", {"start": v(3.88, 16.43) * mm, "end": v(4.9, 14.2) * mm});
            skLineSegment(sketch, "E1929", {"start": v(4.9, 14.2) * mm, "end": v(4.7, 13.96) * mm});
            skLineSegment(sketch, "E1930", {"start": v(4.7, 13.96) * mm, "end": v(4.4, 13.64) * mm});
            skLineSegment(sketch, "E1931", {"start": v(4.4, 13.64) * mm, "end": v(4.12, 13.34) * mm});
            skLineSegment(sketch, "E1932", {"start": v(4.12, 13.34) * mm, "end": v(3.82, 13.05) * mm});
            skLineSegment(sketch, "E1933", {"start": v(3.82, 13.05) * mm, "end": v(3.52, 12.77) * mm});
            skLineSegment(sketch, "E1934", {"start": v(3.52, 12.77) * mm, "end": v(3.2, 12.51) * mm});
            skLineSegment(sketch, "E1935", {"start": v(3.2, 12.51) * mm, "end": v(2.89, 12.27) * mm});
            skLineSegment(sketch, "E1936", {"start": v(2.89, 12.27) * mm, "end": v(2.56, 12.05) * mm});
            skLineSegment(sketch, "E1937", {"start": v(2.56, 12.05) * mm, "end": v(2.4, 11.95) * mm});
            skLineSegment(sketch, "E1938", {"start": v(2.4, 11.95) * mm, "end": v(2.23, 11.86) * mm});
            skLineSegment(sketch, "E1939", {"start": v(2.23, 11.86) * mm, "end": v(2.05, 11.77) * mm});
            skLineSegment(sketch, "E1940", {"start": v(2.05, 11.77) * mm, "end": v(2.03, 11.55) * mm});
            skLineSegment(sketch, "E1941", {"start": v(2.03, 11.55) * mm, "end": v(1.97, 11.43) * mm});
            skLineSegment(sketch, "E1942", {"start": v(1.97, 11.43) * mm, "end": v(2.24, 10.28) * mm});
            skLineSegment(sketch, "E1943", {"start": v(2.24, 10.28) * mm, "end": v(2.63, 9.18) * mm});
            skLineSegment(sketch, "E1944", {"start": v(2.63, 9.18) * mm, "end": v(2.75, 9.1) * mm});
            skLineSegment(sketch, "E1945", {"start": v(2.75, 9.1) * mm, "end": v(2.89, 8.93) * mm});
            skLineSegment(sketch, "E1946", {"start": v(2.89, 8.93) * mm, "end": v(3.08, 8.95) * mm});
            skLineSegment(sketch, "E1947", {"start": v(3.08, 8.95) * mm, "end": v(3.27, 8.96) * mm});
            skLineSegment(sketch, "E1948", {"start": v(3.27, 8.96) * mm, "end": v(3.47, 8.97) * mm});
            skLineSegment(sketch, "E1949", {"start": v(3.47, 8.97) * mm, "end": v(3.86, 8.96) * mm});
            skLineSegment(sketch, "E1950", {"start": v(3.86, 8.96) * mm, "end": v(4.26, 8.93) * mm});
            skLineSegment(sketch, "E1951", {"start": v(4.26, 8.93) * mm, "end": v(4.66, 8.88) * mm});
            skLineSegment(sketch, "E1952", {"start": v(4.66, 8.88) * mm, "end": v(5.06, 8.81) * mm});
            skLineSegment(sketch, "E1953", {"start": v(5.06, 8.81) * mm, "end": v(5.47, 8.73) * mm});
            skLineSegment(sketch, "E1954", {"start": v(5.47, 8.73) * mm, "end": v(5.88, 8.63) * mm});
            skLineSegment(sketch, "E1955", {"start": v(5.88, 8.63) * mm, "end": v(6.3, 8.51) * mm});
            skLineSegment(sketch, "E1956", {"start": v(6.3, 8.51) * mm, "end": v(6.6, 8.42) * mm});
            skLineSegment(sketch, "E1957", {"start": v(6.6, 8.42) * mm, "end": v(6.95, 6) * mm});
            skLineSegment(sketch, "E1958", {"start": v(6.95, 6) * mm, "end": v(6.68, 5.82) * mm});
            skLineSegment(sketch, "E1959", {"start": v(6.68, 5.82) * mm, "end": v(6.32, 5.59) * mm});
            skLineSegment(sketch, "E1960", {"start": v(6.32, 5.59) * mm, "end": v(5.95, 5.38) * mm});
            skLineSegment(sketch, "E1961", {"start": v(5.95, 5.38) * mm, "end": v(5.58, 5.18) * mm});
            skLineSegment(sketch, "E1962", {"start": v(5.58, 5.18) * mm, "end": v(5.22, 5) * mm});
            skLineSegment(sketch, "E1963", {"start": v(5.22, 5) * mm, "end": v(4.84, 4.84) * mm});
            skLineSegment(sketch, "E1964", {"start": v(4.84, 4.84) * mm, "end": v(4.47, 4.7) * mm});
            skLineSegment(sketch, "E1965", {"start": v(4.47, 4.7) * mm, "end": v(4.1, 4.58) * mm});
            skLineSegment(sketch, "E1966", {"start": v(4.1, 4.58) * mm, "end": v(3.9, 4.53) * mm});
            skLineSegment(sketch, "E1967", {"start": v(3.9, 4.53) * mm, "end": v(3.72, 4.49) * mm});
            skLineSegment(sketch, "E1968", {"start": v(3.72, 4.49) * mm, "end": v(3.53, 4.46) * mm});
            skLineSegment(sketch, "E1969", {"start": v(3.53, 4.46) * mm, "end": v(3.45, 4.25) * mm});
            skLineSegment(sketch, "E1970", {"start": v(3.45, 4.25) * mm, "end": v(3.36, 4.15) * mm});
            skLineSegment(sketch, "E1971", {"start": v(3.36, 4.15) * mm, "end": v(3.29, 2.98) * mm});
            skLineSegment(sketch, "E1972", {"start": v(3.29, 2.98) * mm, "end": v(3.36, 1.8) * mm});
            skLineSegment(sketch, "E1973", {"start": v(3.36, 1.8) * mm, "end": v(3.45, 1.7) * mm});
            skLineSegment(sketch, "E1974", {"start": v(3.45, 1.7) * mm, "end": v(3.53, 1.5) * mm});
            skLineSegment(sketch, "E1975", {"start": v(3.53, 1.5) * mm, "end": v(3.72, 1.46) * mm});
            skLineSegment(sketch, "E1976", {"start": v(3.72, 1.46) * mm, "end": v(3.9, 1.42) * mm});
            skLineSegment(sketch, "E1977", {"start": v(3.9, 1.42) * mm, "end": v(4.1, 1.37) * mm});
            skLineSegment(sketch, "E1978", {"start": v(4.1, 1.37) * mm, "end": v(4.47, 1.25) * mm});
            skLineSegment(sketch, "E1979", {"start": v(4.47, 1.25) * mm, "end": v(4.84, 1.1) * mm});
            skLineSegment(sketch, "E1980", {"start": v(4.84, 1.1) * mm, "end": v(5.22, 0.95) * mm});
            skLineSegment(sketch, "E1981", {"start": v(5.22, 0.95) * mm, "end": v(5.58, 0.77) * mm});
            skLineSegment(sketch, "E1982", {"start": v(5.58, 0.77) * mm, "end": v(5.95, 0.57) * mm});
            skLineSegment(sketch, "E1983", {"start": v(5.95, 0.57) * mm, "end": v(6.32, 0.36) * mm});
            skLineSegment(sketch, "E1984", {"start": v(6.32, 0.36) * mm, "end": v(6.68, 0.14) * mm});
            skLineSegment(sketch, "E1985", {"start": v(6.68, 0.14) * mm, "end": v(6.95, -0.04) * mm});
            skLineSegment(sketch, "E1986", {"start": v(6.95, -0.04) * mm, "end": v(6.6, -2.46) * mm});
            skLineSegment(sketch, "E1987", {"start": v(6.6, -2.46) * mm, "end": v(6.3, -2.56) * mm});
            skLineSegment(sketch, "E1988", {"start": v(6.3, -2.56) * mm, "end": v(5.88, -2.68) * mm});
            skLineSegment(sketch, "E1989", {"start": v(5.88, -2.68) * mm, "end": v(5.47, -2.78) * mm});
            skLineSegment(sketch, "E1990", {"start": v(5.47, -2.78) * mm, "end": v(5.06, -2.86) * mm});
            skLineSegment(sketch, "E1991", {"start": v(5.06, -2.86) * mm, "end": v(4.66, -2.93) * mm});
            skLineSegment(sketch, "E1992", {"start": v(4.66, -2.93) * mm, "end": v(4.26, -2.98) * mm});
            skLineSegment(sketch, "E1993", {"start": v(4.26, -2.98) * mm, "end": v(3.86, -3) * mm});
            skLineSegment(sketch, "E1994", {"start": v(3.86, -3) * mm, "end": v(3.47, -3.02) * mm});
            skLineSegment(sketch, "E1995", {"start": v(3.47, -3.02) * mm, "end": v(3.27, -3.01) * mm});
            skLineSegment(sketch, "E1996", {"start": v(3.27, -3.01) * mm, "end": v(3.08, -3) * mm});
            skLineSegment(sketch, "E1997", {"start": v(3.08, -3) * mm, "end": v(2.89, -2.98) * mm});
            skLineSegment(sketch, "E1998", {"start": v(2.89, -2.98) * mm, "end": v(2.75, -3.15) * mm});
            skLineSegment(sketch, "E1999", {"start": v(2.75, -3.15) * mm, "end": v(2.63, -3.22) * mm});
            skLineSegment(sketch, "E2000", {"start": v(2.63, -3.22) * mm, "end": v(2.24, -4.33) * mm});
            skLineSegment(sketch, "E2001", {"start": v(2.24, -4.33) * mm, "end": v(1.97, -5.47) * mm});
            skLineSegment(sketch, "E2002", {"start": v(1.97, -5.47) * mm, "end": v(2.03, -5.6) * mm});
            skLineSegment(sketch, "E2003", {"start": v(2.03, -5.6) * mm, "end": v(2.05, -5.82) * mm});
            skLineSegment(sketch, "E2004", {"start": v(2.05, -5.82) * mm, "end": v(2.23, -5.9) * mm});
            skLineSegment(sketch, "E2005", {"start": v(2.23, -5.9) * mm, "end": v(2.4, -6) * mm});
            skLineSegment(sketch, "E2006", {"start": v(2.4, -6) * mm, "end": v(2.56, -6.1) * mm});
            skLineSegment(sketch, "E2007", {"start": v(2.56, -6.1) * mm, "end": v(2.89, -6.32) * mm});
            skLineSegment(sketch, "E2008", {"start": v(2.89, -6.32) * mm, "end": v(3.2, -6.56) * mm});
            skLineSegment(sketch, "E2009", {"start": v(3.2, -6.56) * mm, "end": v(3.52, -6.82) * mm});
            skLineSegment(sketch, "E2010", {"start": v(3.52, -6.82) * mm, "end": v(3.82, -7.1) * mm});
            skLineSegment(sketch, "E2011", {"start": v(3.82, -7.1) * mm, "end": v(4.12, -7.38) * mm});
            skLineSegment(sketch, "E2012", {"start": v(4.12, -7.38) * mm, "end": v(4.4, -7.7) * mm});
            skLineSegment(sketch, "E2013", {"start": v(4.4, -7.7) * mm, "end": v(4.7, -8) * mm});
            skLineSegment(sketch, "E2014", {"start": v(4.7, -8) * mm, "end": v(4.9, -8.26) * mm});
            skLineSegment(sketch, "E2015", {"start": v(4.9, -8.26) * mm, "end": v(3.88, -10.48) * mm});
            skLineSegment(sketch, "E2016", {"start": v(3.88, -10.48) * mm, "end": v(3.56, -10.49) * mm});
            skLineSegment(sketch, "E2017", {"start": v(3.56, -10.49) * mm, "end": v(3.13, -10.48) * mm});
            skLineSegment(sketch, "E2018", {"start": v(3.13, -10.48) * mm, "end": v(2.71, -10.46) * mm});
            skLineSegment(sketch, "E2019", {"start": v(2.71, -10.46) * mm, "end": v(2.3, -10.43) * mm});
            skLineSegment(sketch, "E2020", {"start": v(2.3, -10.43) * mm, "end": v(1.89, -10.38) * mm});
            skLineSegment(sketch, "E2021", {"start": v(1.89, -10.38) * mm, "end": v(1.5, -10.31) * mm});
            skLineSegment(sketch, "E2022", {"start": v(1.5, -10.31) * mm, "end": v(1.1, -10.23) * mm});
            skLineSegment(sketch, "E2023", {"start": v(1.1, -10.23) * mm, "end": v(0.72, -10.13) * mm});
            skLineSegment(sketch, "E2024", {"start": v(0.72, -10.13) * mm, "end": v(0.54, -10.07) * mm});
            skLineSegment(sketch, "E2025", {"start": v(0.54, -10.07) * mm, "end": v(0.35, -10) * mm});
            skLineSegment(sketch, "E2026", {"start": v(0.35, -10) * mm, "end": v(0.18, -9.93) * mm});
            skLineSegment(sketch, "E2027", {"start": v(0.18, -9.93) * mm, "end": v(0, -10.05) * mm});
            skLineSegment(sketch, "E2028", {"start": v(0, -10.05) * mm, "end": v(-0.14, -10.1) * mm});
            skLineSegment(sketch, "E2029", {"start": v(-0.14, -10.1) * mm, "end": v(-0.83, -11.04) * mm});
            skLineSegment(sketch, "E2030", {"start": v(-0.83, -11.04) * mm, "end": v(-1.4, -12.07) * mm});
            skLineSegment(sketch, "E2031", {"start": v(-1.4, -12.07) * mm, "end": v(-1.39, -12.2) * mm});
            skLineSegment(sketch, "E2032", {"start": v(-1.39, -12.2) * mm, "end": v(-1.43, -12.42) * mm});
            skLineSegment(sketch, "E2033", {"start": v(-1.43, -12.42) * mm, "end": v(-1.28, -12.55) * mm});
            skLineSegment(sketch, "E2034", {"start": v(-1.28, -12.55) * mm, "end": v(-1.15, -12.69) * mm});
            skLineSegment(sketch, "E2035", {"start": v(-1.15, -12.69) * mm, "end": v(-1.02, -12.83) * mm});
            skLineSegment(sketch, "E2036", {"start": v(-1.02, -12.83) * mm, "end": v(-0.77, -13.13) * mm});
            skLineSegment(sketch, "E2037", {"start": v(-0.77, -13.13) * mm, "end": v(-0.53, -13.46) * mm});
            skLineSegment(sketch, "E2038", {"start": v(-0.53, -13.46) * mm, "end": v(-0.3, -13.8) * mm});
            skLineSegment(sketch, "E2039", {"start": v(-0.3, -13.8) * mm, "end": v(-0.09, -14.14) * mm});
            skLineSegment(sketch, "E2040", {"start": v(-0.09, -14.14) * mm, "end": v(0.11, -14.5) * mm});
            skLineSegment(sketch, "E2041", {"start": v(0.11, -14.5) * mm, "end": v(0.3, -14.88) * mm});
            skLineSegment(sketch, "E2042", {"start": v(0.3, -14.88) * mm, "end": v(0.49, -15.26) * mm});
            skLineSegment(sketch, "E2043", {"start": v(0.49, -15.26) * mm, "end": v(0.62, -15.56) * mm});
            skLineSegment(sketch, "E2044", {"start": v(0.62, -15.56) * mm, "end": v(-0.98, -17.41) * mm});
            skLineSegment(sketch, "E2045", {"start": v(-0.98, -17.41) * mm, "end": v(-1.3, -17.32) * mm});
            skLineSegment(sketch, "E2046", {"start": v(-1.3, -17.32) * mm, "end": v(-1.7, -17.2) * mm});
            skLineSegment(sketch, "E2047", {"start": v(-1.7, -17.2) * mm, "end": v(-2.1, -17.06) * mm});
            skLineSegment(sketch, "E2048", {"start": v(-2.1, -17.06) * mm, "end": v(-2.49, -16.91) * mm});
            skLineSegment(sketch, "E2049", {"start": v(-2.49, -16.91) * mm, "end": v(-2.87, -16.75) * mm});
            skLineSegment(sketch, "E2050", {"start": v(-2.87, -16.75) * mm, "end": v(-3.23, -16.58) * mm});
            skLineSegment(sketch, "E2051", {"start": v(-3.23, -16.58) * mm, "end": v(-3.58, -16.39) * mm});
            skLineSegment(sketch, "E2052", {"start": v(-3.58, -16.39) * mm, "end": v(-3.92, -16.18) * mm});
            skLineSegment(sketch, "E2053", {"start": v(-3.92, -16.18) * mm, "end": v(-4.08, -16.07) * mm});
            skLineSegment(sketch, "E2054", {"start": v(-4.08, -16.07) * mm, "end": v(-4.23, -15.96) * mm});
            skLineSegment(sketch, "E2055", {"start": v(-4.23, -15.96) * mm, "end": v(-4.38, -15.83) * mm});
            skLineSegment(sketch, "E2056", {"start": v(-4.38, -15.83) * mm, "end": v(-4.6, -15.9) * mm});
            skLineSegment(sketch, "E2057", {"start": v(-4.6, -15.9) * mm, "end": v(-4.73, -15.9) * mm});
            skLineSegment(sketch, "E2058", {"start": v(-4.73, -15.9) * mm, "end": v(-5.66, -16.62) * mm});
            skLineSegment(sketch, "E2059", {"start": v(-5.66, -16.62) * mm, "end": v(-6.5, -17.44) * mm});
            skLineSegment(sketch, "E2060", {"start": v(-6.5, -17.44) * mm, "end": v(-6.52, -17.58) * mm});
            skLineSegment(sketch, "E2061", {"start": v(-6.52, -17.58) * mm, "end": v(-6.62, -17.78) * mm});
            skLineSegment(sketch, "E2062", {"start": v(-6.62, -17.78) * mm, "end": v(-6.52, -17.94) * mm});
            skLineSegment(sketch, "E2063", {"start": v(-6.52, -17.94) * mm, "end": v(-6.43, -18.1) * mm});
            skLineSegment(sketch, "E2064", {"start": v(-6.43, -18.1) * mm, "end": v(-6.35, -18.28) * mm});
            skLineSegment(sketch, "E2065", {"start": v(-6.35, -18.28) * mm, "end": v(-6.2, -18.65) * mm});
            skLineSegment(sketch, "E2066", {"start": v(-6.2, -18.65) * mm, "end": v(-6.05, -19.02) * mm});
            skLineSegment(sketch, "E2067", {"start": v(-6.05, -19.02) * mm, "end": v(-5.93, -19.4) * mm});
            skLineSegment(sketch, "E2068", {"start": v(-5.93, -19.4) * mm, "end": v(-5.83, -19.8) * mm});
            skLineSegment(sketch, "E2069", {"start": v(-5.83, -19.8) * mm, "end": v(-5.73, -20.2) * mm});
            skLineSegment(sketch, "E2070", {"start": v(-5.73, -20.2) * mm, "end": v(-5.65, -20.62) * mm});
            skLineSegment(sketch, "E2071", {"start": v(-5.65, -20.62) * mm, "end": v(-5.59, -21.04) * mm});
            skLineSegment(sketch, "E2072", {"start": v(-5.59, -21.04) * mm, "end": v(-5.55, -21.36) * mm});
            skLineSegment(sketch, "E2073", {"start": v(-5.55, -21.36) * mm, "end": v(-7.6, -22.69) * mm});
            skLineSegment(sketch, "E2074", {"start": v(-7.6, -22.69) * mm, "end": v(-7.88, -22.52) * mm});
            skLineSegment(sketch, "E2075", {"start": v(-7.88, -22.52) * mm, "end": v(-8.24, -22.28) * mm});
            skLineSegment(sketch, "E2076", {"start": v(-8.24, -22.28) * mm, "end": v(-8.58, -22.04) * mm});
            skLineSegment(sketch, "E2077", {"start": v(-8.58, -22.04) * mm, "end": v(-8.9, -21.78) * mm});
            skLineSegment(sketch, "E2078", {"start": v(-8.9, -21.78) * mm, "end": v(-9.23, -21.52) * mm});
            skLineSegment(sketch, "E2079", {"start": v(-9.23, -21.52) * mm, "end": v(-9.53, -21.25) * mm});
            skLineSegment(sketch, "E2080", {"start": v(-9.53, -21.25) * mm, "end": v(-9.8, -20.97) * mm});
            skLineSegment(sketch, "E2081", {"start": v(-9.8, -20.97) * mm, "end": v(-10.07, -20.68) * mm});
            skLineSegment(sketch, "E2082", {"start": v(-10.07, -20.68) * mm, "end": v(-10.2, -20.53) * mm});
            skLineSegment(sketch, "E2083", {"start": v(-10.2, -20.53) * mm, "end": v(-10.31, -20.38) * mm});
            skLineSegment(sketch, "E2084", {"start": v(-10.31, -20.38) * mm, "end": v(-10.42, -20.22) * mm});
            skLineSegment(sketch, "E2085", {"start": v(-10.42, -20.22) * mm, "end": v(-10.64, -20.22) * mm});
            skLineSegment(sketch, "E2086", {"start": v(-10.64, -20.22) * mm, "end": v(-10.78, -20.19) * mm});
            skLineSegment(sketch, "E2087", {"start": v(-10.78, -20.19) * mm, "end": v(-11.87, -20.61) * mm});
            skLineSegment(sketch, "E2088", {"start": v(-11.87, -20.61) * mm, "end": v(-12.9, -21.16) * mm});
            skLineSegment(sketch, "E2089", {"start": v(-12.9, -21.16) * mm, "end": v(-12.97, -21.29) * mm});
            skLineSegment(sketch, "E2090", {"start": v(-12.97, -21.29) * mm, "end": v(-13.12, -21.45) * mm});
            skLineSegment(sketch, "E2091", {"start": v(-13.12, -21.45) * mm, "end": v(-13.07, -21.63) * mm});
            skLineSegment(sketch, "E2092", {"start": v(-13.07, -21.63) * mm, "end": v(-13.03, -21.82) * mm});
            skLineSegment(sketch, "E2093", {"start": v(-13.03, -21.82) * mm, "end": v(-13, -22.01) * mm});
            skLineSegment(sketch, "E2094", {"start": v(-13, -22.01) * mm, "end": v(-12.95, -22.4) * mm});
            skLineSegment(sketch, "E2095", {"start": v(-12.95, -22.4) * mm, "end": v(-12.92, -22.8) * mm});
            skLineSegment(sketch, "E2096", {"start": v(-12.92, -22.8) * mm, "end": v(-12.91, -23.2) * mm});
            skLineSegment(sketch, "E2097", {"start": v(-12.91, -23.2) * mm, "end": v(-12.92, -23.62) * mm});
            skLineSegment(sketch, "E2098", {"start": v(-12.92, -23.62) * mm, "end": v(-12.95, -24.03) * mm});
            skLineSegment(sketch, "E2099", {"start": v(-12.95, -24.03) * mm, "end": v(-12.99, -24.45) * mm});
            skLineSegment(sketch, "E2100", {"start": v(-12.99, -24.45) * mm, "end": v(-13.05, -24.87) * mm});
            skLineSegment(sketch, "E2101", {"start": v(-13.05, -24.87) * mm, "end": v(-13.1, -25.2) * mm});
            skLineSegment(sketch, "E2102", {"start": v(-13.1, -25.2) * mm, "end": v(-15.44, -25.88) * mm});
            skLineSegment(sketch, "E2103", {"start": v(-15.44, -25.88) * mm, "end": v(-15.66, -25.64) * mm});
            skLineSegment(sketch, "E2104", {"start": v(-15.66, -25.64) * mm, "end": v(-15.94, -25.32) * mm});
            skLineSegment(sketch, "E2105", {"start": v(-15.94, -25.32) * mm, "end": v(-16.2, -24.99) * mm});
            skLineSegment(sketch, "E2106", {"start": v(-16.2, -24.99) * mm, "end": v(-16.44, -24.65) * mm});
            skLineSegment(sketch, "E2107", {"start": v(-16.44, -24.65) * mm, "end": v(-16.67, -24.31) * mm});
            skLineSegment(sketch, "E2108", {"start": v(-16.67, -24.31) * mm, "end": v(-16.88, -23.97) * mm});
            skLineSegment(sketch, "E2109", {"start": v(-16.88, -23.97) * mm, "end": v(-17.08, -23.62) * mm});
            skLineSegment(sketch, "E2110", {"start": v(-17.08, -23.62) * mm, "end": v(-17.25, -23.26) * mm});
            skLineSegment(sketch, "E2111", {"start": v(-17.25, -23.26) * mm, "end": v(-17.32, -23.08) * mm});
            skLineSegment(sketch, "E2112", {"start": v(-17.32, -23.08) * mm, "end": v(-17.4, -22.9) * mm});
            skLineSegment(sketch, "E2113", {"start": v(-17.4, -22.9) * mm, "end": v(-17.45, -22.72) * mm});
            skLineSegment(sketch, "E2114", {"start": v(-17.45, -22.72) * mm, "end": v(-17.66, -22.67) * mm});
            skLineSegment(sketch, "E2115", {"start": v(-17.66, -22.67) * mm, "end": v(-17.78, -22.6) * mm});
            skLineSegment(sketch, "E2116", {"start": v(-17.78, -22.6) * mm, "end": v(-18.95, -22.69) * mm});
            skLineSegment(sketch, "E2117", {"start": v(-18.95, -22.69) * mm, "end": v(-20.1, -22.92) * mm});
            skLineSegment(sketch, "E2118", {"start": v(-20.1, -22.92) * mm, "end": v(-20.2, -23.03) * mm});
            skLineSegment(sketch, "E2119", {"start": v(-20.2, -23.03) * mm, "end": v(-20.39, -23.14) * mm});
            skLineSegment(sketch, "E2120", {"start": v(-20.39, -23.14) * mm, "end": v(-20.39, -23.33) * mm});
            skLineSegment(sketch, "E2121", {"start": v(-20.39, -23.33) * mm, "end": v(-20.4, -23.53) * mm});
            skLineSegment(sketch, "E2122", {"start": v(-20.4, -23.53) * mm, "end": v(-20.43, -23.72) * mm});
            skLineSegment(sketch, "E2123", {"start": v(-20.43, -23.72) * mm, "end": v(-20.5, -24.1) * mm});
            skLineSegment(sketch, "E2124", {"start": v(-20.5, -24.1) * mm, "end": v(-20.58, -24.5) * mm});
            skLineSegment(sketch, "E2125", {"start": v(-20.58, -24.5) * mm, "end": v(-20.69, -24.89) * mm});
            skLineSegment(sketch, "E2126", {"start": v(-20.69, -24.89) * mm, "end": v(-20.8, -25.28) * mm});
            skLineSegment(sketch, "E2127", {"start": v(-20.8, -25.28) * mm, "end": v(-20.95, -25.67) * mm});
            skLineSegment(sketch, "E2128", {"start": v(-20.95, -25.67) * mm, "end": v(-21.1, -26.06) * mm});
            skLineSegment(sketch, "E2129", {"start": v(-21.1, -26.06) * mm, "end": v(-21.28, -26.45) * mm});
            skLineSegment(sketch, "E2130", {"start": v(-21.28, -26.45) * mm, "end": v(-21.42, -26.74) * mm});
            skLineSegment(sketch, "E2131", {"start": v(-21.42, -26.74) * mm, "end": v(-23.87, -26.74) * mm});
            skLineSegment(sketch, "E2132", {"start": v(-23.87, -26.74) * mm, "end": v(-24, -26.45) * mm});
            skLineSegment(sketch, "E2133", {"start": v(-24, -26.45) * mm, "end": v(-24.18, -26.06) * mm});
            skLineSegment(sketch, "E2134", {"start": v(-24.18, -26.06) * mm, "end": v(-24.33, -25.67) * mm});
            skLineSegment(sketch, "E2135", {"start": v(-24.33, -25.67) * mm, "end": v(-24.48, -25.28) * mm});
            skLineSegment(sketch, "E2136", {"start": v(-24.48, -25.28) * mm, "end": v(-24.6, -24.89) * mm});
            skLineSegment(sketch, "E2137", {"start": v(-24.6, -24.89) * mm, "end": v(-24.7, -24.5) * mm});
            skLineSegment(sketch, "E2138", {"start": v(-24.7, -24.5) * mm, "end": v(-24.8, -24.1) * mm});
            skLineSegment(sketch, "E2139", {"start": v(-24.8, -24.1) * mm, "end": v(-24.86, -23.72) * mm});
            skLineSegment(sketch, "E2140", {"start": v(-24.86, -23.72) * mm, "end": v(-24.88, -23.53) * mm});
            skLineSegment(sketch, "E2141", {"start": v(-24.88, -23.53) * mm, "end": v(-24.9, -23.33) * mm});
            skLineSegment(sketch, "E2142", {"start": v(-24.9, -23.33) * mm, "end": v(-24.9, -23.14) * mm});
            skLineSegment(sketch, "E2143", {"start": v(-24.9, -23.14) * mm, "end": v(-25.1, -23.03) * mm});
            skLineSegment(sketch, "E2144", {"start": v(-25.1, -23.03) * mm, "end": v(-25.18, -22.92) * mm});
            skLineSegment(sketch, "E2145", {"start": v(-25.18, -22.92) * mm, "end": v(-26.33, -22.69) * mm});
            skLineSegment(sketch, "E2146", {"start": v(-26.33, -22.69) * mm, "end": v(-27.5, -22.6) * mm});
            skLineSegment(sketch, "E2147", {"start": v(-27.5, -22.6) * mm, "end": v(-27.62, -22.67) * mm});
            skLineSegment(sketch, "E2148", {"start": v(-27.62, -22.67) * mm, "end": v(-27.84, -22.72) * mm});
            skLineSegment(sketch, "E2149", {"start": v(-27.84, -22.72) * mm, "end": v(-27.9, -22.9) * mm});
            skLineSegment(sketch, "E2150", {"start": v(-27.9, -22.9) * mm, "end": v(-27.96, -23.08) * mm});
            skLineSegment(sketch, "E2151", {"start": v(-27.96, -23.08) * mm, "end": v(-28.04, -23.26) * mm});
            skLineSegment(sketch, "E2152", {"start": v(-28.04, -23.26) * mm, "end": v(-28.2, -23.62) * mm});
            skLineSegment(sketch, "E2153", {"start": v(-28.2, -23.62) * mm, "end": v(-28.4, -23.97) * mm});
            skLineSegment(sketch, "E2154", {"start": v(-28.4, -23.97) * mm, "end": v(-28.61, -24.31) * mm});
            skLineSegment(sketch, "E2155", {"start": v(-28.61, -24.31) * mm, "end": v(-28.84, -24.65) * mm});
            skLineSegment(sketch, "E2156", {"start": v(-28.84, -24.65) * mm, "end": v(-29.09, -24.99) * mm});
            skLineSegment(sketch, "E2157", {"start": v(-29.09, -24.99) * mm, "end": v(-29.35, -25.32) * mm});
            skLineSegment(sketch, "E2158", {"start": v(-29.35, -25.32) * mm, "end": v(-29.63, -25.64) * mm});
            skLineSegment(sketch, "E2159", {"start": v(-29.63, -25.64) * mm, "end": v(-29.84, -25.88) * mm});
            skLineSegment(sketch, "E2160", {"start": v(-29.84, -25.88) * mm, "end": v(-32.19, -25.2) * mm});
            skLineSegment(sketch, "E2161", {"start": v(-32.19, -25.2) * mm, "end": v(-32.24, -24.87) * mm});
            skLineSegment(sketch, "E2162", {"start": v(-32.24, -24.87) * mm, "end": v(-32.3, -24.45) * mm});
            skLineSegment(sketch, "E2163", {"start": v(-32.3, -24.45) * mm, "end": v(-32.34, -24.03) * mm});
            skLineSegment(sketch, "E2164", {"start": v(-32.34, -24.03) * mm, "end": v(-32.36, -23.62) * mm});
            skLineSegment(sketch, "E2165", {"start": v(-32.36, -23.62) * mm, "end": v(-32.37, -23.2) * mm});
            skLineSegment(sketch, "E2166", {"start": v(-32.37, -23.2) * mm, "end": v(-32.36, -22.8) * mm});
            skLineSegment(sketch, "E2167", {"start": v(-32.36, -22.8) * mm, "end": v(-32.34, -22.4) * mm});
            skLineSegment(sketch, "E2168", {"start": v(-32.34, -22.4) * mm, "end": v(-32.3, -22.01) * mm});
            skLineSegment(sketch, "E2169", {"start": v(-32.3, -22.01) * mm, "end": v(-32.26, -21.82) * mm});
            skLineSegment(sketch, "E2170", {"start": v(-32.26, -21.82) * mm, "end": v(-32.22, -21.63) * mm});
            skLineSegment(sketch, "E2171", {"start": v(-32.22, -21.63) * mm, "end": v(-32.17, -21.45) * mm});
            skLineSegment(sketch, "E2172", {"start": v(-32.17, -21.45) * mm, "end": v(-32.32, -21.29) * mm});
            skLineSegment(sketch, "E2173", {"start": v(-32.32, -21.29) * mm, "end": v(-32.38, -21.16) * mm});
            skLineSegment(sketch, "E2174", {"start": v(-32.38, -21.16) * mm, "end": v(-33.41, -20.61) * mm});
            skLineSegment(sketch, "E2175", {"start": v(-33.41, -20.61) * mm, "end": v(-34.5, -20.19) * mm});
            skLineSegment(sketch, "E2176", {"start": v(-34.5, -20.19) * mm, "end": v(-34.64, -20.22) * mm});
            skLineSegment(sketch, "E2177", {"start": v(-34.64, -20.22) * mm, "end": v(-34.86, -20.22) * mm});
            skLineSegment(sketch, "E2178", {"start": v(-34.86, -20.22) * mm, "end": v(-34.97, -20.38) * mm});
            skLineSegment(sketch, "E2179", {"start": v(-34.97, -20.38) * mm, "end": v(-35.09, -20.53) * mm});
            skLineSegment(sketch, "E2180", {"start": v(-35.09, -20.53) * mm, "end": v(-35.21, -20.68) * mm});
            skLineSegment(sketch, "E2181", {"start": v(-35.21, -20.68) * mm, "end": v(-35.48, -20.97) * mm});
            skLineSegment(sketch, "E2182", {"start": v(-35.48, -20.97) * mm, "end": v(-35.76, -21.25) * mm});
            skLineSegment(sketch, "E2183", {"start": v(-35.76, -21.25) * mm, "end": v(-36.06, -21.52) * mm});
            skLineSegment(sketch, "E2184", {"start": v(-36.06, -21.52) * mm, "end": v(-36.38, -21.78) * mm});
            skLineSegment(sketch, "E2185", {"start": v(-36.38, -21.78) * mm, "end": v(-36.7, -22.04) * mm});
            skLineSegment(sketch, "E2186", {"start": v(-36.7, -22.04) * mm, "end": v(-37.05, -22.28) * mm});
            skLineSegment(sketch, "E2187", {"start": v(-37.05, -22.28) * mm, "end": v(-37.4, -22.52) * mm});
            skLineSegment(sketch, "E2188", {"start": v(-37.4, -22.52) * mm, "end": v(-37.68, -22.69) * mm});
            skLineSegment(sketch, "E2189", {"start": v(-37.68, -22.69) * mm, "end": v(-39.74, -21.36) * mm});
            skLineSegment(sketch, "E2190", {"start": v(-39.74, -21.36) * mm, "end": v(-39.7, -21.04) * mm});
            skLineSegment(sketch, "E2191", {"start": v(-39.7, -21.04) * mm, "end": v(-39.63, -20.62) * mm});
            skLineSegment(sketch, "E2192", {"start": v(-39.63, -20.62) * mm, "end": v(-39.55, -20.2) * mm});
            skLineSegment(sketch, "E2193", {"start": v(-39.55, -20.2) * mm, "end": v(-39.46, -19.8) * mm});
            skLineSegment(sketch, "E2194", {"start": v(-39.46, -19.8) * mm, "end": v(-39.35, -19.4) * mm});
            skLineSegment(sketch, "E2195", {"start": v(-39.35, -19.4) * mm, "end": v(-39.23, -19.02) * mm});
            skLineSegment(sketch, "E2196", {"start": v(-39.23, -19.02) * mm, "end": v(-39.1, -18.65) * mm});
            skLineSegment(sketch, "E2197", {"start": v(-39.1, -18.65) * mm, "end": v(-38.94, -18.28) * mm});
            skLineSegment(sketch, "E2198", {"start": v(-38.94, -18.28) * mm, "end": v(-38.85, -18.1) * mm});
            skLineSegment(sketch, "E2199", {"start": v(-38.85, -18.1) * mm, "end": v(-38.76, -17.94) * mm});
            skLineSegment(sketch, "E2200", {"start": v(-38.76, -17.94) * mm, "end": v(-38.66, -17.78) * mm});
            skLineSegment(sketch, "E2201", {"start": v(-38.66, -17.78) * mm, "end": v(-38.76, -17.58) * mm});
            skLineSegment(sketch, "E2202", {"start": v(-38.76, -17.58) * mm, "end": v(-38.78, -17.44) * mm});
            skLineSegment(sketch, "E2203", {"start": v(-38.78, -17.44) * mm, "end": v(-39.62, -16.62) * mm});
            skLineSegment(sketch, "E2204", {"start": v(-39.62, -16.62) * mm, "end": v(-40.55, -15.9) * mm});
            skLineSegment(sketch, "E2205", {"start": v(-40.55, -15.9) * mm, "end": v(-40.7, -15.9) * mm});
            skLineSegment(sketch, "E2206", {"start": v(-40.7, -15.9) * mm, "end": v(-40.9, -15.83) * mm});
            skLineSegment(sketch, "E2207", {"start": v(-40.9, -15.83) * mm, "end": v(-41.05, -15.96) * mm});
            skLineSegment(sketch, "E2208", {"start": v(-41.05, -15.96) * mm, "end": v(-41.2, -16.07) * mm});
            skLineSegment(sketch, "E2209", {"start": v(-41.2, -16.07) * mm, "end": v(-41.37, -16.18) * mm});
            skLineSegment(sketch, "E2210", {"start": v(-41.37, -16.18) * mm, "end": v(-41.7, -16.39) * mm});
            skLineSegment(sketch, "E2211", {"start": v(-41.7, -16.39) * mm, "end": v(-42.05, -16.58) * mm});
            skLineSegment(sketch, "E2212", {"start": v(-42.05, -16.58) * mm, "end": v(-42.42, -16.75) * mm});
            skLineSegment(sketch, "E2213", {"start": v(-42.42, -16.75) * mm, "end": v(-42.8, -16.91) * mm});
            skLineSegment(sketch, "E2214", {"start": v(-42.8, -16.91) * mm, "end": v(-43.18, -17.06) * mm});
            skLineSegment(sketch, "E2215", {"start": v(-43.18, -17.06) * mm, "end": v(-43.58, -17.2) * mm});
            skLineSegment(sketch, "E2216", {"start": v(-43.58, -17.2) * mm, "end": v(-43.99, -17.32) * mm});
            skLineSegment(sketch, "E2217", {"start": v(-43.99, -17.32) * mm, "end": v(-44.3, -17.41) * mm});
            skLineSegment(sketch, "E2218", {"start": v(-44.3, -17.41) * mm, "end": v(-45.9, -15.56) * mm});
            skLineSegment(sketch, "E2219", {"start": v(-45.9, -15.56) * mm, "end": v(-45.77, -15.26) * mm});
            skLineSegment(sketch, "E2220", {"start": v(-45.77, -15.26) * mm, "end": v(-45.6, -14.88) * mm});
            skLineSegment(sketch, "E2221", {"start": v(-45.6, -14.88) * mm, "end": v(-45.4, -14.5) * mm});
            skLineSegment(sketch, "E2222", {"start": v(-45.4, -14.5) * mm, "end": v(-45.2, -14.14) * mm});
            skLineSegment(sketch, "E2223", {"start": v(-45.2, -14.14) * mm, "end": v(-44.98, -13.8) * mm});
            skLineSegment(sketch, "E2224", {"start": v(-44.98, -13.8) * mm, "end": v(-44.76, -13.46) * mm});
            skLineSegment(sketch, "E2225", {"start": v(-44.76, -13.46) * mm, "end": v(-44.52, -13.13) * mm});
            skLineSegment(sketch, "E2226", {"start": v(-44.52, -13.13) * mm, "end": v(-44.27, -12.83) * mm});
            skLineSegment(sketch, "E2227", {"start": v(-44.27, -12.83) * mm, "end": v(-44.14, -12.69) * mm});
            skLineSegment(sketch, "E2228", {"start": v(-44.14, -12.69) * mm, "end": v(-44, -12.55) * mm});
            skLineSegment(sketch, "E2229", {"start": v(-44, -12.55) * mm, "end": v(-43.86, -12.42) * mm});
            skLineSegment(sketch, "E2230", {"start": v(-43.86, -12.42) * mm, "end": v(-43.9, -12.2) * mm});
            skLineSegment(sketch, "E2231", {"start": v(-43.9, -12.2) * mm, "end": v(-43.88, -12.07) * mm});
            skLineSegment(sketch, "E2232", {"start": v(-43.88, -12.07) * mm, "end": v(-44.46, -11.04) * mm});
            skLineSegment(sketch, "E2233", {"start": v(-44.46, -11.04) * mm, "end": v(-45.15, -10.1) * mm});
            skLineSegment(sketch, "E2234", {"start": v(-45.15, -10.1) * mm, "end": v(-45.28, -10.05) * mm});
            skLineSegment(sketch, "E2235", {"start": v(-45.28, -10.05) * mm, "end": v(-45.46, -9.93) * mm});
            skLineSegment(sketch, "E2236", {"start": v(-45.46, -9.93) * mm, "end": v(-45.64, -10) * mm});
            skLineSegment(sketch, "E2237", {"start": v(-45.64, -10) * mm, "end": v(-45.82, -10.07) * mm});
            skLineSegment(sketch, "E2238", {"start": v(-45.82, -10.07) * mm, "end": v(-46, -10.13) * mm});
            skLineSegment(sketch, "E2239", {"start": v(-46, -10.13) * mm, "end": v(-46.39, -10.23) * mm});
            skLineSegment(sketch, "E2240", {"start": v(-46.39, -10.23) * mm, "end": v(-46.78, -10.31) * mm});
            skLineSegment(sketch, "E2241", {"start": v(-46.78, -10.31) * mm, "end": v(-47.18, -10.38) * mm});
            skLineSegment(sketch, "E2242", {"start": v(-47.18, -10.38) * mm, "end": v(-47.58, -10.43) * mm});
            skLineSegment(sketch, "E2243", {"start": v(-47.58, -10.43) * mm, "end": v(-48, -10.46) * mm});
            skLineSegment(sketch, "E2244", {"start": v(-48, -10.46) * mm, "end": v(-48.42, -10.48) * mm});
            skLineSegment(sketch, "E2245", {"start": v(-48.42, -10.48) * mm, "end": v(-48.84, -10.49) * mm});
            skLineSegment(sketch, "E2246", {"start": v(-48.84, -10.49) * mm, "end": v(-49.17, -10.48) * mm});
            skLineSegment(sketch, "E2247", {"start": v(-49.17, -10.48) * mm, "end": v(-50.18, -8.26) * mm});
            skLineSegment(sketch, "E2248", {"start": v(-50.18, -8.26) * mm, "end": v(-49.98, -8) * mm});
            skLineSegment(sketch, "E2249", {"start": v(-49.98, -8) * mm, "end": v(-49.7, -7.7) * mm});
            skLineSegment(sketch, "E2250", {"start": v(-49.7, -7.7) * mm, "end": v(-49.4, -7.38) * mm});
            skLineSegment(sketch, "E2251", {"start": v(-49.4, -7.38) * mm, "end": v(-49.1, -7.1) * mm});
            skLineSegment(sketch, "E2252", {"start": v(-49.1, -7.1) * mm, "end": v(-48.8, -6.82) * mm});
            skLineSegment(sketch, "E2253", {"start": v(-48.8, -6.82) * mm, "end": v(-48.5, -6.56) * mm});
            skLineSegment(sketch, "E2254", {"start": v(-48.5, -6.56) * mm, "end": v(-48.17, -6.32) * mm});
            skLineSegment(sketch, "E2255", {"start": v(-48.17, -6.32) * mm, "end": v(-47.85, -6.1) * mm});
            skLineSegment(sketch, "E2256", {"start": v(-47.85, -6.1) * mm, "end": v(-47.68, -6) * mm});
            skLineSegment(sketch, "E2257", {"start": v(-47.68, -6) * mm, "end": v(-47.51, -5.9) * mm});
            skLineSegment(sketch, "E2258", {"start": v(-47.51, -5.9) * mm, "end": v(-47.34, -5.82) * mm});
            skLineSegment(sketch, "E2259", {"start": v(-47.34, -5.82) * mm, "end": v(-47.31, -5.6) * mm});
            skLineSegment(sketch, "E2260", {"start": v(-47.31, -5.6) * mm, "end": v(-47.26, -5.47) * mm});
            skLineSegment(sketch, "E2261", {"start": v(-47.26, -5.47) * mm, "end": v(-47.52, -4.33) * mm});
            skLineSegment(sketch, "E2262", {"start": v(-47.52, -4.33) * mm, "end": v(-47.92, -3.22) * mm});
            skLineSegment(sketch, "E2263", {"start": v(-47.92, -3.22) * mm, "end": v(-48.04, -3.15) * mm});
            skLineSegment(sketch, "E2264", {"start": v(-48.04, -3.15) * mm, "end": v(-48.17, -2.98) * mm});
            skLineSegment(sketch, "E2265", {"start": v(-48.17, -2.98) * mm, "end": v(-48.36, -3) * mm});
            skLineSegment(sketch, "E2266", {"start": v(-48.36, -3) * mm, "end": v(-48.56, -3.01) * mm});
            skLineSegment(sketch, "E2267", {"start": v(-48.56, -3.01) * mm, "end": v(-48.75, -3.02) * mm});
            skLineSegment(sketch, "E2268", {"start": v(-48.75, -3.02) * mm, "end": v(-49.15, -3) * mm});
            skLineSegment(sketch, "E2269", {"start": v(-49.15, -3) * mm, "end": v(-49.54, -2.98) * mm});
            skLineSegment(sketch, "E2270", {"start": v(-49.54, -2.98) * mm, "end": v(-49.94, -2.93) * mm});
            skLineSegment(sketch, "E2271", {"start": v(-49.94, -2.93) * mm, "end": v(-50.35, -2.86) * mm});
            skLineSegment(sketch, "E2272", {"start": v(-50.35, -2.86) * mm, "end": v(-50.76, -2.78) * mm});
            skLineSegment(sketch, "E2273", {"start": v(-50.76, -2.78) * mm, "end": v(-51.16, -2.68) * mm});
            skLineSegment(sketch, "E2274", {"start": v(-51.16, -2.68) * mm, "end": v(-51.58, -2.56) * mm});
            skLineSegment(sketch, "E2275", {"start": v(-51.58, -2.56) * mm, "end": v(-51.89, -2.46) * mm});
            skLineSegment(sketch, "E2276", {"start": v(-51.89, -2.46) * mm, "end": v(-52.23, -0.04) * mm});
            skLineSegment(sketch, "E2277", {"start": v(-52.23, -0.04) * mm, "end": v(-51.96, 0.14) * mm});
            skLineSegment(sketch, "E2278", {"start": v(-51.96, 0.14) * mm, "end": v(-51.6, 0.36) * mm});
            skLineSegment(sketch, "E2279", {"start": v(-51.6, 0.36) * mm, "end": v(-51.24, 0.57) * mm});
            skLineSegment(sketch, "E2280", {"start": v(-51.24, 0.57) * mm, "end": v(-50.87, 0.77) * mm});
            skLineSegment(sketch, "E2281", {"start": v(-50.87, 0.77) * mm, "end": v(-50.5, 0.95) * mm});
            skLineSegment(sketch, "E2282", {"start": v(-50.5, 0.95) * mm, "end": v(-50.13, 1.1) * mm});
            skLineSegment(sketch, "E2283", {"start": v(-50.13, 1.1) * mm, "end": v(-49.76, 1.25) * mm});
            skLineSegment(sketch, "E2284", {"start": v(-49.76, 1.25) * mm, "end": v(-49.38, 1.37) * mm});
            skLineSegment(sketch, "E2285", {"start": v(-49.38, 1.37) * mm, "end": v(-49.2, 1.42) * mm});
            skLineSegment(sketch, "E2286", {"start": v(-49.2, 1.42) * mm, "end": v(-49, 1.46) * mm});
            skLineSegment(sketch, "E2287", {"start": v(-49, 1.46) * mm, "end": v(-48.82, 1.5) * mm});
            skLineSegment(sketch, "E2288", {"start": v(-48.82, 1.5) * mm, "end": v(-48.73, 1.7) * mm});
            skLineSegment(sketch, "E2289", {"start": v(-48.73, 1.7) * mm, "end": v(-48.64, 1.8) * mm});
            skLineSegment(sketch, "E2290", {"start": v(-48.64, 1.8) * mm, "end": v(-48.57, 2.98) * mm});
            skLineSegment(sketch, "E2291", {"start": v(-29.66, 1.57) * mm, "end": v(-43.8, 3.6) * mm});
            skLineSegment(sketch, "E2292", {"start": v(-43.8, 3.6) * mm, "end": v(-45, 2.57) * mm});
            skLineSegment(sketch, "E2293", {"start": v(-45, 2.57) * mm, "end": v(-44.92, 1.1) * mm});
            skLineSegment(sketch, "E2294", {"start": v(-44.92, 1.1) * mm, "end": v(-44.75, -0.35) * mm});
            skLineSegment(sketch, "E2295", {"start": v(-44.75, -0.35) * mm, "end": v(-44.48, -1.8) * mm});
            skLineSegment(sketch, "E2296", {"start": v(-44.48, -1.8) * mm, "end": v(-44.12, -3.21) * mm});
            skLineSegment(sketch, "E2297", {"start": v(-44.12, -3.21) * mm, "end": v(-43.67, -4.61) * mm});
            skLineSegment(sketch, "E2298", {"start": v(-43.67, -4.61) * mm, "end": v(-43.12, -5.97) * mm});
            skLineSegment(sketch, "E2299", {"start": v(-43.12, -5.97) * mm, "end": v(-42.5, -7.3) * mm});
            skLineSegment(sketch, "E2300", {"start": v(-42.5, -7.3) * mm, "end": v(-41.78, -8.58) * mm});
            skLineSegment(sketch, "E2301", {"start": v(-41.78, -8.58) * mm, "end": v(-40.98, -9.8) * mm});
            skLineSegment(sketch, "E2302", {"start": v(-40.98, -9.8) * mm, "end": v(-40.1, -10.98) * mm});
            skLineSegment(sketch, "E2303", {"start": v(-40.1, -10.98) * mm, "end": v(-39.15, -12.1) * mm});
            skLineSegment(sketch, "E2304", {"start": v(-39.15, -12.1) * mm, "end": v(-38.12, -13.15) * mm});
            skLineSegment(sketch, "E2305", {"start": v(-38.12, -13.15) * mm, "end": v(-37.03, -14.13) * mm});
            skLineSegment(sketch, "E2306", {"start": v(-37.03, -14.13) * mm, "end": v(-35.88, -15.04) * mm});
            skLineSegment(sketch, "E2307", {"start": v(-35.88, -15.04) * mm, "end": v(-34.67, -15.87) * mm});
            skLineSegment(sketch, "E2308", {"start": v(-34.67, -15.87) * mm, "end": v(-33.4, -16.62) * mm});
            skLineSegment(sketch, "E2309", {"start": v(-33.4, -16.62) * mm, "end": v(-32.1, -17.28) * mm});
            skLineSegment(sketch, "E2310", {"start": v(-32.1, -17.28) * mm, "end": v(-30.74, -17.86) * mm});
            skLineSegment(sketch, "E2311", {"start": v(-30.74, -17.86) * mm, "end": v(-29.36, -18.34) * mm});
            skLineSegment(sketch, "E2312", {"start": v(-29.36, -18.34) * mm, "end": v(-27.95, -18.74) * mm});
            skLineSegment(sketch, "E2313", {"start": v(-27.95, -18.74) * mm, "end": v(-26.51, -19.04) * mm});
            skLineSegment(sketch, "E2314", {"start": v(-26.51, -19.04) * mm, "end": v(-25.06, -19.25) * mm});
            skLineSegment(sketch, "E2315", {"start": v(-25.06, -19.25) * mm, "end": v(-23.6, -19.36) * mm});
            skLineSegment(sketch, "E2316", {"start": v(-23.6, -19.36) * mm, "end": v(-22.13, -19.37) * mm});
            skLineSegment(sketch, "E2317", {"start": v(-22.13, -19.37) * mm, "end": v(-20.66, -19.29) * mm});
            skLineSegment(sketch, "E2318", {"start": v(-20.66, -19.29) * mm, "end": v(-19.2, -19.11) * mm});
            skLineSegment(sketch, "E2319", {"start": v(-19.2, -19.11) * mm, "end": v(-17.76, -18.84) * mm});
            skLineSegment(sketch, "E2320", {"start": v(-17.76, -18.84) * mm, "end": v(-17.04, -17.44) * mm});
            skLineSegment(sketch, "E2321", {"start": v(-17.04, -17.44) * mm, "end": v(-22.35, -4.17) * mm});
            skLineSegment(sketch, "E2322", {"start": v(-22.35, -4.17) * mm, "end": v(-24.16, -2.87) * mm});
            skLineSegment(sketch, "E2323", {"start": v(-24.16, -2.87) * mm, "end": v(-24.94, -2.6) * mm});
            skLineSegment(sketch, "E2324", {"start": v(-24.94, -2.6) * mm, "end": v(-25.69, -2.24) * mm});
            skLineSegment(sketch, "E2325", {"start": v(-25.69, -2.24) * mm, "end": v(-26.38, -1.77) * mm});
            skLineSegment(sketch, "E2326", {"start": v(-26.38, -1.77) * mm, "end": v(-27, -1.21) * mm});
            skLineSegment(sketch, "E2327", {"start": v(-27, -1.21) * mm, "end": v(-27.53, -0.58) * mm});
            skLineSegment(sketch, "E2328", {"start": v(-27.53, -0.58) * mm, "end": v(-27.97, 0.13) * mm});
            skLineSegment(sketch, "E2329", {"start": v(-27.97, 0.13) * mm, "end": v(-29.66, 1.57) * mm});
            skLineSegment(sketch, "E2330", {"start": v(-17.92, -2.4) * mm, "end": v(-12.61, -15.66) * mm});
            skLineSegment(sketch, "E2331", {"start": v(-12.61, -15.66) * mm, "end": v(-11.12, -16.18) * mm});
            skLineSegment(sketch, "E2332", {"start": v(-11.12, -16.18) * mm, "end": v(-9.89, -15.38) * mm});
            skLineSegment(sketch, "E2333", {"start": v(-9.89, -15.38) * mm, "end": v(-8.71, -14.5) * mm});
            skLineSegment(sketch, "E2334", {"start": v(-8.71, -14.5) * mm, "end": v(-7.6, -13.55) * mm});
            skLineSegment(sketch, "E2335", {"start": v(-7.6, -13.55) * mm, "end": v(-6.54, -12.53) * mm});
            skLineSegment(sketch, "E2336", {"start": v(-6.54, -12.53) * mm, "end": v(-5.56, -11.44) * mm});
            skLineSegment(sketch, "E2337", {"start": v(-5.56, -11.44) * mm, "end": v(-4.65, -10.29) * mm});
            skLineSegment(sketch, "E2338", {"start": v(-4.65, -10.29) * mm, "end": v(-3.82, -9.08) * mm});
            skLineSegment(sketch, "E2339", {"start": v(-3.82, -9.08) * mm, "end": v(-3.07, -7.82) * mm});
            skLineSegment(sketch, "E2340", {"start": v(-3.07, -7.82) * mm, "end": v(-2.4, -6.5) * mm});
            skLineSegment(sketch, "E2341", {"start": v(-2.4, -6.5) * mm, "end": v(-1.82, -5.16) * mm});
            skLineSegment(sketch, "E2342", {"start": v(-1.82, -5.16) * mm, "end": v(-1.34, -3.78) * mm});
            skLineSegment(sketch, "E2343", {"start": v(-1.34, -3.78) * mm, "end": v(-0.94, -2.37) * mm});
            skLineSegment(sketch, "E2344", {"start": v(-0.94, -2.37) * mm, "end": v(-0.63, -0.93) * mm});
            skLineSegment(sketch, "E2345", {"start": v(-0.63, -0.93) * mm, "end": v(-0.43, 0.52) * mm});
            skLineSegment(sketch, "E2346", {"start": v(-0.43, 0.52) * mm, "end": v(-0.31, 1.99) * mm});
            skLineSegment(sketch, "E2347", {"start": v(-0.31, 1.99) * mm, "end": v(-0.3, 3.45) * mm});
            skLineSegment(sketch, "E2348", {"start": v(-0.3, 3.45) * mm, "end": v(-0.38, 4.92) * mm});
            skLineSegment(sketch, "E2349", {"start": v(-0.38, 4.92) * mm, "end": v(-0.55, 6.38) * mm});
            skLineSegment(sketch, "E2350", {"start": v(-0.55, 6.38) * mm, "end": v(-0.82, 7.82) * mm});
            skLineSegment(sketch, "E2351", {"start": v(-0.82, 7.82) * mm, "end": v(-1.19, 9.24) * mm});
            skLineSegment(sketch, "E2352", {"start": v(-1.19, 9.24) * mm, "end": v(-1.64, 10.63) * mm});
            skLineSegment(sketch, "E2353", {"start": v(-1.64, 10.63) * mm, "end": v(-2.2, 12) * mm});
            skLineSegment(sketch, "E2354", {"start": v(-2.2, 12) * mm, "end": v(-2.83, 13.32) * mm});
            skLineSegment(sketch, "E2355", {"start": v(-2.83, 13.32) * mm, "end": v(-3.55, 14.6) * mm});
            skLineSegment(sketch, "E2356", {"start": v(-3.55, 14.6) * mm, "end": v(-4.35, 15.82) * mm});
            skLineSegment(sketch, "E2357", {"start": v(-4.35, 15.82) * mm, "end": v(-5.23, 17) * mm});
            skLineSegment(sketch, "E2358", {"start": v(-5.23, 17) * mm, "end": v(-6.2, 18.1) * mm});
            skLineSegment(sketch, "E2359", {"start": v(-6.2, 18.1) * mm, "end": v(-7.77, 18.03) * mm});
            skLineSegment(sketch, "E2360", {"start": v(-7.77, 18.03) * mm, "end": v(-16.6, 6.8) * mm});
            skLineSegment(sketch, "E2361", {"start": v(-16.6, 6.8) * mm, "end": v(-16.82, 4.59) * mm});
            skLineSegment(sketch, "E2362", {"start": v(-16.82, 4.59) * mm, "end": v(-16.66, 3.78) * mm});
            skLineSegment(sketch, "E2363", {"start": v(-16.66, 3.78) * mm, "end": v(-16.6, 2.95) * mm});
            skLineSegment(sketch, "E2364", {"start": v(-16.6, 2.95) * mm, "end": v(-16.66, 2.12) * mm});
            skLineSegment(sketch, "E2365", {"start": v(-16.66, 2.12) * mm, "end": v(-16.84, 1.3) * mm});
            skLineSegment(sketch, "E2366", {"start": v(-16.84, 1.3) * mm, "end": v(-17.12, 0.52) * mm});
            skLineSegment(sketch, "E2367", {"start": v(-17.12, 0.52) * mm, "end": v(-17.51, -0.21) * mm});
            skLineSegment(sketch, "E2368", {"start": v(-17.51, -0.21) * mm, "end": v(-17.92, -2.4) * mm});
            skLineSegment(sketch, "E2369", {"start": v(-20.35, 9.75) * mm, "end": v(-11.52, 20.98) * mm});
            skLineSegment(sketch, "E2370", {"start": v(-11.52, 20.98) * mm, "end": v(-11.82, 22.53) * mm});
            skLineSegment(sketch, "E2371", {"start": v(-11.82, 22.53) * mm, "end": v(-13.12, 23.2) * mm});
            skLineSegment(sketch, "E2372", {"start": v(-13.12, 23.2) * mm, "end": v(-14.47, 23.78) * mm});
            skLineSegment(sketch, "E2373", {"start": v(-14.47, 23.78) * mm, "end": v(-15.85, 24.27) * mm});
            skLineSegment(sketch, "E2374", {"start": v(-15.85, 24.27) * mm, "end": v(-17.26, 24.67) * mm});
            skLineSegment(sketch, "E2375", {"start": v(-17.26, 24.67) * mm, "end": v(-18.7, 24.98) * mm});
            skLineSegment(sketch, "E2376", {"start": v(-18.7, 24.98) * mm, "end": v(-20.15, 25.19) * mm});
            skLineSegment(sketch, "E2377", {"start": v(-20.15, 25.19) * mm, "end": v(-21.61, 25.3) * mm});
            skLineSegment(sketch, "E2378", {"start": v(-21.61, 25.3) * mm, "end": v(-23.08, 25.32) * mm});
            skLineSegment(sketch, "E2379", {"start": v(-23.08, 25.32) * mm, "end": v(-24.55, 25.25) * mm});
            skLineSegment(sketch, "E2380", {"start": v(-24.55, 25.25) * mm, "end": v(-26, 25.07) * mm});
            skLineSegment(sketch, "E2381", {"start": v(-26, 25.07) * mm, "end": v(-27.45, 24.8) * mm});
            skLineSegment(sketch, "E2382", {"start": v(-27.45, 24.8) * mm, "end": v(-28.87, 24.44) * mm});
            skLineSegment(sketch, "E2383", {"start": v(-28.87, 24.44) * mm, "end": v(-30.26, 23.99) * mm});
            skLineSegment(sketch, "E2384", {"start": v(-30.26, 23.99) * mm, "end": v(-31.63, 23.44) * mm});
            skLineSegment(sketch, "E2385", {"start": v(-31.63, 23.44) * mm, "end": v(-32.95, 22.8) * mm});
            skLineSegment(sketch, "E2386", {"start": v(-32.95, 22.8) * mm, "end": v(-34.23, 22.1) * mm});
            skLineSegment(sketch, "E2387", {"start": v(-34.23, 22.1) * mm, "end": v(-35.46, 21.29) * mm});
            skLineSegment(sketch, "E2388", {"start": v(-35.46, 21.29) * mm, "end": v(-36.63, 20.4) * mm});
            skLineSegment(sketch, "E2389", {"start": v(-36.63, 20.4) * mm, "end": v(-37.75, 19.45) * mm});
            skLineSegment(sketch, "E2390", {"start": v(-37.75, 19.45) * mm, "end": v(-38.8, 18.43) * mm});
            skLineSegment(sketch, "E2391", {"start": v(-38.8, 18.43) * mm, "end": v(-39.77, 17.33) * mm});
            skLineSegment(sketch, "E2392", {"start": v(-39.77, 17.33) * mm, "end": v(-40.68, 16.18) * mm});
            skLineSegment(sketch, "E2393", {"start": v(-40.68, 16.18) * mm, "end": v(-41.5, 14.97) * mm});
            skLineSegment(sketch, "E2394", {"start": v(-41.5, 14.97) * mm, "end": v(-42.25, 13.7) * mm});
            skLineSegment(sketch, "E2395", {"start": v(-42.25, 13.7) * mm, "end": v(-42.91, 12.4) * mm});
            skLineSegment(sketch, "E2396", {"start": v(-42.91, 12.4) * mm, "end": v(-43.49, 11.04) * mm});
            skLineSegment(sketch, "E2397", {"start": v(-43.49, 11.04) * mm, "end": v(-43.97, 9.66) * mm});
            skLineSegment(sketch, "E2398", {"start": v(-43.97, 9.66) * mm, "end": v(-43.12, 8.33) * mm});
            skLineSegment(sketch, "E2399", {"start": v(-43.12, 8.33) * mm, "end": v(-28.98, 6.3) * mm});
            skLineSegment(sketch, "E2400", {"start": v(-28.98, 6.3) * mm, "end": v(-26.95, 7.2) * mm});
            skLineSegment(sketch, "E2401", {"start": v(-26.95, 7.2) * mm, "end": v(-26.33, 7.76) * mm});
            skLineSegment(sketch, "E2402", {"start": v(-26.33, 7.76) * mm, "end": v(-25.64, 8.22) * mm});
            skLineSegment(sketch, "E2403", {"start": v(-25.64, 8.22) * mm, "end": v(-24.89, 8.58) * mm});
            skLineSegment(sketch, "E2404", {"start": v(-24.89, 8.58) * mm, "end": v(-24.1, 8.84) * mm});
            skLineSegment(sketch, "E2405", {"start": v(-24.1, 8.84) * mm, "end": v(-23.28, 8.98) * mm});
            skLineSegment(sketch, "E2406", {"start": v(-23.28, 8.98) * mm, "end": v(-22.45, 9.01) * mm});
            skLineSegment(sketch, "E2407", {"start": v(-22.45, 9.01) * mm, "end": v(-20.35, 9.75) * mm});
            skCircle(sketch, "E2408", {"center": v(-22.64, 2.98) * mm, "radius": 1.27 * mm});
            skSolve(sketch);
        }
        {
            var Q0;
            Q0=makeQuery(id+"F2.imprint","IMPRINT",FACE,{"disambiguationData":[TD([[makeQuery(id+"F2.imprint","IMPRINT",EDGE,{"derivedFrom":sQuery(id+"F2.wireOp",EDGE,"E1300")}),-1.0]])]});
            extrude(context, id + "F3", {"entities" : qUnion([Q0]), "oppositeDirection" : true, "depth" : 3.8 * mm, "offsetDistance" : 25.4 * mm});
        }
        {
            var Q0;
            {var subQ4=sQuery(id+"F2.wireOp",EDGE,"E1321");Q0=makeQuery(id+"F2.imprint","IMPRINT",FACE,{"disambiguationData":[TD([[makeQuery(id+"F2.imprint","IMPRINT",EDGE,{"derivedFrom":subQ4}),1.0]])]});}
            extrude(context, id + "F4", {"entities" : qUnion([Q0]), "oppositeDirection" : true, "depth" : 2.54 * mm, "offsetDistance" : 25.4 * mm});
        }
    });
